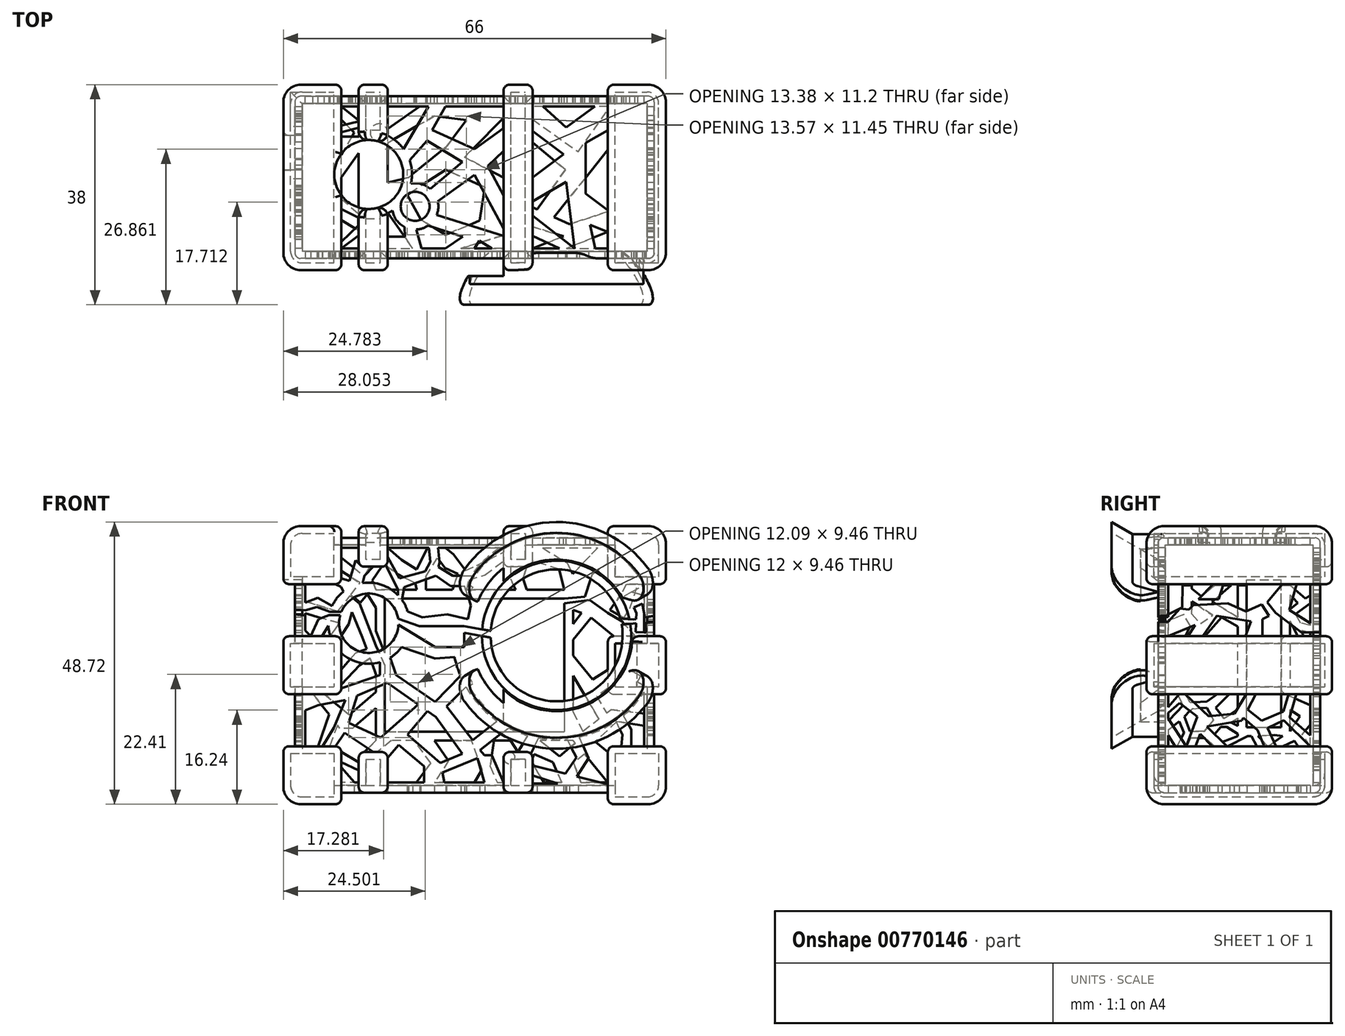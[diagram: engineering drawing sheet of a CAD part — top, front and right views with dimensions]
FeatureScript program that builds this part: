
annotation { "Feature Type Name" : "Feature", "Feature Type Description" : "" }
export const myFeature = defineFeature(function(context is Context, id is Id, definition is map)
    precondition{}
    {
        {
            var Q0;
            Q0=qCreatedBy(makeId("Front.planeOp"),FACE);
            var sketch = newSketch(context, id + "F0", { "sketchPlane" : qUnion([Q0])});
            skLineSegment(sketch, "E0.bottom", {"start": v(-31, 22) * mm, "end": v(31, 22) * mm});
            skLineSegment(sketch, "E0.top", {"start": v(-31, -22) * mm, "end": v(31, -22) * mm});
            skLineSegment(sketch, "E0.left", {"start": v(-31, 22) * mm, "end": v(-31, -22) * mm});
            skLineSegment(sketch, "E0.right", {"start": v(31, 22) * mm, "end": v(31, -22) * mm});
            skPoint(sketch, "E0.middle", {"position": v(0, 0) * mm});
            skSolve(sketch);
        }
        {
            var Q0;
            Q0=qSketchRegion(id+"F0",true);
            extrude(context, id + "F1", {"entities" : qUnion([Q0]), "endBound" : BoundingType.SYMMETRIC, "depth" : (25.5 + 1.25 + 1.25) * mm, "offsetDistance" : 25 * mm});
        }
        {
            var Q0;
            Q0=qCreatedBy(makeId("Front.planeOp"),FACE);
            var sketch = newSketch(context, id + "F2", { "sketchPlane" : qUnion([Q0])});
            skLineSegment(sketch, "E1.bottom", {"start": v(-33, 24) * mm, "end": v(-23, 24) * mm});
            skLineSegment(sketch, "E1.top", {"start": v(-33, 14) * mm, "end": v(-23, 14) * mm});
            skLineSegment(sketch, "E1.left", {"start": v(-33, 24) * mm, "end": v(-33, 14) * mm});
            skLineSegment(sketch, "E1.right", {"start": v(-23, 24) * mm, "end": v(-23, 14) * mm});
            skLineSegment(sketch, "E2.bottom", {"start": v(-20, 24) * mm, "end": v(-15, 24) * mm});
            skLineSegment(sketch, "E2.top", {"start": v(-20, 17) * mm, "end": v(-15, 17) * mm});
            skLineSegment(sketch, "E2.left", {"start": v(-20, 24) * mm, "end": v(-20, 17) * mm});
            skLineSegment(sketch, "E2.right", {"start": v(-15, 24) * mm, "end": v(-15, 17) * mm});
            skLineSegment(sketch, "E3.bottom", {"start": v(23, 24) * mm, "end": v(33, 24) * mm});
            skLineSegment(sketch, "E3.top", {"start": v(23, 14) * mm, "end": v(33, 14) * mm});
            skLineSegment(sketch, "E3.left", {"start": v(23, 24) * mm, "end": v(23, 14) * mm});
            skLineSegment(sketch, "E3.right", {"start": v(33, 24) * mm, "end": v(33, 14) * mm});
            skLineSegment(sketch, "E4.bottom", {"start": v(-33, 5) * mm, "end": v(-23, 5) * mm});
            skLineSegment(sketch, "E4.top", {"start": v(-33, -5) * mm, "end": v(-23, -5) * mm});
            skLineSegment(sketch, "E4.left", {"start": v(-33, 5) * mm, "end": v(-33, -5) * mm});
            skLineSegment(sketch, "E4.right", {"start": v(-23, 5) * mm, "end": v(-23, -5) * mm});
            skLineSegment(sketch, "E5.bottom", {"start": v(-33, -14) * mm, "end": v(-23, -14) * mm});
            skLineSegment(sketch, "E5.top", {"start": v(-33, -24) * mm, "end": v(-23, -24) * mm});
            skLineSegment(sketch, "E5.left", {"start": v(-33, -14) * mm, "end": v(-33, -24) * mm});
            skLineSegment(sketch, "E5.right", {"start": v(-23, -14) * mm, "end": v(-23, -24) * mm});
            skLineSegment(sketch, "E6.bottom", {"start": v(-20, -15) * mm, "end": v(-15, -15) * mm});
            skLineSegment(sketch, "E6.top", {"start": v(-20, -22) * mm, "end": v(-15, -22) * mm});
            skLineSegment(sketch, "E6.left", {"start": v(-20, -15) * mm, "end": v(-20, -22) * mm});
            skLineSegment(sketch, "E6.right", {"start": v(-15, -15) * mm, "end": v(-15, -22) * mm});
            skLineSegment(sketch, "E7.bottom", {"start": v(23, -14) * mm, "end": v(33, -14) * mm});
            skLineSegment(sketch, "E7.top", {"start": v(23, -24) * mm, "end": v(33, -24) * mm});
            skLineSegment(sketch, "E7.left", {"start": v(23, -14) * mm, "end": v(23, -24) * mm});
            skLineSegment(sketch, "E7.right", {"start": v(33, -14) * mm, "end": v(33, -24) * mm});
            skLineSegment(sketch, "E8.bottom", {"start": v(23, 5) * mm, "end": v(33, 5) * mm});
            skLineSegment(sketch, "E8.top", {"start": v(23, -5) * mm, "end": v(33, -5) * mm});
            skLineSegment(sketch, "E8.left", {"start": v(23, 5) * mm, "end": v(23, -5) * mm});
            skLineSegment(sketch, "E8.right", {"start": v(33, 5) * mm, "end": v(33, -5) * mm});
            skLineSegment(sketch, "E9.bottom", {"start": v(5, 24) * mm, "end": v(10, 24) * mm});
            skLineSegment(sketch, "E9.top", {"start": v(5, 17) * mm, "end": v(10, 17) * mm});
            skLineSegment(sketch, "E9.left", {"start": v(5, 24) * mm, "end": v(5, 17) * mm});
            skLineSegment(sketch, "E9.right", {"start": v(10, 24) * mm, "end": v(10, 17) * mm});
            skLineSegment(sketch, "E10.bottom", {"start": v(5, -15) * mm, "end": v(10, -15) * mm});
            skLineSegment(sketch, "E10.top", {"start": v(5, -22) * mm, "end": v(10, -22) * mm});
            skLineSegment(sketch, "E10.left", {"start": v(5, -15) * mm, "end": v(5, -22) * mm});
            skLineSegment(sketch, "E10.right", {"start": v(10, -15) * mm, "end": v(10, -22) * mm});
            skSolve(sketch);
        }
        {
            var Q0;
            Q0=qSketchRegion(id+"F2",true);
            extrude(context, id + "F3", {"entities" : qUnion([Q0]), "operationType" : NewBodyOperationType.ADD, "endBound" : BoundingType.SYMMETRIC, "depth" : (28 + 4) * mm, "offsetDistance" : 25 * mm});
        }
        {
            var Q0;
            Q0=makeQuery(id+"F1.opExtrude","CAP_FACE",FACE,{"disambiguationData":[OSD([sQuery(id+"F0.wireOp",EDGE,"E0.bottom"),sQuery(id+"F0.wireOp",EDGE,"E0.top"),sQuery(id+"F0.wireOp",EDGE,"E0.left"),sQuery(id+"F0.wireOp",EDGE,"E0.right")])],"isStart":false});
            var Q1;
            Q1=makeQuery(id+"F1.opExtrude","SWEPT_BODY",BODY,{"disambiguationData":[OSD([sQuery(id+"F0.wireOp",EDGE,"E0.bottom"),sQuery(id+"F0.wireOp",EDGE,"E0.top"),sQuery(id+"F0.wireOp",EDGE,"E0.left"),sQuery(id+"F0.wireOp",EDGE,"E0.right")])]});
            shell(context, id + "F4", {"isHollow" : true, "entities" : qUnion([Q0]), "parts" : qUnion([Q1]), "thickness" : 1.25 * mm});
        }
        {
            var Q0;
            {var subQ0=sQuery(id+"F2.wireOp",EDGE,"E8.right");var subQ1=sQuery(id+"F2.wireOp",EDGE,"E8.left");var subQ2=sQuery(id+"F2.wireOp",EDGE,"E8.top");var subQ3=sQuery(id+"F2.wireOp",EDGE,"E8.bottom");Q0=makeQuery(id+"F4.opShell","OFFSET_FACE",FACE,{"disambiguationData":[OSD([subQ3,subQ2,subQ1,subQ0]),TDD([makeQuery(id+"F3.opExtrude","CAP_FACE",FACE,{"disambiguationData":[OSD([subQ3,subQ2,subQ1,subQ0])],"isStart":false})])]});}
            var sketch = newSketch(context, id + "F5", { "sketchPlane" : qUnion([Q0])});
            skLineSegment(sketch, "E11.bottom", {"start": v(-24.25, 3.75) * mm, "end": v(-28, 3.75) * mm});
            skLineSegment(sketch, "E11.top", {"start": v(-24.25, -3.75) * mm, "end": v(-28, -3.75) * mm});
            skLineSegment(sketch, "E11.left", {"start": v(-24.25, 3.75) * mm, "end": v(-24.25, -3.75) * mm});
            skLineSegment(sketch, "E11.right", {"start": v(-28, 3.75) * mm, "end": v(-28, -3.75) * mm});
            skSolve(sketch);
        }
        {
            var Q0;
            Q0 = qSketchRegion(id + "F5", true);
            extrude(context, id + "F6", {"entities" : qUnion([Q0]), "operationType" : NewBodyOperationType.ADD, "depth" : 2 * mm, "offsetDistance" : 25 * mm});
        }
        {
            var Q0;
            Q0=makeQuery(id+"F1.opExtrude","CAP_FACE",FACE,{"disambiguationData":[OSD([sQuery(id+"F0.wireOp",EDGE,"E0.bottom"),sQuery(id+"F0.wireOp",EDGE,"E0.top"),sQuery(id+"F0.wireOp",EDGE,"E0.left"),sQuery(id+"F0.wireOp",EDGE,"E0.right")])],"isStart":false});
            var sketch = newSketch(context, id + "F7", { "sketchPlane" : qUnion([Q0])});
            skCircle(sketch, "E12", {"center": v(14.15, 5.15) * mm, "radius": 10.5 * mm});
            skCircle(sketch, "E13", {"center": v(-18.25, 7.25) * mm, "radius": 5.12 * mm});
            skSolve(sketch);
        }
        {
            var Q0;
            Q0=qSketchRegion(id+"F7",true);
            extrude(context, id + "F8", {"entities" : qUnion([Q0]), "operationType" : NewBodyOperationType.REMOVE, "endBound" : BoundingType.SYMMETRIC, "oppositeDirection" : true, "depth" : 10 * mm, "offsetDistance" : 25 * mm});
        }
        {
            var Q0;
            Q0=makeQuery(id+"F1.opExtrude","CAP_FACE",FACE,{"disambiguationData":[OSD([sQuery(id+"F0.wireOp",EDGE,"E0.bottom"),sQuery(id+"F0.wireOp",EDGE,"E0.top"),sQuery(id+"F0.wireOp",EDGE,"E0.left"),sQuery(id+"F0.wireOp",EDGE,"E0.right")])],"isStart":true});
            var sketch = newSketch(context, id + "F9", { "sketchPlane" : qUnion([Q0])});
            skLineSegment(sketch, "E14.bottom", {"start": v(-15.5, -11.5) * mm, "end": v(15.5, -11.5) * mm});
            skLineSegment(sketch, "E14.top", {"start": v(-15.5, 11.5) * mm, "end": v(15.5, 11.5) * mm});
            skLineSegment(sketch, "E14.left", {"start": v(-15.5, -11.5) * mm, "end": v(-15.5, 11.5) * mm});
            skLineSegment(sketch, "E14.right", {"start": v(15.5, -11.5) * mm, "end": v(15.5, 11.5) * mm});
            skPoint(sketch, "E14.middle", {"position": v(0, 0) * mm});
            skSolve(sketch);
        }
        {
            var Q0;
            Q0=qSketchRegion(id+"F9",true);
            extrude(context, id + "F10", {"entities" : qUnion([Q0]), "operationType" : NewBodyOperationType.REMOVE, "endBound" : BoundingType.SYMMETRIC, "oppositeDirection" : true, "depth" : 10 * mm, "offsetDistance" : 25 * mm});
        }
        {
            var Q0;
            Q0=makeQuery(id+"F3.opExtrude","SWEPT_FACE",FACE,{"disambiguationData":[OSD([sQuery(id+"F2.wireOp",EDGE,"E4.left")])]});
            var sketch = newSketch(context, id + "F11", { "sketchPlane" : qUnion([Q0])});
            skLineSegment(sketch, "E15.bottom", {"start": v(-7.25, 14.75) * mm, "end": v(-1.25, 14.75) * mm});
            skLineSegment(sketch, "E15.top", {"start": v(-7.25, -10.75) * mm, "end": v(-1.25, -10.75) * mm});
            skLineSegment(sketch, "E15.left", {"start": v(-7.25, 14.75) * mm, "end": v(-7.25, -10.75) * mm});
            skLineSegment(sketch, "E15.right", {"start": v(-1.25, 14.75) * mm, "end": v(-1.25, -10.75) * mm});
            skSolve(sketch);
        }
        {
            var Q0;
            Q0=qSketchRegion(id+"F11",true);
            extrude(context, id + "F12", {"entities" : qUnion([Q0]), "operationType" : NewBodyOperationType.REMOVE, "oppositeDirection" : true, "depth" : 10 * mm, "offsetDistance" : 25 * mm});
        }
        {
            var Q0;
            {var subQ3=sQuery(id+"F0.wireOp",EDGE,"E0.bottom");Q0=makeQuery(id+"F3.boolean.opBoolean","SPLIT",FACE,{"disambiguationData":[TD([makeQuery(id+"F3.opExtrude","SWEPT_FACE",FACE,{"disambiguationData":[OSD([sQuery(id+"F2.wireOp",EDGE,"E1.right")])]})])],"derivedFrom":makeQuery(id+"F1.opExtrude","SWEPT_FACE",FACE,{"disambiguationData":[OSD([subQ3])]})});}
            var sketch = newSketch(context, id + "F13", { "sketchPlane" : qUnion([Q0])});
            skCircle(sketch, "E16", {"center": v(-18.25, 0.5) * mm, "radius": 5.95 * mm});
            skCircle(sketch, "E17", {"center": v(-10.25, -5) * mm, "radius": 2.5 * mm});
            skSolve(sketch);
        }
        {
            var Q0;
            Q0=qSketchRegion(id+"F13",true);
            extrude(context, id + "F14", {"entities" : qUnion([Q0]), "operationType" : NewBodyOperationType.REMOVE, "endBound" : BoundingType.SYMMETRIC, "oppositeDirection" : true, "depth" : 25 * mm, "offsetDistance" : 25 * mm});
        }
        {
            var Q0;
            Q0=makeQuery(id+"F1.opExtrude","CAP_FACE",FACE,{"disambiguationData":[OSD([sQuery(id+"F0.wireOp",EDGE,"E0.bottom"),sQuery(id+"F0.wireOp",EDGE,"E0.top"),sQuery(id+"F0.wireOp",EDGE,"E0.left"),sQuery(id+"F0.wireOp",EDGE,"E0.right")])],"isStart":false});
            var sketch = newSketch(context, id + "F15", { "sketchPlane" : qUnion([Q0])});
            skArc(sketch, "E18", {"start": v(2.93, -1.32) * mm, "mid": v(14.15, -7.8) * mm, "end": v(25.37, -1.32) * mm});
            skArc(sketch, "E19", {"start": v(27.1, 12.63) * mm, "mid": v(14.15, 20.1) * mm, "end": v(1.2, 12.62) * mm});
            skPoint(sketch, "E20.endSnap0", {"position": v(-15, 19.5) * mm});
            skLineSegment(sketch, "E21", {"start": v(25.37, 11.63) * mm, "end": v(27.1, 12.63) * mm});
            skLineSegment(sketch, "E22", {"start": v(2.93, -1.33) * mm, "end": v(1.2, -2.33) * mm});
            skLineSegment(sketch, "E23", {"start": v(2.93, 11.63) * mm, "end": v(1.2, 12.63) * mm});
            skPoint(sketch, "E24", {"position": v(27, -5) * mm});
            skLineSegment(sketch, "E25", {"start": v(25.37, -1.32) * mm, "end": v(27.1, -2.32) * mm});
            skArc(sketch, "E26.trimOffspring", {"start": v(25.37, 11.63) * mm, "mid": v(14.15, 18.1) * mm, "end": v(2.93, 11.63) * mm});
            skArc(sketch, "E27.trimOffspring", {"start": v(1.2, -2.33) * mm, "mid": v(14.15, -9.8) * mm, "end": v(27.1, -2.32) * mm});
            skSolve(sketch);
        }
        {
            var Q0;
            Q0=qSketchRegion(id+"F15",true);
            extrude(context, id + "F16", {"entities" : qUnion([Q0]), "operationType" : NewBodyOperationType.ADD, "depth" : 8 * mm, "offsetDistance" : 25 * mm, "hasDraft" : true, "draftAngle" : 30 * degree});
        }
        {
            var Q0;
            Q0=makeQuery(id+"F16.boolean.opBoolean","MERGE",FACE,{"derivedFrom":[makeQuery(id+"F16.opExtrude","CAP_FACE",FACE,{"disambiguationData":[OSD([sQuery(id+"F15.wireOp",EDGE,"E18"),sQuery(id+"F15.wireOp",EDGE,"E22"),sQuery(id+"F15.wireOp",EDGE,"E25"),sQuery(id+"F15.wireOp",EDGE,"E27.trimOffspring")])],"isStart":false}),makeQuery(id+"F16.opExtrude","CAP_FACE",FACE,{"disambiguationData":[OSD([sQuery(id+"F15.wireOp",EDGE,"E19"),sQuery(id+"F15.wireOp",EDGE,"E21"),sQuery(id+"F15.wireOp",EDGE,"E23"),sQuery(id+"F15.wireOp",EDGE,"E26.trimOffspring")])],"isStart":false})]});
            var sketch = newSketch(context, id + "F17", { "sketchPlane" : qUnion([Q0])});
            skCircle(sketch, "E28", {"center": v(14.15, 5.15) * mm, "radius": 17.7 * mm});
            skSolve(sketch);
        }
        {
            var Q0;
            Q0=qSketchRegion(id+"F17",true);
            extrude(context, id + "F18", {"entities" : qUnion([Q0]), "operationType" : NewBodyOperationType.REMOVE, "oppositeDirection" : true, "depth" : 8 * mm, "offsetDistance" : 25 * mm, "hasDraft" : true, "draftAngle" : 30 * degree, "draftPullDirection" : true});
        }
        {
            var Q0;
            Q0=makeQuery(id+"F4.opShell","OFFSET_EDGE",EDGE,{"disambiguationData":[OSD([sQuery(id+"F2.wireOp",EDGE,"E7.top"),sQuery(id+"F2.wireOp",EDGE,"E7.right")])]});
            var Q1;
            Q1=makeQuery(id+"F4.opShell","OFFSET_EDGE",EDGE,{"disambiguationData":[OSD([sQuery(id+"F2.wireOp",EDGE,"E3.bottom"),sQuery(id+"F2.wireOp",EDGE,"E3.right")])]});
            var Q2;
            Q2=makeQuery(id+"F4.opShell","OFFSET_EDGE",EDGE,{"disambiguationData":[OSD([sQuery(id+"F2.wireOp",EDGE,"E5.top"),sQuery(id+"F2.wireOp",EDGE,"E5.left")])]});
            var Q3;
            Q3=makeQuery(id+"F4.opShell","OFFSET_EDGE",EDGE,{"disambiguationData":[OSD([sQuery(id+"F2.wireOp",EDGE,"E1.bottom"),sQuery(id+"F2.wireOp",EDGE,"E1.left")])]});
            var Q4;
            {var subQ0=sQuery(id+"F2.wireOp",EDGE,"E7.right");Q4=makeQuery(id+"F4.opShell","OFFSET_EDGE",EDGE,{"disambiguationData":[OSD([subQ0]),TDD([makeQuery(id+"F3.opExtrude","CAP_EDGE",EDGE,{"disambiguationData":[OSD([subQ0])],"isStart":false})])]});}
            var Q5;
            {var subQ0=sQuery(id+"F2.wireOp",EDGE,"E7.top");Q5=makeQuery(id+"F4.opShell","OFFSET_EDGE",EDGE,{"disambiguationData":[OSD([subQ0]),TDD([makeQuery(id+"F3.opExtrude","CAP_EDGE",EDGE,{"disambiguationData":[OSD([subQ0])],"isStart":false})])]});}
            var Q6;
            {var subQ0=sQuery(id+"F2.wireOp",EDGE,"E6.top");Q6=makeQuery(id+"F4.opShell","OFFSET_EDGE",EDGE,{"disambiguationData":[OSD([subQ0]),TDD([makeQuery(id+"F3.opExtrude","CAP_EDGE",EDGE,{"disambiguationData":[OSD([subQ0])],"isStart":false})])]});}
            var Q7;
            {var subQ0=sQuery(id+"F2.wireOp",EDGE,"E5.top");Q7=makeQuery(id+"F4.opShell","OFFSET_EDGE",EDGE,{"disambiguationData":[OSD([subQ0]),TDD([makeQuery(id+"F3.opExtrude","CAP_EDGE",EDGE,{"disambiguationData":[OSD([subQ0])],"isStart":false})])]});}
            var Q8;
            {var subQ0=sQuery(id+"F2.wireOp",EDGE,"E5.left");Q8=makeQuery(id+"F4.opShell","OFFSET_EDGE",EDGE,{"disambiguationData":[OSD([subQ0]),TDD([makeQuery(id+"F3.opExtrude","CAP_EDGE",EDGE,{"disambiguationData":[OSD([subQ0])],"isStart":false})])]});}
            var Q9;
            {var subQ0=sQuery(id+"F2.wireOp",EDGE,"E4.left");Q9=makeQuery(id+"F4.opShell","OFFSET_EDGE",EDGE,{"disambiguationData":[OSD([subQ0]),TDD([makeQuery(id+"F3.opExtrude","CAP_EDGE",EDGE,{"disambiguationData":[OSD([subQ0])],"isStart":false})])]});}
            var Q10;
            {var subQ0=sQuery(id+"F2.wireOp",EDGE,"E1.left");Q10=makeQuery(id+"F4.opShell","OFFSET_EDGE",EDGE,{"disambiguationData":[OSD([subQ0]),TDD([makeQuery(id+"F3.opExtrude","CAP_EDGE",EDGE,{"disambiguationData":[OSD([subQ0])],"isStart":false})])]});}
            var Q11;
            {var subQ0=sQuery(id+"F2.wireOp",EDGE,"E1.bottom");Q11=makeQuery(id+"F4.opShell","OFFSET_EDGE",EDGE,{"disambiguationData":[OSD([subQ0]),TDD([makeQuery(id+"F3.opExtrude","CAP_EDGE",EDGE,{"disambiguationData":[OSD([subQ0])],"isStart":false})])]});}
            var Q12;
            {var subQ0=sQuery(id+"F2.wireOp",EDGE,"E2.bottom");Q12=makeQuery(id+"F4.opShell","OFFSET_EDGE",EDGE,{"disambiguationData":[OSD([subQ0]),TDD([makeQuery(id+"F3.opExtrude","CAP_EDGE",EDGE,{"disambiguationData":[OSD([subQ0])],"isStart":false})])]});}
            var Q13;
            {var subQ0=sQuery(id+"F2.wireOp",EDGE,"E3.bottom");Q13=makeQuery(id+"F4.opShell","OFFSET_EDGE",EDGE,{"disambiguationData":[OSD([subQ0]),TDD([makeQuery(id+"F3.opExtrude","CAP_EDGE",EDGE,{"disambiguationData":[OSD([subQ0])],"isStart":false})])]});}
            var Q14;
            {var subQ0=sQuery(id+"F2.wireOp",EDGE,"E3.right");Q14=makeQuery(id+"F4.opShell","OFFSET_EDGE",EDGE,{"disambiguationData":[OSD([subQ0]),TDD([makeQuery(id+"F3.opExtrude","CAP_EDGE",EDGE,{"disambiguationData":[OSD([subQ0])],"isStart":false})])]});}
            var Q15;
            {var subQ0=sQuery(id+"F2.wireOp",EDGE,"E6.top");Q15=makeQuery(id+"F4.opShell","OFFSET_EDGE",EDGE,{"disambiguationData":[OSD([subQ0]),TDD([makeQuery(id+"F3.opExtrude","CAP_EDGE",EDGE,{"disambiguationData":[OSD([subQ0])],"isStart":true})])]});}
            var Q16;
            {var subQ0=sQuery(id+"F2.wireOp",EDGE,"E5.top");Q16=makeQuery(id+"F4.opShell","OFFSET_EDGE",EDGE,{"disambiguationData":[OSD([subQ0]),TDD([makeQuery(id+"F3.opExtrude","CAP_EDGE",EDGE,{"disambiguationData":[OSD([subQ0])],"isStart":true})])]});}
            var Q17;
            {var subQ0=sQuery(id+"F2.wireOp",EDGE,"E7.top");Q17=makeQuery(id+"F4.opShell","OFFSET_EDGE",EDGE,{"disambiguationData":[OSD([subQ0]),TDD([makeQuery(id+"F3.opExtrude","CAP_EDGE",EDGE,{"disambiguationData":[OSD([subQ0])],"isStart":true})])]});}
            var Q18;
            {var subQ0=sQuery(id+"F2.wireOp",EDGE,"E7.right");Q18=makeQuery(id+"F4.opShell","OFFSET_EDGE",EDGE,{"disambiguationData":[OSD([subQ0]),TDD([makeQuery(id+"F3.opExtrude","CAP_EDGE",EDGE,{"disambiguationData":[OSD([subQ0])],"isStart":true})])]});}
            var Q19;
            {var subQ0=sQuery(id+"F2.wireOp",EDGE,"E8.right");Q19=makeQuery(id+"F4.opShell","OFFSET_EDGE",EDGE,{"disambiguationData":[OSD([subQ0]),TDD([makeQuery(id+"F3.opExtrude","CAP_EDGE",EDGE,{"disambiguationData":[OSD([subQ0])],"isStart":true})])]});}
            var Q20;
            {var subQ0=sQuery(id+"F2.wireOp",EDGE,"E3.right");Q20=makeQuery(id+"F4.opShell","OFFSET_EDGE",EDGE,{"disambiguationData":[OSD([subQ0]),TDD([makeQuery(id+"F3.opExtrude","CAP_EDGE",EDGE,{"disambiguationData":[OSD([subQ0])],"isStart":true})])]});}
            var Q21;
            {var subQ0=sQuery(id+"F2.wireOp",EDGE,"E3.bottom");Q21=makeQuery(id+"F4.opShell","OFFSET_EDGE",EDGE,{"disambiguationData":[OSD([subQ0]),TDD([makeQuery(id+"F3.opExtrude","CAP_EDGE",EDGE,{"disambiguationData":[OSD([subQ0])],"isStart":true})])]});}
            var Q22;
            {var subQ0=sQuery(id+"F2.wireOp",EDGE,"E2.bottom");Q22=makeQuery(id+"F4.opShell","OFFSET_EDGE",EDGE,{"disambiguationData":[OSD([subQ0]),TDD([makeQuery(id+"F3.opExtrude","CAP_EDGE",EDGE,{"disambiguationData":[OSD([subQ0])],"isStart":true})])]});}
            var Q23;
            {var subQ0=sQuery(id+"F2.wireOp",EDGE,"E1.left");Q23=makeQuery(id+"F4.opShell","OFFSET_EDGE",EDGE,{"disambiguationData":[OSD([subQ0]),TDD([makeQuery(id+"F3.opExtrude","CAP_EDGE",EDGE,{"disambiguationData":[OSD([subQ0])],"isStart":true})])]});}
            var Q24;
            {var subQ0=sQuery(id+"F2.wireOp",EDGE,"E1.bottom");Q24=makeQuery(id+"F4.opShell","OFFSET_EDGE",EDGE,{"disambiguationData":[OSD([subQ0]),TDD([makeQuery(id+"F3.opExtrude","CAP_EDGE",EDGE,{"disambiguationData":[OSD([subQ0])],"isStart":true})])]});}
            fillet(context, id + "F19", {"entities" : qUnion([Q0, Q1, Q2, Q3, Q4, Q5, Q6, Q7, Q8, Q9, Q10, Q11, Q12, Q13, Q14, Q15, Q16, Q17, Q18, Q19, Q20, Q21, Q22, Q23, Q24]), "radius" : 2 * mm, "tangentPropagation" : true, "allowEdgeOverflow" : false});
        }
        {
            var Q0;
            Q0=makeQuery(id+"F3.opExtrude","CAP_EDGE",EDGE,{"disambiguationData":[OSD([sQuery(id+"F2.wireOp",EDGE,"E1.bottom")])],"isStart":false});
            var Q1;
            Q1=makeQuery(id+"F3.opExtrude","CAP_EDGE",EDGE,{"disambiguationData":[OSD([sQuery(id+"F2.wireOp",EDGE,"E2.bottom")])],"isStart":false});
            var Q2;
            Q2=makeQuery(id+"F3.opExtrude","CAP_EDGE",EDGE,{"disambiguationData":[OSD([sQuery(id+"F2.wireOp",EDGE,"E3.bottom")])],"isStart":false});
            var Q3;
            Q3=makeQuery(id+"F3.opExtrude","SWEPT_EDGE",EDGE,{"disambiguationData":[OSD([sQuery(id+"F2.wireOp",EDGE,"E3.bottom"),sQuery(id+"F2.wireOp",EDGE,"E3.right")])]});
            var Q4;
            Q4=makeQuery(id+"F3.opExtrude","CAP_EDGE",EDGE,{"disambiguationData":[OSD([sQuery(id+"F2.wireOp",EDGE,"E8.right")])],"isStart":false});
            var Q5;
            Q5=makeQuery(id+"F3.opExtrude","CAP_EDGE",EDGE,{"disambiguationData":[OSD([sQuery(id+"F2.wireOp",EDGE,"E7.right")])],"isStart":false});
            var Q6;
            Q6=makeQuery(id+"F3.opExtrude","CAP_EDGE",EDGE,{"disambiguationData":[OSD([sQuery(id+"F2.wireOp",EDGE,"E3.right")])],"isStart":false});
            var Q7;
            Q7=makeQuery(id+"F3.opExtrude","CAP_EDGE",EDGE,{"disambiguationData":[OSD([sQuery(id+"F2.wireOp",EDGE,"E7.top")])],"isStart":false});
            var Q8;
            Q8=makeQuery(id+"F3.opExtrude","SWEPT_EDGE",EDGE,{"disambiguationData":[OSD([sQuery(id+"F2.wireOp",EDGE,"E7.top"),sQuery(id+"F2.wireOp",EDGE,"E7.right")])]});
            var Q9;
            Q9=makeQuery(id+"F3.opExtrude","CAP_EDGE",EDGE,{"disambiguationData":[OSD([sQuery(id+"F2.wireOp",EDGE,"E5.top")])],"isStart":false});
            var Q10;
            Q10=makeQuery(id+"F3.opExtrude","CAP_EDGE",EDGE,{"disambiguationData":[OSD([sQuery(id+"F2.wireOp",EDGE,"E5.left")])],"isStart":false});
            var Q11;
            Q11=makeQuery(id+"F3.opExtrude","CAP_EDGE",EDGE,{"disambiguationData":[OSD([sQuery(id+"F2.wireOp",EDGE,"E4.left")])],"isStart":false});
            var Q12;
            Q12=makeQuery(id+"F3.opExtrude","CAP_EDGE",EDGE,{"disambiguationData":[OSD([sQuery(id+"F2.wireOp",EDGE,"E1.left")])],"isStart":false});
            var Q13;
            Q13=makeQuery(id+"F3.opExtrude","CAP_EDGE",EDGE,{"disambiguationData":[OSD([sQuery(id+"F2.wireOp",EDGE,"E2.bottom")])],"isStart":true});
            var Q14;
            Q14=makeQuery(id+"F3.opExtrude","CAP_EDGE",EDGE,{"disambiguationData":[OSD([sQuery(id+"F2.wireOp",EDGE,"E1.bottom")])],"isStart":true});
            var Q15;
            Q15=makeQuery(id+"F3.opExtrude","CAP_EDGE",EDGE,{"disambiguationData":[OSD([sQuery(id+"F2.wireOp",EDGE,"E1.left")])],"isStart":true});
            var Q16;
            Q16=makeQuery(id+"F3.opExtrude","CAP_EDGE",EDGE,{"disambiguationData":[OSD([sQuery(id+"F2.wireOp",EDGE,"E4.left")])],"isStart":true});
            var Q17;
            Q17=makeQuery(id+"F3.opExtrude","CAP_EDGE",EDGE,{"disambiguationData":[OSD([sQuery(id+"F2.wireOp",EDGE,"E5.left")])],"isStart":true});
            var Q18;
            Q18=makeQuery(id+"F3.opExtrude","CAP_EDGE",EDGE,{"disambiguationData":[OSD([sQuery(id+"F2.wireOp",EDGE,"E5.top")])],"isStart":true});
            var Q19;
            Q19=makeQuery(id+"F3.opExtrude","CAP_EDGE",EDGE,{"disambiguationData":[OSD([sQuery(id+"F2.wireOp",EDGE,"E3.right")])],"isStart":true});
            var Q20;
            Q20=makeQuery(id+"F3.opExtrude","CAP_EDGE",EDGE,{"disambiguationData":[OSD([sQuery(id+"F2.wireOp",EDGE,"E3.bottom")])],"isStart":true});
            var Q21;
            Q21=makeQuery(id+"F3.opExtrude","CAP_EDGE",EDGE,{"disambiguationData":[OSD([sQuery(id+"F2.wireOp",EDGE,"E8.right")])],"isStart":true});
            var Q22;
            Q22=makeQuery(id+"F3.opExtrude","CAP_EDGE",EDGE,{"disambiguationData":[OSD([sQuery(id+"F2.wireOp",EDGE,"E7.top")])],"isStart":true});
            var Q23;
            Q23=makeQuery(id+"F3.opExtrude","CAP_EDGE",EDGE,{"disambiguationData":[OSD([sQuery(id+"F2.wireOp",EDGE,"E7.right")])],"isStart":true});
            var Q24;
            Q24=makeQuery(id+"F3.opExtrude","SWEPT_EDGE",EDGE,{"disambiguationData":[OSD([sQuery(id+"F2.wireOp",EDGE,"E5.top"),sQuery(id+"F2.wireOp",EDGE,"E5.left")])]});
            var Q25;
            Q25=makeQuery(id+"F3.opExtrude","SWEPT_EDGE",EDGE,{"disambiguationData":[OSD([sQuery(id+"F2.wireOp",EDGE,"E1.bottom"),sQuery(id+"F2.wireOp",EDGE,"E1.left")])]});
            var Q26;
            Q26=makeQuery(id+"F3.opExtrude","CAP_EDGE",EDGE,{"disambiguationData":[OSD([sQuery(id+"F2.wireOp",EDGE,"E9.bottom")])],"isStart":false});
            var Q27;
            Q27=makeQuery(id+"F3.opExtrude","CAP_EDGE",EDGE,{"disambiguationData":[OSD([sQuery(id+"F2.wireOp",EDGE,"E9.bottom")])],"isStart":true});
            fillet(context, id + "F20", {"entities" : qUnion([Q0, Q1, Q2, Q3, Q4, Q5, Q6, Q7, Q8, Q9, Q10, Q11, Q12, Q13, Q14, Q15, Q16, Q17, Q18, Q19, Q20, Q21, Q22, Q23, Q24, Q25, Q26, Q27]), "radius" : 3 * mm, "tangentPropagation" : true, "allowEdgeOverflow" : false});
        }
        {
            var Q0;
            {var subQ0=sQuery(id+"F2.wireOp",EDGE,"E1.left");var subQ1=sQuery(id+"F2.wireOp",EDGE,"E1.top");Q0=makeQuery(id+"F12.boolean.opBoolean","SPLIT",EDGE,{"disambiguationData":[TD([makeQuery(id+"F12.opExtrude","SWEPT_FACE",FACE,{"disambiguationData":[OSD([sQuery(id+"F11.wireOp",EDGE,"E15.right")])]})])],"derivedFrom":makeQuery(id+"F3.opExtrude","SWEPT_EDGE",EDGE,{"disambiguationData":[OSD([subQ1,subQ0])]})});}
            var Q1;
            {var subQ0=sQuery(id+"F2.wireOp",EDGE,"E1.left");var subQ1=sQuery(id+"F2.wireOp",EDGE,"E1.top");Q1=makeQuery(id+"F12.boolean.opBoolean","SPLIT",EDGE,{"disambiguationData":[TD([makeQuery(id+"F12.opExtrude","SWEPT_FACE",FACE,{"disambiguationData":[OSD([sQuery(id+"F11.wireOp",EDGE,"E15.left")])]})])],"derivedFrom":makeQuery(id+"F3.opExtrude","SWEPT_EDGE",EDGE,{"disambiguationData":[OSD([subQ1,subQ0])]})});}
            var Q2;
            {var subQ0=sQuery(id+"F2.wireOp",EDGE,"E4.bottom");var subQ1=sQuery(id+"F2.wireOp",EDGE,"E4.left");Q2=makeQuery(id+"F12.boolean.opBoolean","SPLIT",EDGE,{"disambiguationData":[TD([makeQuery(id+"F12.opExtrude","SWEPT_FACE",FACE,{"disambiguationData":[OSD([sQuery(id+"F11.wireOp",EDGE,"E15.left")])]})])],"derivedFrom":makeQuery(id+"F3.opExtrude","SWEPT_EDGE",EDGE,{"disambiguationData":[OSD([subQ0,subQ1])]})});}
            var Q3;
            {var subQ0=sQuery(id+"F2.wireOp",EDGE,"E4.bottom");var subQ1=sQuery(id+"F2.wireOp",EDGE,"E4.left");Q3=makeQuery(id+"F12.boolean.opBoolean","SPLIT",EDGE,{"disambiguationData":[TD([makeQuery(id+"F12.opExtrude","SWEPT_FACE",FACE,{"disambiguationData":[OSD([sQuery(id+"F11.wireOp",EDGE,"E15.right")])]})])],"derivedFrom":makeQuery(id+"F3.opExtrude","SWEPT_EDGE",EDGE,{"disambiguationData":[OSD([subQ0,subQ1])]})});}
            var Q4;
            {var subQ0=sQuery(id+"F2.wireOp",EDGE,"E4.left");var subQ1=sQuery(id+"F2.wireOp",EDGE,"E4.top");Q4=makeQuery(id+"F12.boolean.opBoolean","SPLIT",EDGE,{"disambiguationData":[TD([makeQuery(id+"F12.opExtrude","SWEPT_FACE",FACE,{"disambiguationData":[OSD([sQuery(id+"F11.wireOp",EDGE,"E15.right")])]})])],"derivedFrom":makeQuery(id+"F3.opExtrude","SWEPT_EDGE",EDGE,{"disambiguationData":[OSD([subQ1,subQ0])]})});}
            var Q5;
            {var subQ0=sQuery(id+"F2.wireOp",EDGE,"E4.left");var subQ1=sQuery(id+"F2.wireOp",EDGE,"E4.top");Q5=makeQuery(id+"F12.boolean.opBoolean","SPLIT",EDGE,{"disambiguationData":[TD([makeQuery(id+"F12.opExtrude","SWEPT_FACE",FACE,{"disambiguationData":[OSD([sQuery(id+"F11.wireOp",EDGE,"E15.left")])]})])],"derivedFrom":makeQuery(id+"F3.opExtrude","SWEPT_EDGE",EDGE,{"disambiguationData":[OSD([subQ1,subQ0])]})});}
            var Q6;
            Q6=makeQuery(id+"F3.opExtrude","SWEPT_EDGE",EDGE,{"disambiguationData":[OSD([sQuery(id+"F2.wireOp",EDGE,"E5.bottom"),sQuery(id+"F2.wireOp",EDGE,"E5.left")])]});
            var Q7;
            Q7=makeQuery(id+"F3.opExtrude","CAP_EDGE",EDGE,{"disambiguationData":[OSD([sQuery(id+"F2.wireOp",EDGE,"E1.top")])],"isStart":true});
            var Q8;
            Q8=makeQuery(id+"F3.opExtrude","CAP_EDGE",EDGE,{"disambiguationData":[OSD([sQuery(id+"F2.wireOp",EDGE,"E1.right")])],"isStart":true});
            var Q9;
            Q9=makeQuery(id+"F3.opExtrude","CAP_EDGE",EDGE,{"disambiguationData":[OSD([sQuery(id+"F2.wireOp",EDGE,"E4.bottom")])],"isStart":true});
            var Q10;
            Q10=makeQuery(id+"F3.opExtrude","CAP_EDGE",EDGE,{"disambiguationData":[OSD([sQuery(id+"F2.wireOp",EDGE,"E4.right")])],"isStart":true});
            var Q11;
            Q11=makeQuery(id+"F3.opExtrude","CAP_EDGE",EDGE,{"disambiguationData":[OSD([sQuery(id+"F2.wireOp",EDGE,"E4.top")])],"isStart":true});
            var Q12;
            Q12=makeQuery(id+"F3.opExtrude","CAP_EDGE",EDGE,{"disambiguationData":[OSD([sQuery(id+"F2.wireOp",EDGE,"E5.bottom")])],"isStart":true});
            var Q13;
            Q13=makeQuery(id+"F3.opExtrude","CAP_EDGE",EDGE,{"disambiguationData":[OSD([sQuery(id+"F2.wireOp",EDGE,"E5.right")])],"isStart":true});
            var Q14;
            {var subQ0=sQuery(id+"F2.wireOp",EDGE,"E1.bottom");var subQ1=sQuery(id+"F2.wireOp",EDGE,"E1.right");Q14=makeQuery(id+"F14.boolean.opBoolean","SPLIT",EDGE,{"disambiguationData":[TD([makeQuery(id+"F3.opExtrude","CAP_FACE",FACE,{"disambiguationData":[OSD([subQ0,sQuery(id+"F2.wireOp",EDGE,"E1.top"),sQuery(id+"F2.wireOp",EDGE,"E1.left"),subQ1])],"isStart":true})])],"derivedFrom":makeQuery(id+"F3.opExtrude","SWEPT_EDGE",EDGE,{"disambiguationData":[OSD([subQ0,subQ1])]})});}
            var Q15;
            Q15=makeQuery(id+"F14.boolean.opBoolean","INTERSECT",EDGE,{"derivedFrom":[makeQuery(id+"F3.opExtrude","SWEPT_FACE",FACE,{"disambiguationData":[OSD([sQuery(id+"F2.wireOp",EDGE,"E1.bottom")])]}),makeQuery(id+"F14.opExtrude","SWEPT_FACE",FACE,{"disambiguationData":[OSD([sQuery(id+"F13.wireOp",EDGE,"E16")])]})]});
            var Q16;
            {var subQ0=sQuery(id+"F2.wireOp",EDGE,"E1.bottom");var subQ1=sQuery(id+"F2.wireOp",EDGE,"E1.right");Q16=makeQuery(id+"F14.boolean.opBoolean","SPLIT",EDGE,{"disambiguationData":[TD([makeQuery(id+"F3.opExtrude","CAP_FACE",FACE,{"disambiguationData":[OSD([subQ0,sQuery(id+"F2.wireOp",EDGE,"E1.top"),sQuery(id+"F2.wireOp",EDGE,"E1.left"),subQ1])],"isStart":false})])],"derivedFrom":makeQuery(id+"F3.opExtrude","SWEPT_EDGE",EDGE,{"disambiguationData":[OSD([subQ0,subQ1])]})});}
            var Q17;
            Q17=makeQuery(id+"F3.opExtrude","SWEPT_EDGE",EDGE,{"disambiguationData":[OSD([sQuery(id+"F2.wireOp",EDGE,"E2.bottom"),sQuery(id+"F2.wireOp",EDGE,"E2.left")])]});
            var Q18;
            Q18=makeQuery(id+"F3.opExtrude","SWEPT_EDGE",EDGE,{"disambiguationData":[OSD([sQuery(id+"F2.wireOp",EDGE,"E2.bottom"),sQuery(id+"F2.wireOp",EDGE,"E2.right")])]});
            var Q19;
            Q19=makeQuery(id+"F3.opExtrude","CAP_EDGE",EDGE,{"disambiguationData":[OSD([sQuery(id+"F2.wireOp",EDGE,"E2.right")])],"isStart":true});
            var Q20;
            Q20=makeQuery(id+"F3.opExtrude","CAP_EDGE",EDGE,{"disambiguationData":[OSD([sQuery(id+"F2.wireOp",EDGE,"E2.left")])],"isStart":true});
            var Q21;
            Q21=makeQuery(id+"F3.opExtrude","CAP_EDGE",EDGE,{"disambiguationData":[OSD([sQuery(id+"F2.wireOp",EDGE,"E2.top")])],"isStart":true});
            var Q22;
            Q22=makeQuery(id+"F3.opExtrude","CAP_EDGE",EDGE,{"disambiguationData":[OSD([sQuery(id+"F2.wireOp",EDGE,"E3.top")])],"isStart":true});
            var Q23;
            Q23=makeQuery(id+"F3.opExtrude","CAP_EDGE",EDGE,{"disambiguationData":[OSD([sQuery(id+"F2.wireOp",EDGE,"E3.left")])],"isStart":true});
            var Q24;
            Q24=makeQuery(id+"F3.opExtrude","CAP_EDGE",EDGE,{"disambiguationData":[OSD([sQuery(id+"F2.wireOp",EDGE,"E8.bottom")])],"isStart":true});
            var Q25;
            Q25=makeQuery(id+"F3.opExtrude","CAP_EDGE",EDGE,{"disambiguationData":[OSD([sQuery(id+"F2.wireOp",EDGE,"E8.top")])],"isStart":true});
            var Q26;
            Q26=makeQuery(id+"F3.opExtrude","CAP_EDGE",EDGE,{"disambiguationData":[OSD([sQuery(id+"F2.wireOp",EDGE,"E6.left")])],"isStart":true});
            var Q27;
            Q27=makeQuery(id+"F3.opExtrude","CAP_EDGE",EDGE,{"disambiguationData":[OSD([sQuery(id+"F2.wireOp",EDGE,"E6.bottom")])],"isStart":true});
            var Q28;
            Q28=makeQuery(id+"F3.opExtrude","CAP_EDGE",EDGE,{"disambiguationData":[OSD([sQuery(id+"F2.wireOp",EDGE,"E6.right")])],"isStart":true});
            var Q29;
            Q29=makeQuery(id+"F3.opExtrude","CAP_EDGE",EDGE,{"disambiguationData":[OSD([sQuery(id+"F2.wireOp",EDGE,"E7.left")])],"isStart":true});
            var Q30;
            Q30=makeQuery(id+"F3.opExtrude","CAP_EDGE",EDGE,{"disambiguationData":[OSD([sQuery(id+"F2.wireOp",EDGE,"E7.bottom")])],"isStart":true});
            var Q31;
            Q31=makeQuery(id+"F3.opExtrude","CAP_EDGE",EDGE,{"disambiguationData":[OSD([sQuery(id+"F2.wireOp",EDGE,"E8.left")])],"isStart":true});
            var Q32;
            Q32=makeQuery(id+"F3.opExtrude","SWEPT_EDGE",EDGE,{"disambiguationData":[OSD([sQuery(id+"F2.wireOp",EDGE,"E5.top"),sQuery(id+"F2.wireOp",EDGE,"E5.right")])]});
            var Q33;
            Q33=makeQuery(id+"F3.opExtrude","SWEPT_EDGE",EDGE,{"disambiguationData":[OSD([sQuery(id+"F2.wireOp",EDGE,"E6.top"),sQuery(id+"F2.wireOp",EDGE,"E6.left")])]});
            var Q34;
            Q34=makeQuery(id+"F3.opExtrude","SWEPT_EDGE",EDGE,{"disambiguationData":[OSD([sQuery(id+"F2.wireOp",EDGE,"E7.top"),sQuery(id+"F2.wireOp",EDGE,"E7.left")])]});
            var Q35;
            Q35=makeQuery(id+"F3.opExtrude","SWEPT_EDGE",EDGE,{"disambiguationData":[OSD([sQuery(id+"F2.wireOp",EDGE,"E7.bottom"),sQuery(id+"F2.wireOp",EDGE,"E7.right")])]});
            var Q36;
            Q36=makeQuery(id+"F3.opExtrude","SWEPT_EDGE",EDGE,{"disambiguationData":[OSD([sQuery(id+"F2.wireOp",EDGE,"E8.top"),sQuery(id+"F2.wireOp",EDGE,"E8.right")])]});
            var Q37;
            Q37=makeQuery(id+"F3.opExtrude","SWEPT_EDGE",EDGE,{"disambiguationData":[OSD([sQuery(id+"F2.wireOp",EDGE,"E8.bottom"),sQuery(id+"F2.wireOp",EDGE,"E8.right")])]});
            var Q38;
            Q38=makeQuery(id+"F3.opExtrude","SWEPT_EDGE",EDGE,{"disambiguationData":[OSD([sQuery(id+"F2.wireOp",EDGE,"E3.top"),sQuery(id+"F2.wireOp",EDGE,"E3.right")])]});
            var Q39;
            Q39=makeQuery(id+"F3.opExtrude","SWEPT_EDGE",EDGE,{"disambiguationData":[OSD([sQuery(id+"F2.wireOp",EDGE,"E3.bottom"),sQuery(id+"F2.wireOp",EDGE,"E3.left")])]});
            var Q40;
            Q40=makeQuery(id+"F3.opExtrude","CAP_EDGE",EDGE,{"disambiguationData":[OSD([sQuery(id+"F2.wireOp",EDGE,"E1.right")])],"isStart":false});
            var Q41;
            Q41=makeQuery(id+"F3.opExtrude","CAP_EDGE",EDGE,{"disambiguationData":[OSD([sQuery(id+"F2.wireOp",EDGE,"E1.top")])],"isStart":false});
            var Q42;
            Q42=makeQuery(id+"F3.opExtrude","CAP_EDGE",EDGE,{"disambiguationData":[OSD([sQuery(id+"F2.wireOp",EDGE,"E4.bottom")])],"isStart":false});
            var Q43;
            Q43=makeQuery(id+"F3.opExtrude","CAP_EDGE",EDGE,{"disambiguationData":[OSD([sQuery(id+"F2.wireOp",EDGE,"E4.top")])],"isStart":false});
            var Q44;
            Q44=makeQuery(id+"F3.opExtrude","CAP_EDGE",EDGE,{"disambiguationData":[OSD([sQuery(id+"F2.wireOp",EDGE,"E5.bottom")])],"isStart":false});
            var Q45;
            Q45=makeQuery(id+"F3.opExtrude","CAP_EDGE",EDGE,{"disambiguationData":[OSD([sQuery(id+"F2.wireOp",EDGE,"E5.right")])],"isStart":false});
            var Q46;
            Q46=makeQuery(id+"F3.opExtrude","CAP_EDGE",EDGE,{"disambiguationData":[OSD([sQuery(id+"F2.wireOp",EDGE,"E6.left")])],"isStart":false});
            var Q47;
            Q47=makeQuery(id+"F3.opExtrude","CAP_EDGE",EDGE,{"disambiguationData":[OSD([sQuery(id+"F2.wireOp",EDGE,"E6.bottom")])],"isStart":false});
            var Q48;
            Q48=makeQuery(id+"F3.opExtrude","CAP_EDGE",EDGE,{"disambiguationData":[OSD([sQuery(id+"F2.wireOp",EDGE,"E6.right")])],"isStart":false});
            var Q49;
            Q49=makeQuery(id+"F3.opExtrude","CAP_EDGE",EDGE,{"disambiguationData":[OSD([sQuery(id+"F2.wireOp",EDGE,"E7.left")])],"isStart":false});
            var Q50;
            Q50=makeQuery(id+"F3.opExtrude","CAP_EDGE",EDGE,{"disambiguationData":[OSD([sQuery(id+"F2.wireOp",EDGE,"E7.bottom")])],"isStart":false});
            var Q51;
            Q51=makeQuery(id+"F3.opExtrude","CAP_EDGE",EDGE,{"disambiguationData":[OSD([sQuery(id+"F2.wireOp",EDGE,"E8.top")])],"isStart":false});
            var Q52;
            Q52=makeQuery(id+"F3.opExtrude","CAP_EDGE",EDGE,{"disambiguationData":[OSD([sQuery(id+"F2.wireOp",EDGE,"E8.bottom")])],"isStart":false});
            var Q53;
            Q53=makeQuery(id+"F3.opExtrude","CAP_EDGE",EDGE,{"disambiguationData":[OSD([sQuery(id+"F2.wireOp",EDGE,"E3.top")])],"isStart":false});
            var Q54;
            Q54=makeQuery(id+"F3.opExtrude","CAP_EDGE",EDGE,{"disambiguationData":[OSD([sQuery(id+"F2.wireOp",EDGE,"E3.left")])],"isStart":false});
            var Q55;
            {var subQ0=sQuery(id+"F2.wireOp",EDGE,"E2.bottom");Q55=makeQuery(id+"F20.opFillet","BLEND_EDGE",EDGE,{"blendedFrom":[makeQuery(id+"F3.opExtrude","CAP_EDGE",EDGE,{"disambiguationData":[OSD([subQ0])],"isStart":false}),makeQuery(id+"F3.opExtrude","CAP_FACE",FACE,{"disambiguationData":[OSD([subQ0,sQuery(id+"F2.wireOp",EDGE,"E2.top"),sQuery(id+"F2.wireOp",EDGE,"E2.left"),sQuery(id+"F2.wireOp",EDGE,"E2.right")])],"isStart":false})],"blendedInto":[makeQuery(id+"F3.opExtrude","CAP_FACE",FACE,{"disambiguationData":[OSD([subQ0,sQuery(id+"F2.wireOp",EDGE,"E2.top"),sQuery(id+"F2.wireOp",EDGE,"E2.left"),sQuery(id+"F2.wireOp",EDGE,"E2.right")])],"isStart":false})]});}
            var Q56;
            Q56=makeQuery(id+"F3.opExtrude","CAP_EDGE",EDGE,{"disambiguationData":[OSD([sQuery(id+"F2.wireOp",EDGE,"E2.left")])],"isStart":false});
            var Q57;
            Q57=makeQuery(id+"F3.opExtrude","CAP_EDGE",EDGE,{"disambiguationData":[OSD([sQuery(id+"F2.wireOp",EDGE,"E2.top")])],"isStart":false});
            var Q58;
            Q58=makeQuery(id+"F3.opExtrude","CAP_EDGE",EDGE,{"disambiguationData":[OSD([sQuery(id+"F2.wireOp",EDGE,"E4.right")])],"isStart":false});
            var Q59;
            Q59=makeQuery(id+"F3.opExtrude","SWEPT_EDGE",EDGE,{"disambiguationData":[OSD([sQuery(id+"F2.wireOp",EDGE,"E10.top"),sQuery(id+"F2.wireOp",EDGE,"E10.left")])]});
            var Q60;
            Q60=makeQuery(id+"F3.opExtrude","CAP_EDGE",EDGE,{"disambiguationData":[OSD([sQuery(id+"F2.wireOp",EDGE,"E10.left")])],"isStart":true});
            var Q61;
            Q61=makeQuery(id+"F3.opExtrude","SWEPT_EDGE",EDGE,{"disambiguationData":[OSD([sQuery(id+"F2.wireOp",EDGE,"E10.top"),sQuery(id+"F2.wireOp",EDGE,"E10.right")])]});
            var Q62;
            Q62=makeQuery(id+"F3.opExtrude","CAP_EDGE",EDGE,{"disambiguationData":[OSD([sQuery(id+"F2.wireOp",EDGE,"E9.right")])],"isStart":true});
            var Q63;
            Q63=makeQuery(id+"F3.opExtrude","CAP_EDGE",EDGE,{"disambiguationData":[OSD([sQuery(id+"F2.wireOp",EDGE,"E10.bottom")])],"isStart":true});
            var Q64;
            Q64=makeQuery(id+"F3.opExtrude","CAP_EDGE",EDGE,{"disambiguationData":[OSD([sQuery(id+"F2.wireOp",EDGE,"E9.top")])],"isStart":true});
            var Q65;
            Q65=makeQuery(id+"F3.opExtrude","CAP_EDGE",EDGE,{"disambiguationData":[OSD([sQuery(id+"F2.wireOp",EDGE,"E9.left")])],"isStart":true});
            var Q66;
            Q66=makeQuery(id+"F3.opExtrude","CAP_EDGE",EDGE,{"disambiguationData":[OSD([sQuery(id+"F2.wireOp",EDGE,"E10.bottom")])],"isStart":false});
            var Q67;
            {var subQ0=sQuery(id+"F2.wireOp",EDGE,"E4.right");var subQ1=sQuery(id+"F2.wireOp",EDGE,"E4.top");Q67=makeQuery(id+"F3.boolean.opBoolean","SPLIT",EDGE,{"disambiguationData":[TD([makeQuery(id+"F1.opExtrude","CAP_FACE",FACE,{"disambiguationData":[OSD([sQuery(id+"F0.wireOp",EDGE,"E0.bottom"),sQuery(id+"F0.wireOp",EDGE,"E0.top"),sQuery(id+"F0.wireOp",EDGE,"E0.left"),sQuery(id+"F0.wireOp",EDGE,"E0.right")])],"isStart":false})])],"derivedFrom":makeQuery(id+"F3.opExtrude","SWEPT_EDGE",EDGE,{"disambiguationData":[OSD([subQ1,subQ0])]})});}
            var Q68;
            {var subQ0=sQuery(id+"F2.wireOp",EDGE,"E5.bottom");var subQ1=sQuery(id+"F2.wireOp",EDGE,"E5.right");Q68=makeQuery(id+"F3.boolean.opBoolean","SPLIT",EDGE,{"disambiguationData":[TD([makeQuery(id+"F1.opExtrude","CAP_FACE",FACE,{"disambiguationData":[OSD([sQuery(id+"F0.wireOp",EDGE,"E0.bottom"),sQuery(id+"F0.wireOp",EDGE,"E0.top"),sQuery(id+"F0.wireOp",EDGE,"E0.left"),sQuery(id+"F0.wireOp",EDGE,"E0.right")])],"isStart":false})])],"derivedFrom":makeQuery(id+"F3.opExtrude","SWEPT_EDGE",EDGE,{"disambiguationData":[OSD([subQ0,subQ1])]})});}
            var Q69;
            {var subQ0=sQuery(id+"F2.wireOp",EDGE,"E6.bottom");var subQ1=sQuery(id+"F2.wireOp",EDGE,"E6.right");Q69=makeQuery(id+"F3.boolean.opBoolean","SPLIT",EDGE,{"disambiguationData":[TD([makeQuery(id+"F1.opExtrude","CAP_FACE",FACE,{"disambiguationData":[OSD([sQuery(id+"F0.wireOp",EDGE,"E0.bottom"),sQuery(id+"F0.wireOp",EDGE,"E0.top"),sQuery(id+"F0.wireOp",EDGE,"E0.left"),sQuery(id+"F0.wireOp",EDGE,"E0.right")])],"isStart":false})])],"derivedFrom":makeQuery(id+"F3.opExtrude","SWEPT_EDGE",EDGE,{"disambiguationData":[OSD([subQ0,subQ1])]})});}
            var Q70;
            {var subQ0=sQuery(id+"F2.wireOp",EDGE,"E6.left");var subQ1=sQuery(id+"F2.wireOp",EDGE,"E6.bottom");Q70=makeQuery(id+"F3.boolean.opBoolean","SPLIT",EDGE,{"disambiguationData":[TD([makeQuery(id+"F1.opExtrude","CAP_FACE",FACE,{"disambiguationData":[OSD([sQuery(id+"F0.wireOp",EDGE,"E0.bottom"),sQuery(id+"F0.wireOp",EDGE,"E0.top"),sQuery(id+"F0.wireOp",EDGE,"E0.left"),sQuery(id+"F0.wireOp",EDGE,"E0.right")])],"isStart":false})])],"derivedFrom":makeQuery(id+"F3.opExtrude","SWEPT_EDGE",EDGE,{"disambiguationData":[OSD([subQ1,subQ0])]})});}
            var Q71;
            {var subQ0=sQuery(id+"F2.wireOp",EDGE,"E10.bottom");var subQ1=sQuery(id+"F2.wireOp",EDGE,"E10.left");Q71=makeQuery(id+"F3.boolean.opBoolean","SPLIT",EDGE,{"disambiguationData":[TD([makeQuery(id+"F1.opExtrude","CAP_FACE",FACE,{"disambiguationData":[OSD([sQuery(id+"F0.wireOp",EDGE,"E0.bottom"),sQuery(id+"F0.wireOp",EDGE,"E0.top"),sQuery(id+"F0.wireOp",EDGE,"E0.left"),sQuery(id+"F0.wireOp",EDGE,"E0.right")])],"isStart":false})])],"derivedFrom":makeQuery(id+"F3.opExtrude","SWEPT_EDGE",EDGE,{"disambiguationData":[OSD([subQ0,subQ1])]})});}
            var Q72;
            {var subQ0=sQuery(id+"F2.wireOp",EDGE,"E10.bottom");var subQ1=sQuery(id+"F2.wireOp",EDGE,"E10.right");Q72=makeQuery(id+"F3.boolean.opBoolean","SPLIT",EDGE,{"disambiguationData":[TD([makeQuery(id+"F1.opExtrude","CAP_FACE",FACE,{"disambiguationData":[OSD([sQuery(id+"F0.wireOp",EDGE,"E0.bottom"),sQuery(id+"F0.wireOp",EDGE,"E0.top"),sQuery(id+"F0.wireOp",EDGE,"E0.left"),sQuery(id+"F0.wireOp",EDGE,"E0.right")])],"isStart":false})])],"derivedFrom":makeQuery(id+"F3.opExtrude","SWEPT_EDGE",EDGE,{"disambiguationData":[OSD([subQ0,subQ1])]})});}
            var Q73;
            {var subQ0=sQuery(id+"F2.wireOp",EDGE,"E7.bottom");var subQ1=sQuery(id+"F2.wireOp",EDGE,"E7.left");Q73=makeQuery(id+"F3.boolean.opBoolean","SPLIT",EDGE,{"disambiguationData":[TD([makeQuery(id+"F1.opExtrude","CAP_FACE",FACE,{"disambiguationData":[OSD([sQuery(id+"F0.wireOp",EDGE,"E0.bottom"),sQuery(id+"F0.wireOp",EDGE,"E0.top"),sQuery(id+"F0.wireOp",EDGE,"E0.left"),sQuery(id+"F0.wireOp",EDGE,"E0.right")])],"isStart":false})])],"derivedFrom":makeQuery(id+"F3.opExtrude","SWEPT_EDGE",EDGE,{"disambiguationData":[OSD([subQ0,subQ1])]})});}
            var Q74;
            {var subQ0=sQuery(id+"F2.wireOp",EDGE,"E1.right");var subQ1=sQuery(id+"F2.wireOp",EDGE,"E1.top");Q74=makeQuery(id+"F3.boolean.opBoolean","SPLIT",EDGE,{"disambiguationData":[TD([makeQuery(id+"F1.opExtrude","CAP_FACE",FACE,{"disambiguationData":[OSD([sQuery(id+"F0.wireOp",EDGE,"E0.bottom"),sQuery(id+"F0.wireOp",EDGE,"E0.top"),sQuery(id+"F0.wireOp",EDGE,"E0.left"),sQuery(id+"F0.wireOp",EDGE,"E0.right")])],"isStart":false})])],"derivedFrom":makeQuery(id+"F3.opExtrude","SWEPT_EDGE",EDGE,{"disambiguationData":[OSD([subQ1,subQ0])]})});}
            var Q75;
            {var subQ0=sQuery(id+"F2.wireOp",EDGE,"E2.top");var subQ1=sQuery(id+"F2.wireOp",EDGE,"E2.right");Q75=makeQuery(id+"F3.boolean.opBoolean","SPLIT",EDGE,{"disambiguationData":[TD([makeQuery(id+"F1.opExtrude","CAP_FACE",FACE,{"disambiguationData":[OSD([sQuery(id+"F0.wireOp",EDGE,"E0.bottom"),sQuery(id+"F0.wireOp",EDGE,"E0.top"),sQuery(id+"F0.wireOp",EDGE,"E0.left"),sQuery(id+"F0.wireOp",EDGE,"E0.right")])],"isStart":false})])],"derivedFrom":makeQuery(id+"F3.opExtrude","SWEPT_EDGE",EDGE,{"disambiguationData":[OSD([subQ0,subQ1])]})});}
            var Q76;
            {var subQ0=sQuery(id+"F2.wireOp",EDGE,"E2.top");var subQ1=sQuery(id+"F2.wireOp",EDGE,"E2.left");Q76=makeQuery(id+"F3.boolean.opBoolean","SPLIT",EDGE,{"disambiguationData":[TD([makeQuery(id+"F1.opExtrude","CAP_FACE",FACE,{"disambiguationData":[OSD([sQuery(id+"F0.wireOp",EDGE,"E0.bottom"),sQuery(id+"F0.wireOp",EDGE,"E0.top"),sQuery(id+"F0.wireOp",EDGE,"E0.left"),sQuery(id+"F0.wireOp",EDGE,"E0.right")])],"isStart":false})])],"derivedFrom":makeQuery(id+"F3.opExtrude","SWEPT_EDGE",EDGE,{"disambiguationData":[OSD([subQ0,subQ1])]})});}
            var Q77;
            {var subQ0=sQuery(id+"F2.wireOp",EDGE,"E3.left");var subQ1=sQuery(id+"F2.wireOp",EDGE,"E3.top");Q77=makeQuery(id+"F3.boolean.opBoolean","SPLIT",EDGE,{"disambiguationData":[TD([makeQuery(id+"F1.opExtrude","CAP_FACE",FACE,{"disambiguationData":[OSD([sQuery(id+"F0.wireOp",EDGE,"E0.bottom"),sQuery(id+"F0.wireOp",EDGE,"E0.top"),sQuery(id+"F0.wireOp",EDGE,"E0.left"),sQuery(id+"F0.wireOp",EDGE,"E0.right")])],"isStart":true})])],"derivedFrom":makeQuery(id+"F3.opExtrude","SWEPT_EDGE",EDGE,{"disambiguationData":[OSD([subQ1,subQ0])]})});}
            var Q78;
            {var subQ0=sQuery(id+"F2.wireOp",EDGE,"E8.left");var subQ1=sQuery(id+"F2.wireOp",EDGE,"E8.bottom");Q78=makeQuery(id+"F3.boolean.opBoolean","SPLIT",EDGE,{"disambiguationData":[TD([makeQuery(id+"F1.opExtrude","CAP_FACE",FACE,{"disambiguationData":[OSD([sQuery(id+"F0.wireOp",EDGE,"E0.bottom"),sQuery(id+"F0.wireOp",EDGE,"E0.top"),sQuery(id+"F0.wireOp",EDGE,"E0.left"),sQuery(id+"F0.wireOp",EDGE,"E0.right")])],"isStart":true})])],"derivedFrom":makeQuery(id+"F3.opExtrude","SWEPT_EDGE",EDGE,{"disambiguationData":[OSD([subQ1,subQ0])]})});}
            var Q79;
            {var subQ0=sQuery(id+"F2.wireOp",EDGE,"E8.left");var subQ1=sQuery(id+"F2.wireOp",EDGE,"E8.top");Q79=makeQuery(id+"F3.boolean.opBoolean","SPLIT",EDGE,{"disambiguationData":[TD([makeQuery(id+"F1.opExtrude","CAP_FACE",FACE,{"disambiguationData":[OSD([sQuery(id+"F0.wireOp",EDGE,"E0.bottom"),sQuery(id+"F0.wireOp",EDGE,"E0.top"),sQuery(id+"F0.wireOp",EDGE,"E0.left"),sQuery(id+"F0.wireOp",EDGE,"E0.right")])],"isStart":true})])],"derivedFrom":makeQuery(id+"F3.opExtrude","SWEPT_EDGE",EDGE,{"disambiguationData":[OSD([subQ1,subQ0])]})});}
            var Q80;
            {var subQ0=sQuery(id+"F2.wireOp",EDGE,"E9.left");var subQ1=sQuery(id+"F2.wireOp",EDGE,"E9.top");Q80=makeQuery(id+"F3.boolean.opBoolean","SPLIT",EDGE,{"disambiguationData":[TD([makeQuery(id+"F1.opExtrude","CAP_FACE",FACE,{"disambiguationData":[OSD([sQuery(id+"F0.wireOp",EDGE,"E0.bottom"),sQuery(id+"F0.wireOp",EDGE,"E0.top"),sQuery(id+"F0.wireOp",EDGE,"E0.left"),sQuery(id+"F0.wireOp",EDGE,"E0.right")])],"isStart":true})])],"derivedFrom":makeQuery(id+"F3.opExtrude","SWEPT_EDGE",EDGE,{"disambiguationData":[OSD([subQ1,subQ0])]})});}
            var Q81;
            {var subQ0=sQuery(id+"F2.wireOp",EDGE,"E9.right");var subQ1=sQuery(id+"F2.wireOp",EDGE,"E9.top");Q81=makeQuery(id+"F3.boolean.opBoolean","SPLIT",EDGE,{"disambiguationData":[TD([makeQuery(id+"F1.opExtrude","CAP_FACE",FACE,{"disambiguationData":[OSD([sQuery(id+"F0.wireOp",EDGE,"E0.bottom"),sQuery(id+"F0.wireOp",EDGE,"E0.top"),sQuery(id+"F0.wireOp",EDGE,"E0.left"),sQuery(id+"F0.wireOp",EDGE,"E0.right")])],"isStart":true})])],"derivedFrom":makeQuery(id+"F3.opExtrude","SWEPT_EDGE",EDGE,{"disambiguationData":[OSD([subQ1,subQ0])]})});}
            var Q82;
            {var subQ0=sQuery(id+"F2.wireOp",EDGE,"E2.left");var subQ1=sQuery(id+"F2.wireOp",EDGE,"E2.top");Q82=makeQuery(id+"F3.boolean.opBoolean","SPLIT",EDGE,{"disambiguationData":[TD([makeQuery(id+"F1.opExtrude","CAP_FACE",FACE,{"disambiguationData":[OSD([sQuery(id+"F0.wireOp",EDGE,"E0.bottom"),sQuery(id+"F0.wireOp",EDGE,"E0.top"),sQuery(id+"F0.wireOp",EDGE,"E0.left"),sQuery(id+"F0.wireOp",EDGE,"E0.right")])],"isStart":true})])],"derivedFrom":makeQuery(id+"F3.opExtrude","SWEPT_EDGE",EDGE,{"disambiguationData":[OSD([subQ1,subQ0])]})});}
            var Q83;
            {var subQ0=sQuery(id+"F2.wireOp",EDGE,"E2.right");var subQ1=sQuery(id+"F2.wireOp",EDGE,"E2.top");Q83=makeQuery(id+"F3.boolean.opBoolean","SPLIT",EDGE,{"disambiguationData":[TD([makeQuery(id+"F1.opExtrude","CAP_FACE",FACE,{"disambiguationData":[OSD([sQuery(id+"F0.wireOp",EDGE,"E0.bottom"),sQuery(id+"F0.wireOp",EDGE,"E0.top"),sQuery(id+"F0.wireOp",EDGE,"E0.left"),sQuery(id+"F0.wireOp",EDGE,"E0.right")])],"isStart":true})])],"derivedFrom":makeQuery(id+"F3.opExtrude","SWEPT_EDGE",EDGE,{"disambiguationData":[OSD([subQ1,subQ0])]})});}
            var Q84;
            {var subQ0=sQuery(id+"F2.wireOp",EDGE,"E1.top");var subQ1=sQuery(id+"F2.wireOp",EDGE,"E1.right");Q84=makeQuery(id+"F3.boolean.opBoolean","SPLIT",EDGE,{"disambiguationData":[TD([makeQuery(id+"F1.opExtrude","CAP_FACE",FACE,{"disambiguationData":[OSD([sQuery(id+"F0.wireOp",EDGE,"E0.bottom"),sQuery(id+"F0.wireOp",EDGE,"E0.top"),sQuery(id+"F0.wireOp",EDGE,"E0.left"),sQuery(id+"F0.wireOp",EDGE,"E0.right")])],"isStart":true})])],"derivedFrom":makeQuery(id+"F3.opExtrude","SWEPT_EDGE",EDGE,{"disambiguationData":[OSD([subQ0,subQ1])]})});}
            var Q85;
            {var subQ0=sQuery(id+"F2.wireOp",EDGE,"E4.bottom");var subQ1=sQuery(id+"F2.wireOp",EDGE,"E4.right");Q85=makeQuery(id+"F3.boolean.opBoolean","SPLIT",EDGE,{"disambiguationData":[TD([makeQuery(id+"F1.opExtrude","CAP_FACE",FACE,{"disambiguationData":[OSD([sQuery(id+"F0.wireOp",EDGE,"E0.bottom"),sQuery(id+"F0.wireOp",EDGE,"E0.top"),sQuery(id+"F0.wireOp",EDGE,"E0.left"),sQuery(id+"F0.wireOp",EDGE,"E0.right")])],"isStart":true})])],"derivedFrom":makeQuery(id+"F3.opExtrude","SWEPT_EDGE",EDGE,{"disambiguationData":[OSD([subQ0,subQ1])]})});}
            var Q86;
            {var subQ0=sQuery(id+"F2.wireOp",EDGE,"E4.right");var subQ1=sQuery(id+"F2.wireOp",EDGE,"E4.top");Q86=makeQuery(id+"F3.boolean.opBoolean","SPLIT",EDGE,{"disambiguationData":[TD([makeQuery(id+"F1.opExtrude","CAP_FACE",FACE,{"disambiguationData":[OSD([sQuery(id+"F0.wireOp",EDGE,"E0.bottom"),sQuery(id+"F0.wireOp",EDGE,"E0.top"),sQuery(id+"F0.wireOp",EDGE,"E0.left"),sQuery(id+"F0.wireOp",EDGE,"E0.right")])],"isStart":true})])],"derivedFrom":makeQuery(id+"F3.opExtrude","SWEPT_EDGE",EDGE,{"disambiguationData":[OSD([subQ1,subQ0])]})});}
            var Q87;
            {var subQ0=sQuery(id+"F2.wireOp",EDGE,"E5.bottom");var subQ1=sQuery(id+"F2.wireOp",EDGE,"E5.right");Q87=makeQuery(id+"F3.boolean.opBoolean","SPLIT",EDGE,{"disambiguationData":[TD([makeQuery(id+"F1.opExtrude","CAP_FACE",FACE,{"disambiguationData":[OSD([sQuery(id+"F0.wireOp",EDGE,"E0.bottom"),sQuery(id+"F0.wireOp",EDGE,"E0.top"),sQuery(id+"F0.wireOp",EDGE,"E0.left"),sQuery(id+"F0.wireOp",EDGE,"E0.right")])],"isStart":true})])],"derivedFrom":makeQuery(id+"F3.opExtrude","SWEPT_EDGE",EDGE,{"disambiguationData":[OSD([subQ0,subQ1])]})});}
            var Q88;
            {var subQ0=sQuery(id+"F2.wireOp",EDGE,"E6.bottom");var subQ1=sQuery(id+"F2.wireOp",EDGE,"E6.left");Q88=makeQuery(id+"F3.boolean.opBoolean","SPLIT",EDGE,{"disambiguationData":[TD([makeQuery(id+"F1.opExtrude","CAP_FACE",FACE,{"disambiguationData":[OSD([sQuery(id+"F0.wireOp",EDGE,"E0.bottom"),sQuery(id+"F0.wireOp",EDGE,"E0.top"),sQuery(id+"F0.wireOp",EDGE,"E0.left"),sQuery(id+"F0.wireOp",EDGE,"E0.right")])],"isStart":true})])],"derivedFrom":makeQuery(id+"F3.opExtrude","SWEPT_EDGE",EDGE,{"disambiguationData":[OSD([subQ0,subQ1])]})});}
            var Q89;
            {var subQ0=sQuery(id+"F2.wireOp",EDGE,"E6.bottom");var subQ1=sQuery(id+"F2.wireOp",EDGE,"E6.right");Q89=makeQuery(id+"F3.boolean.opBoolean","SPLIT",EDGE,{"disambiguationData":[TD([makeQuery(id+"F1.opExtrude","CAP_FACE",FACE,{"disambiguationData":[OSD([sQuery(id+"F0.wireOp",EDGE,"E0.bottom"),sQuery(id+"F0.wireOp",EDGE,"E0.top"),sQuery(id+"F0.wireOp",EDGE,"E0.left"),sQuery(id+"F0.wireOp",EDGE,"E0.right")])],"isStart":true})])],"derivedFrom":makeQuery(id+"F3.opExtrude","SWEPT_EDGE",EDGE,{"disambiguationData":[OSD([subQ0,subQ1])]})});}
            var Q90;
            {var subQ0=sQuery(id+"F2.wireOp",EDGE,"E10.left");var subQ1=sQuery(id+"F2.wireOp",EDGE,"E10.bottom");Q90=makeQuery(id+"F3.boolean.opBoolean","SPLIT",EDGE,{"disambiguationData":[TD([makeQuery(id+"F1.opExtrude","CAP_FACE",FACE,{"disambiguationData":[OSD([sQuery(id+"F0.wireOp",EDGE,"E0.bottom"),sQuery(id+"F0.wireOp",EDGE,"E0.top"),sQuery(id+"F0.wireOp",EDGE,"E0.left"),sQuery(id+"F0.wireOp",EDGE,"E0.right")])],"isStart":true})])],"derivedFrom":makeQuery(id+"F3.opExtrude","SWEPT_EDGE",EDGE,{"disambiguationData":[OSD([subQ1,subQ0])]})});}
            var Q91;
            {var subQ0=sQuery(id+"F2.wireOp",EDGE,"E10.bottom");var subQ1=sQuery(id+"F2.wireOp",EDGE,"E10.right");Q91=makeQuery(id+"F3.boolean.opBoolean","SPLIT",EDGE,{"disambiguationData":[TD([makeQuery(id+"F1.opExtrude","CAP_FACE",FACE,{"disambiguationData":[OSD([sQuery(id+"F0.wireOp",EDGE,"E0.bottom"),sQuery(id+"F0.wireOp",EDGE,"E0.top"),sQuery(id+"F0.wireOp",EDGE,"E0.left"),sQuery(id+"F0.wireOp",EDGE,"E0.right")])],"isStart":true})])],"derivedFrom":makeQuery(id+"F3.opExtrude","SWEPT_EDGE",EDGE,{"disambiguationData":[OSD([subQ0,subQ1])]})});}
            var Q92;
            {var subQ0=sQuery(id+"F2.wireOp",EDGE,"E7.bottom");var subQ1=sQuery(id+"F2.wireOp",EDGE,"E7.left");Q92=makeQuery(id+"F3.boolean.opBoolean","SPLIT",EDGE,{"disambiguationData":[TD([makeQuery(id+"F1.opExtrude","CAP_FACE",FACE,{"disambiguationData":[OSD([sQuery(id+"F0.wireOp",EDGE,"E0.bottom"),sQuery(id+"F0.wireOp",EDGE,"E0.top"),sQuery(id+"F0.wireOp",EDGE,"E0.left"),sQuery(id+"F0.wireOp",EDGE,"E0.right")])],"isStart":true})])],"derivedFrom":makeQuery(id+"F3.opExtrude","SWEPT_EDGE",EDGE,{"disambiguationData":[OSD([subQ0,subQ1])]})});}
            var Q93;
            Q93=makeQuery(id+"F3.opExtrude","CAP_FACE",FACE,{"disambiguationData":[OSD([sQuery(id+"F2.wireOp",EDGE,"E4.bottom"),sQuery(id+"F2.wireOp",EDGE,"E4.top"),sQuery(id+"F2.wireOp",EDGE,"E4.left"),sQuery(id+"F2.wireOp",EDGE,"E4.right")])],"isStart":false});
            var Q94;
            Q94=makeQuery(id+"F3.opExtrude","CAP_EDGE",EDGE,{"disambiguationData":[OSD([sQuery(id+"F2.wireOp",EDGE,"E10.left")])],"isStart":false});
            var Q95;
            Q95=makeQuery(id+"F3.opExtrude","CAP_EDGE",EDGE,{"disambiguationData":[OSD([sQuery(id+"F2.wireOp",EDGE,"E10.right")])],"isStart":false});
            var Q96;
            Q96=makeQuery(id+"F3.opExtrude","CAP_EDGE",EDGE,{"disambiguationData":[OSD([sQuery(id+"F2.wireOp",EDGE,"E10.top")])],"isStart":false});
            var Q97;
            Q97=makeQuery(id+"F3.opExtrude","CAP_EDGE",EDGE,{"disambiguationData":[OSD([sQuery(id+"F2.wireOp",EDGE,"E6.top")])],"isStart":false});
            var Q98;
            Q98=makeQuery(id+"F3.opExtrude","CAP_EDGE",EDGE,{"disambiguationData":[OSD([sQuery(id+"F2.wireOp",EDGE,"E10.right")])],"isStart":true});
            var Q99;
            Q99=makeQuery(id+"F3.opExtrude","CAP_EDGE",EDGE,{"disambiguationData":[OSD([sQuery(id+"F2.wireOp",EDGE,"E6.top")])],"isStart":true});
            var Q100;
            Q100=makeQuery(id+"F3.opExtrude","CAP_EDGE",EDGE,{"disambiguationData":[OSD([sQuery(id+"F2.wireOp",EDGE,"E10.top")])],"isStart":true});
            var Q101;
            {var subQ0=sQuery(id+"F2.wireOp",EDGE,"E6.top");var subQ1=sQuery(id+"F0.wireOp",EDGE,"E0.top");var subQ2=sQuery(id+"F2.wireOp",EDGE,"E6.right");Q101=makeQuery(id+"F3.boolean.opBoolean","SPLIT",EDGE,{"disambiguationData":[TD([makeQuery(id+"F1.opExtrude","CAP_FACE",FACE,{"disambiguationData":[OSD([sQuery(id+"F0.wireOp",EDGE,"E0.bottom"),subQ1,sQuery(id+"F0.wireOp",EDGE,"E0.left"),sQuery(id+"F0.wireOp",EDGE,"E0.right")])],"isStart":false})])],"derivedFrom":makeQuery(id+"F3.opExtrude","SWEPT_EDGE",EDGE,{"disambiguationData":[OSD([subQ0,subQ2])]})});}
            var Q102;
            {var subQ0=sQuery(id+"F2.wireOp",EDGE,"E6.top");var subQ1=sQuery(id+"F0.wireOp",EDGE,"E0.top");var subQ2=sQuery(id+"F2.wireOp",EDGE,"E6.right");Q102=makeQuery(id+"F3.boolean.opBoolean","SPLIT",EDGE,{"disambiguationData":[TD([makeQuery(id+"F1.opExtrude","CAP_FACE",FACE,{"disambiguationData":[OSD([sQuery(id+"F0.wireOp",EDGE,"E0.bottom"),subQ1,sQuery(id+"F0.wireOp",EDGE,"E0.left"),sQuery(id+"F0.wireOp",EDGE,"E0.right")])],"isStart":true})])],"derivedFrom":makeQuery(id+"F3.opExtrude","SWEPT_EDGE",EDGE,{"disambiguationData":[OSD([subQ0,subQ2])]})});}
            var Q103;
            {var subQ0=sQuery(id+"F2.wireOp",EDGE,"E4.bottom");var subQ1=sQuery(id+"F2.wireOp",EDGE,"E4.right");Q103=makeQuery(id+"F3.boolean.opBoolean","SPLIT",EDGE,{"disambiguationData":[TD([makeQuery(id+"F1.opExtrude","CAP_FACE",FACE,{"disambiguationData":[OSD([sQuery(id+"F0.wireOp",EDGE,"E0.bottom"),sQuery(id+"F0.wireOp",EDGE,"E0.top"),sQuery(id+"F0.wireOp",EDGE,"E0.left"),sQuery(id+"F0.wireOp",EDGE,"E0.right")])],"isStart":false})])],"derivedFrom":makeQuery(id+"F3.opExtrude","SWEPT_EDGE",EDGE,{"disambiguationData":[OSD([subQ0,subQ1])]})});}
            var Q104;
            Q104=makeQuery(id+"F18.boolean.opBoolean","INTERSECT",EDGE,{"derivedFrom":[makeQuery(id+"F3.opExtrude","CAP_FACE",FACE,{"disambiguationData":[OSD([sQuery(id+"F2.wireOp",EDGE,"E8.bottom"),sQuery(id+"F2.wireOp",EDGE,"E8.top"),sQuery(id+"F2.wireOp",EDGE,"E8.left"),sQuery(id+"F2.wireOp",EDGE,"E8.right")])],"isStart":false}),makeQuery(id+"F18.opExtrude","SWEPT_FACE",FACE,{"disambiguationData":[OSD([sQuery(id+"F17.wireOp",EDGE,"E28")])]})]});
            var Q105;
            Q105=makeQuery(id+"F18.boolean.opBoolean","INTERSECT",EDGE,{"derivedFrom":[makeQuery(id+"F3.opExtrude","SWEPT_FACE",FACE,{"disambiguationData":[OSD([sQuery(id+"F2.wireOp",EDGE,"E8.bottom")])]}),makeQuery(id+"F18.opExtrude","SWEPT_FACE",FACE,{"disambiguationData":[OSD([sQuery(id+"F17.wireOp",EDGE,"E28")])]})]});
            fillet(context, id + "F21", {"entities" : qUnion([Q0, Q1, Q2, Q3, Q4, Q5, Q6, Q7, Q8, Q9, Q10, Q11, Q12, Q13, Q14, Q15, Q16, Q17, Q18, Q19, Q20, Q21, Q22, Q23, Q24, Q25, Q26, Q27, Q28, Q29, Q30, Q31, Q32, Q33, Q34, Q35, Q36, Q37, Q38, Q39, Q40, Q41, Q42, Q43, Q44, Q45, Q46, Q47, Q48, Q49, Q50, Q51, Q52, Q53, Q54, Q55, Q56, Q57, Q58, Q59, Q60, Q61, Q62, Q63, Q64, Q65, Q66, Q67, Q68, Q69, Q70, Q71, Q72, Q73, Q74, Q75, Q76, Q77, Q78, Q79, Q80, Q81, Q82, Q83, Q84, Q85, Q86, Q87, Q88, Q89, Q90, Q91, Q92, Q93, Q94, Q95, Q96, Q97, Q98, Q99, Q100, Q101, Q102, Q103, Q104, Q105]), "radius" : 1 * mm, "tangentPropagation" : true, "allowEdgeOverflow" : false});
        }
        {
            var Q0;
            {var subQ0=sQuery(id+"F0.wireOp",EDGE,"E0.bottom");Q0=makeQuery(id+"F3.boolean.opBoolean","SPLIT",EDGE,{"disambiguationData":[TD([makeQuery(id+"F3.opExtrude","SWEPT_FACE",FACE,{"disambiguationData":[OSD([sQuery(id+"F2.wireOp",EDGE,"E2.right")])]})])],"derivedFrom":makeQuery(id+"F1.opExtrude","CAP_EDGE",EDGE,{"disambiguationData":[OSD([subQ0])],"isStart":false})});}
            var Q1;
            {var subQ0=sQuery(id+"F0.wireOp",EDGE,"E0.bottom");Q1=makeQuery(id+"F3.boolean.opBoolean","SPLIT",EDGE,{"disambiguationData":[TD([makeQuery(id+"F3.opExtrude","SWEPT_FACE",FACE,{"disambiguationData":[OSD([sQuery(id+"F2.wireOp",EDGE,"E3.left")])]})])],"derivedFrom":makeQuery(id+"F1.opExtrude","CAP_EDGE",EDGE,{"disambiguationData":[OSD([subQ0])],"isStart":false})});}
            var Q2;
            {var subQ0=sQuery(id+"F0.wireOp",EDGE,"E0.bottom");Q2=makeQuery(id+"F3.boolean.opBoolean","SPLIT",EDGE,{"disambiguationData":[TD([makeQuery(id+"F3.opExtrude","SWEPT_FACE",FACE,{"disambiguationData":[OSD([sQuery(id+"F2.wireOp",EDGE,"E1.right")])]})])],"derivedFrom":makeQuery(id+"F1.opExtrude","CAP_EDGE",EDGE,{"disambiguationData":[OSD([subQ0])],"isStart":false})});}
            var Q3;
            {var subQ0=sQuery(id+"F0.wireOp",EDGE,"E0.left");Q3=makeQuery(id+"F3.boolean.opBoolean","SPLIT",EDGE,{"disambiguationData":[TD([makeQuery(id+"F3.opExtrude","SWEPT_FACE",FACE,{"disambiguationData":[OSD([sQuery(id+"F2.wireOp",EDGE,"E1.top")])]})])],"derivedFrom":makeQuery(id+"F1.opExtrude","CAP_EDGE",EDGE,{"disambiguationData":[OSD([subQ0])],"isStart":false})});}
            var Q4;
            {var subQ0=sQuery(id+"F0.wireOp",EDGE,"E0.left");Q4=makeQuery(id+"F3.boolean.opBoolean","SPLIT",EDGE,{"disambiguationData":[TD([makeQuery(id+"F3.opExtrude","SWEPT_FACE",FACE,{"disambiguationData":[OSD([sQuery(id+"F2.wireOp",EDGE,"E4.top")])]})])],"derivedFrom":makeQuery(id+"F1.opExtrude","CAP_EDGE",EDGE,{"disambiguationData":[OSD([subQ0])],"isStart":false})});}
            var Q5;
            {var subQ0=sQuery(id+"F0.wireOp",EDGE,"E0.right");Q5=makeQuery(id+"F3.boolean.opBoolean","SPLIT",EDGE,{"disambiguationData":[TD([makeQuery(id+"F3.opExtrude","SWEPT_FACE",FACE,{"disambiguationData":[OSD([sQuery(id+"F2.wireOp",EDGE,"E3.top")])]})])],"derivedFrom":makeQuery(id+"F1.opExtrude","CAP_EDGE",EDGE,{"disambiguationData":[OSD([subQ0])],"isStart":false})});}
            var Q6;
            {var subQ0=sQuery(id+"F0.wireOp",EDGE,"E0.right");Q6=makeQuery(id+"F3.boolean.opBoolean","SPLIT",EDGE,{"disambiguationData":[TD([makeQuery(id+"F3.opExtrude","SWEPT_FACE",FACE,{"disambiguationData":[OSD([sQuery(id+"F2.wireOp",EDGE,"E7.bottom")])]})])],"derivedFrom":makeQuery(id+"F1.opExtrude","CAP_EDGE",EDGE,{"disambiguationData":[OSD([subQ0])],"isStart":false})});}
            var Q7;
            {var subQ0=sQuery(id+"F0.wireOp",EDGE,"E0.right");Q7=makeQuery(id+"F3.boolean.opBoolean","SPLIT",EDGE,{"disambiguationData":[TD([makeQuery(id+"F3.opExtrude","SWEPT_FACE",FACE,{"disambiguationData":[OSD([sQuery(id+"F2.wireOp",EDGE,"E7.bottom")])]})])],"derivedFrom":makeQuery(id+"F1.opExtrude","CAP_EDGE",EDGE,{"disambiguationData":[OSD([subQ0])],"isStart":true})});}
            var Q8;
            {var subQ0=sQuery(id+"F0.wireOp",EDGE,"E0.right");Q8=makeQuery(id+"F3.boolean.opBoolean","SPLIT",EDGE,{"disambiguationData":[TD([makeQuery(id+"F3.opExtrude","SWEPT_FACE",FACE,{"disambiguationData":[OSD([sQuery(id+"F2.wireOp",EDGE,"E3.top")])]})])],"derivedFrom":makeQuery(id+"F1.opExtrude","CAP_EDGE",EDGE,{"disambiguationData":[OSD([subQ0])],"isStart":true})});}
            var Q9;
            {var subQ0=sQuery(id+"F0.wireOp",EDGE,"E0.bottom");Q9=makeQuery(id+"F3.boolean.opBoolean","SPLIT",EDGE,{"disambiguationData":[TD([makeQuery(id+"F3.opExtrude","SWEPT_FACE",FACE,{"disambiguationData":[OSD([sQuery(id+"F2.wireOp",EDGE,"E3.left")])]})])],"derivedFrom":makeQuery(id+"F1.opExtrude","CAP_EDGE",EDGE,{"disambiguationData":[OSD([subQ0])],"isStart":true})});}
            var Q10;
            {var subQ0=sQuery(id+"F0.wireOp",EDGE,"E0.bottom");Q10=makeQuery(id+"F3.boolean.opBoolean","SPLIT",EDGE,{"disambiguationData":[TD([makeQuery(id+"F3.opExtrude","SWEPT_FACE",FACE,{"disambiguationData":[OSD([sQuery(id+"F2.wireOp",EDGE,"E2.right")])]})])],"derivedFrom":makeQuery(id+"F1.opExtrude","CAP_EDGE",EDGE,{"disambiguationData":[OSD([subQ0])],"isStart":true})});}
            var Q11;
            {var subQ0=sQuery(id+"F0.wireOp",EDGE,"E0.bottom");Q11=makeQuery(id+"F3.boolean.opBoolean","SPLIT",EDGE,{"disambiguationData":[TD([makeQuery(id+"F3.opExtrude","SWEPT_FACE",FACE,{"disambiguationData":[OSD([sQuery(id+"F2.wireOp",EDGE,"E1.right")])]})])],"derivedFrom":makeQuery(id+"F1.opExtrude","CAP_EDGE",EDGE,{"disambiguationData":[OSD([subQ0])],"isStart":true})});}
            var Q12;
            {var subQ0=sQuery(id+"F0.wireOp",EDGE,"E0.left");Q12=makeQuery(id+"F3.boolean.opBoolean","SPLIT",EDGE,{"disambiguationData":[TD([makeQuery(id+"F3.opExtrude","SWEPT_FACE",FACE,{"disambiguationData":[OSD([sQuery(id+"F2.wireOp",EDGE,"E1.top")])]})])],"derivedFrom":makeQuery(id+"F1.opExtrude","CAP_EDGE",EDGE,{"disambiguationData":[OSD([subQ0])],"isStart":true})});}
            var Q13;
            {var subQ0=sQuery(id+"F0.wireOp",EDGE,"E0.left");Q13=makeQuery(id+"F3.boolean.opBoolean","SPLIT",EDGE,{"disambiguationData":[TD([makeQuery(id+"F3.opExtrude","SWEPT_FACE",FACE,{"disambiguationData":[OSD([sQuery(id+"F2.wireOp",EDGE,"E4.top")])]})])],"derivedFrom":makeQuery(id+"F1.opExtrude","CAP_EDGE",EDGE,{"disambiguationData":[OSD([subQ0])],"isStart":true})});}
            var Q14;
            {var subQ0=sQuery(id+"F0.wireOp",EDGE,"E0.top");Q14=makeQuery(id+"F3.boolean.opBoolean","SPLIT",EDGE,{"disambiguationData":[TD([makeQuery(id+"F3.opExtrude","SWEPT_FACE",FACE,{"disambiguationData":[OSD([sQuery(id+"F2.wireOp",EDGE,"E5.right")])]})])],"derivedFrom":makeQuery(id+"F1.opExtrude","CAP_EDGE",EDGE,{"disambiguationData":[OSD([subQ0])],"isStart":true})});}
            var Q15;
            {var subQ0=sQuery(id+"F0.wireOp",EDGE,"E0.top");Q15=makeQuery(id+"F3.boolean.opBoolean","SPLIT",EDGE,{"disambiguationData":[TD([makeQuery(id+"F3.opExtrude","SWEPT_FACE",FACE,{"disambiguationData":[OSD([sQuery(id+"F2.wireOp",EDGE,"E6.right")])]})])],"derivedFrom":makeQuery(id+"F1.opExtrude","CAP_EDGE",EDGE,{"disambiguationData":[OSD([subQ0])],"isStart":true})});}
            var Q16;
            {var subQ0=sQuery(id+"F0.wireOp",EDGE,"E0.top");Q16=makeQuery(id+"F3.boolean.opBoolean","SPLIT",EDGE,{"disambiguationData":[TD([makeQuery(id+"F3.opExtrude","SWEPT_FACE",FACE,{"disambiguationData":[OSD([sQuery(id+"F2.wireOp",EDGE,"E7.left")])]})])],"derivedFrom":makeQuery(id+"F1.opExtrude","CAP_EDGE",EDGE,{"disambiguationData":[OSD([subQ0])],"isStart":true})});}
            var Q17;
            {var subQ0=sQuery(id+"F0.wireOp",EDGE,"E0.top");Q17=makeQuery(id+"F3.boolean.opBoolean","SPLIT",EDGE,{"disambiguationData":[TD([makeQuery(id+"F3.opExtrude","SWEPT_FACE",FACE,{"disambiguationData":[OSD([sQuery(id+"F2.wireOp",EDGE,"E7.left")])]})])],"derivedFrom":makeQuery(id+"F1.opExtrude","CAP_EDGE",EDGE,{"disambiguationData":[OSD([subQ0])],"isStart":false})});}
            var Q18;
            {var subQ0=sQuery(id+"F0.wireOp",EDGE,"E0.top");Q18=makeQuery(id+"F3.boolean.opBoolean","SPLIT",EDGE,{"disambiguationData":[TD([makeQuery(id+"F3.opExtrude","SWEPT_FACE",FACE,{"disambiguationData":[OSD([sQuery(id+"F2.wireOp",EDGE,"E6.right")])]})])],"derivedFrom":makeQuery(id+"F1.opExtrude","CAP_EDGE",EDGE,{"disambiguationData":[OSD([subQ0])],"isStart":false})});}
            var Q19;
            {var subQ0=sQuery(id+"F0.wireOp",EDGE,"E0.top");Q19=makeQuery(id+"F3.boolean.opBoolean","SPLIT",EDGE,{"disambiguationData":[TD([makeQuery(id+"F3.opExtrude","SWEPT_FACE",FACE,{"disambiguationData":[OSD([sQuery(id+"F2.wireOp",EDGE,"E5.right")])]})])],"derivedFrom":makeQuery(id+"F1.opExtrude","CAP_EDGE",EDGE,{"disambiguationData":[OSD([subQ0])],"isStart":false})});}
            fillet(context, id + "F22", {"entities" : qUnion([Q0, Q1, Q2, Q3, Q4, Q5, Q6, Q7, Q8, Q9, Q10, Q11, Q12, Q13, Q14, Q15, Q16, Q17, Q18, Q19]), "radius" : 1 * mm, "tangentPropagation" : true, "allowEdgeOverflow" : false});
        }
        {
            var Q0;
            {var subQ3=sQuery(id+"F0.wireOp",EDGE,"E0.bottom");Q0=makeQuery(id+"F3.boolean.opBoolean","SPLIT",FACE,{"disambiguationData":[TD([makeQuery(id+"F3.opExtrude","SWEPT_FACE",FACE,{"disambiguationData":[OSD([sQuery(id+"F2.wireOp",EDGE,"E2.right")])]})])],"derivedFrom":makeQuery(id+"F1.opExtrude","SWEPT_FACE",FACE,{"disambiguationData":[OSD([subQ3])]})});}
            var sketch = newSketch(context, id + "F23", { "sketchPlane" : qUnion([Q0])});
            skLineSegment(sketch, "E29.bottom", {"start": v(-15, -14) * mm, "end": v(5, -14) * mm});
            skLineSegment(sketch, "E29.top", {"start": v(-15, -17) * mm, "end": v(5, -17) * mm});
            skLineSegment(sketch, "E29.left", {"start": v(-15, -14) * mm, "end": v(-15, -17) * mm});
            skLineSegment(sketch, "E29.right", {"start": v(5, -14) * mm, "end": v(5, -17) * mm});
            skSolve(sketch);
        }
        {
            var Q0;
            {var subQ0=sQuery(id+"F0.wireOp",EDGE,"E0.right");var subQ1=sQuery(id+"F0.wireOp",EDGE,"E0.bottom");var subQ2=sQuery(id+"F0.wireOp",EDGE,"E0.top");var subQ3=sQuery(id+"F0.wireOp",EDGE,"E0.left");Q0=makeQuery(id+"F18.boolean.opBoolean","MERGE",FACE,{"derivedFrom":[makeQuery(id+"F16.boolean.opBoolean","SPLIT",FACE,{"disambiguationData":[TD([makeQuery(id+"F1.opExtrude","SWEPT_FACE",FACE,{"disambiguationData":[OSD([subQ1])]}),makeQuery(id+"F1.opExtrude","SWEPT_FACE",FACE,{"disambiguationData":[OSD([subQ2])]}),makeQuery(id+"F1.opExtrude","SWEPT_FACE",FACE,{"disambiguationData":[OSD([subQ3])]}),makeQuery(id+"F1.opExtrude","SWEPT_FACE",FACE,{"disambiguationData":[OSD([subQ0])]}),makeQuery(id+"F3.opExtrude","SWEPT_FACE",FACE,{"disambiguationData":[OSD([sQuery(id+"F2.wireOp",EDGE,"E1.top")])]}),makeQuery(id+"F3.opExtrude","SWEPT_FACE",FACE,{"disambiguationData":[OSD([sQuery(id+"F2.wireOp",EDGE,"E1.right")])]}),makeQuery(id+"F3.opExtrude","SWEPT_FACE",FACE,{"disambiguationData":[OSD([sQuery(id+"F2.wireOp",EDGE,"E2.top")])]}),makeQuery(id+"F3.opExtrude","SWEPT_FACE",FACE,{"disambiguationData":[OSD([sQuery(id+"F2.wireOp",EDGE,"E2.left")])]}),makeQuery(id+"F3.opExtrude","SWEPT_FACE",FACE,{"disambiguationData":[OSD([sQuery(id+"F2.wireOp",EDGE,"E2.right")])]}),makeQuery(id+"F3.opExtrude","SWEPT_FACE",FACE,{"disambiguationData":[OSD([sQuery(id+"F2.wireOp",EDGE,"E3.top")])]}),makeQuery(id+"F3.opExtrude","SWEPT_FACE",FACE,{"disambiguationData":[OSD([sQuery(id+"F2.wireOp",EDGE,"E3.left")])]}),makeQuery(id+"F3.opExtrude","SWEPT_FACE",FACE,{"disambiguationData":[OSD([sQuery(id+"F2.wireOp",EDGE,"E4.bottom")])]}),makeQuery(id+"F3.opExtrude","SWEPT_FACE",FACE,{"disambiguationData":[OSD([sQuery(id+"F2.wireOp",EDGE,"E4.top")])]}),makeQuery(id+"F3.opExtrude","SWEPT_FACE",FACE,{"disambiguationData":[OSD([sQuery(id+"F2.wireOp",EDGE,"E4.right")])]}),makeQuery(id+"F3.opExtrude","SWEPT_FACE",FACE,{"disambiguationData":[OSD([sQuery(id+"F2.wireOp",EDGE,"E5.bottom")])]}),makeQuery(id+"F3.opExtrude","SWEPT_FACE",FACE,{"disambiguationData":[OSD([sQuery(id+"F2.wireOp",EDGE,"E5.right")])]}),makeQuery(id+"F3.opExtrude","SWEPT_FACE",FACE,{"disambiguationData":[OSD([sQuery(id+"F2.wireOp",EDGE,"E6.bottom")])]}),makeQuery(id+"F3.opExtrude","SWEPT_FACE",FACE,{"disambiguationData":[OSD([sQuery(id+"F2.wireOp",EDGE,"E6.top")])]}),makeQuery(id+"F3.opExtrude","SWEPT_FACE",FACE,{"disambiguationData":[OSD([sQuery(id+"F2.wireOp",EDGE,"E6.left")])]}),makeQuery(id+"F3.opExtrude","SWEPT_FACE",FACE,{"disambiguationData":[OSD([sQuery(id+"F2.wireOp",EDGE,"E6.right")])]}),makeQuery(id+"F3.opExtrude","SWEPT_FACE",FACE,{"disambiguationData":[OSD([sQuery(id+"F2.wireOp",EDGE,"E7.bottom")])]}),makeQuery(id+"F3.opExtrude","SWEPT_FACE",FACE,{"disambiguationData":[OSD([sQuery(id+"F2.wireOp",EDGE,"E7.left")])]}),makeQuery(id+"F3.opExtrude","SWEPT_FACE",FACE,{"disambiguationData":[OSD([sQuery(id+"F2.wireOp",EDGE,"E8.bottom")])]}),makeQuery(id+"F3.opExtrude","SWEPT_FACE",FACE,{"disambiguationData":[OSD([sQuery(id+"F2.wireOp",EDGE,"E8.top")])]}),makeQuery(id+"F3.opExtrude","SWEPT_FACE",FACE,{"disambiguationData":[OSD([sQuery(id+"F2.wireOp",EDGE,"E8.left")])]}),makeQuery(id+"F3.opExtrude","SWEPT_FACE",FACE,{"disambiguationData":[OSD([sQuery(id+"F2.wireOp",EDGE,"E9.top")])]}),makeQuery(id+"F3.opExtrude","SWEPT_FACE",FACE,{"disambiguationData":[OSD([sQuery(id+"F2.wireOp",EDGE,"E9.left")])]}),makeQuery(id+"F3.opExtrude","SWEPT_FACE",FACE,{"disambiguationData":[OSD([sQuery(id+"F2.wireOp",EDGE,"E9.right")])]}),makeQuery(id+"F3.opExtrude","SWEPT_FACE",FACE,{"disambiguationData":[OSD([sQuery(id+"F2.wireOp",EDGE,"E10.bottom")])]}),makeQuery(id+"F3.opExtrude","SWEPT_FACE",FACE,{"disambiguationData":[OSD([sQuery(id+"F2.wireOp",EDGE,"E10.top")])]}),makeQuery(id+"F3.opExtrude","SWEPT_FACE",FACE,{"disambiguationData":[OSD([sQuery(id+"F2.wireOp",EDGE,"E10.left")])]}),makeQuery(id+"F3.opExtrude","SWEPT_FACE",FACE,{"disambiguationData":[OSD([sQuery(id+"F2.wireOp",EDGE,"E10.right")])]}),makeQuery(id+"F8.boolean.opBoolean","COPY",FACE,{"derivedFrom":makeQuery(id+"F8.opExtrude","SWEPT_FACE",FACE,{"disambiguationData":[OSD([sQuery(id+"F7.wireOp",EDGE,"E12")])]})}),makeQuery(id+"F8.boolean.opBoolean","COPY",FACE,{"derivedFrom":makeQuery(id+"F8.opExtrude","SWEPT_FACE",FACE,{"disambiguationData":[OSD([sQuery(id+"F7.wireOp",EDGE,"E13")])]})}),makeQuery(id+"F16.opExtrude","SWEPT_FACE",FACE,{"disambiguationData":[OSD([sQuery(id+"F15.wireOp",EDGE,"E18")])]}),makeQuery(id+"F16.opExtrude","SWEPT_FACE",FACE,{"disambiguationData":[OSD([sQuery(id+"F15.wireOp",EDGE,"E19")])]}),makeQuery(id+"F16.opExtrude","SWEPT_FACE",FACE,{"disambiguationData":[OSD([sQuery(id+"F15.wireOp",EDGE,"E21")])]}),makeQuery(id+"F16.opExtrude","SWEPT_FACE",FACE,{"disambiguationData":[OSD([sQuery(id+"F15.wireOp",EDGE,"E22")])]}),makeQuery(id+"F16.opExtrude","SWEPT_FACE",FACE,{"disambiguationData":[OSD([sQuery(id+"F15.wireOp",EDGE,"E23")])]}),makeQuery(id+"F16.opExtrude","SWEPT_FACE",FACE,{"disambiguationData":[OSD([sQuery(id+"F15.wireOp",EDGE,"E26.trimOffspring")])]}),makeQuery(id+"F16.opExtrude","SWEPT_FACE",FACE,{"disambiguationData":[OSD([sQuery(id+"F15.wireOp",EDGE,"E27.trimOffspring")])]})])],"derivedFrom":makeQuery(id+"F1.opExtrude","CAP_FACE",FACE,{"disambiguationData":[OSD([subQ1,subQ2,subQ3,subQ0])],"isStart":false})}),makeQuery(id+"F18.opExtrude","CAP_FACE",FACE,{"disambiguationData":[OSD([sQuery(id+"F17.wireOp",EDGE,"E28")])],"isStart":false})]});}
            var sketch = newSketch(context, id + "F24", { "sketchPlane" : qUnion([Q0])});
            skArc(sketch, "E30", {"start": v(-1, -3.6) * mm, "mid": v(14.15, -12.35) * mm, "end": v(29.3, -3.6) * mm});
            skLineSegment(sketch, "E31", {"start": v(1.38, 12.53) * mm, "end": v(-1, 13.9) * mm});
            skLineSegment(sketch, "E32", {"start": v(-1, 13.9) * mm, "end": v(1.38, 12.53) * mm});
            skLineSegment(sketch, "E33", {"start": v(26.92, 12.53) * mm, "end": v(29.3, 13.9) * mm});
            skLineSegment(sketch, "E34", {"start": v(26.92, -2.23) * mm, "end": v(29.3, -3.6) * mm});
            skLineSegment(sketch, "E35", {"start": v(1.38, -2.23) * mm, "end": v(-1, -3.6) * mm});
            skArc(sketch, "E36", {"start": v(1.38, -2.22) * mm, "mid": v(14.15, -9.6) * mm, "end": v(26.92, -2.22) * mm});
            skArc(sketch, "E37.trimOffspring", {"start": v(26.92, 12.53) * mm, "mid": v(14.15, 19.9) * mm, "end": v(1.38, 12.53) * mm});
            skArc(sketch, "E38.trimOffspring", {"start": v(29.3, 13.9) * mm, "mid": v(14.15, 22.65) * mm, "end": v(-1, 13.9) * mm});
            skSolve(sketch);
        }
        {
            var Q0;
            Q0 = qSketchRegion(id + "F24", true);
            var Q1;
            {var subQ0=sQuery(id+"F15.wireOp",EDGE,"E27.trimOffspring");var subQ3=sQuery(id+"F2.wireOp",EDGE,"E8.top");Q1=makeQuery(id+"F16.boolean.opBoolean","SPLIT",FACE,{"disambiguationData":[TD([makeQuery(id+"F3.opExtrude","SWEPT_FACE",FACE,{"disambiguationData":[OSD([subQ3])]})])],"derivedFrom":makeQuery(id+"F16.opExtrude","SWEPT_FACE",FACE,{"disambiguationData":[OSD([subQ0])]})});}
            extrude(context, id + "F25", {"entities" : qUnion([Q0]), "operationType" : NewBodyOperationType.ADD, "endBound" : BoundingType.UP_TO_SURFACE, "depth" : 25 * mm, "endBoundEntityFace" : qUnion([Q1]), "offsetDistance" : 25 * mm});
        }
        {
            var Q0;
            Q0=makeQuery(id+"F25.boolean.opBoolean","SPLIT",FACE,{"derivedFrom":makeQuery(id+"F25.opExtrude","CAP_FACE",FACE,{"disambiguationData":[OSD([sQuery(id+"F24.wireOp",EDGE,"E32"),sQuery(id+"F24.wireOp",EDGE,"E33"),sQuery(id+"F24.wireOp",EDGE,"E37.trimOffspring"),sQuery(id+"F24.wireOp",EDGE,"E38.trimOffspring")])],"isStart":true})});
            var sketch = newSketch(context, id + "F26", { "sketchPlane" : qUnion([Q0])});
            skArc(sketch, "E39.0", {"start": v(-21.57, 21) * mm, "mid": v(-15.88, 22.56) * mm, "end": v(-10, 22.15) * mm});
            skLineSegment(sketch, "E39.1", {"start": v(-10, 22.15) * mm, "end": v(-10, 21) * mm});
            skLineSegment(sketch, "E40", {"start": v(-10, 21) * mm, "end": v(-21.57, 21) * mm});
            skSolve(sketch);
        }
        {
            var Q0;
            Q0 = qSketchRegion(id + "F26", true);
            extrude(context, id + "F27", {"entities" : qUnion([Q0]), "operationType" : NewBodyOperationType.ADD, "depth" : 1 * mm, "offsetDistance" : 25 * mm});
        }
        {
            var Q0;
            {var subQ0=sQuery(id+"F24.wireOp",EDGE,"E30");Q0=makeQuery(id+"F25.boolean.opBoolean","SPLIT",EDGE,{"disambiguationData":[topologyDisambiguationEdgeConnected([makeQuery(id+"F18.opExtrude","CAP_FACE",FACE,{"disambiguationData":[OSD([sQuery(id+"F17.wireOp",EDGE,"E28")])],"isStart":false})])],"derivedFrom":makeQuery(id+"F25.opExtrude","CAP_EDGE",EDGE,{"disambiguationData":[OSD([subQ0])],"isStart":true})});}
            var Q1;
            Q1=makeQuery(id+"F25.opExtrude","SWEPT_EDGE",EDGE,{"disambiguationData":[OSD([sQuery(id+"F24.wireOp",EDGE,"E30"),sQuery(id+"F24.wireOp",EDGE,"E35")])]});
            var Q2;
            {var subQ0=sQuery(id+"F24.wireOp",EDGE,"E34");var subQ1=sQuery(id+"F24.wireOp",EDGE,"E30");Q2=makeQuery(id+"F25.boolean.opBoolean","SPLIT",EDGE,{"disambiguationData":[TD([makeQuery(id+"F16.opExtrude","SWEPT_FACE",FACE,{"disambiguationData":[OSD([sQuery(id+"F15.wireOp",EDGE,"E27.trimOffspring")])]})])],"derivedFrom":makeQuery(id+"F25.opExtrude","SWEPT_EDGE",EDGE,{"disambiguationData":[OSD([subQ1,subQ0])]})});}
            var Q3;
            {var subQ0=makeQuery(id+"F1.opExtrude","CAP_FACE",FACE,{"disambiguationData":[OSD([sQuery(id+"F0.wireOp",EDGE,"E0.bottom"),sQuery(id+"F0.wireOp",EDGE,"E0.top"),sQuery(id+"F0.wireOp",EDGE,"E0.left"),sQuery(id+"F0.wireOp",EDGE,"E0.right")])],"isStart":false});var subQ1=makeQuery(id+"F18.opExtrude","CAP_FACE",FACE,{"disambiguationData":[OSD([sQuery(id+"F17.wireOp",EDGE,"E28")])],"isStart":false});var subQ2=sQuery(id+"F24.wireOp",EDGE,"E38.trimOffspring");var subQ3=makeQuery(id+"F25.opExtrude","SWEPT_FACE",FACE,{"disambiguationData":[OSD([subQ2])]});Q3=makeQuery(id+"F25.boolean.opBoolean","SPLIT",EDGE,{"disambiguationData":[topologyDisambiguationEdgeConnected([subQ0,subQ1,subQ3]),TD([makeQuery(id+"F3.opExtrude","SWEPT_FACE",FACE,{"disambiguationData":[OSD([sQuery(id+"F2.wireOp",EDGE,"E9.left")])]})])],"derivedFrom":makeQuery(id+"F25.opExtrude","CAP_EDGE",EDGE,{"disambiguationData":[OSD([subQ2])],"isStart":true})});}
            var Q4;
            Q4=makeQuery(id+"F25.opExtrude","SWEPT_EDGE",EDGE,{"disambiguationData":[OSD([sQuery(id+"F24.wireOp",EDGE,"E32"),sQuery(id+"F24.wireOp",EDGE,"E38.trimOffspring")])]});
            fillet(context, id + "F28", {"entities" : qUnion([Q0, Q1, Q2, Q3, Q4]), "radius" : 0.5 * mm, "tangentPropagation" : true, "allowEdgeOverflow" : false});
        }
        {
            var Q0;
            Q0=makeQuery(id+"F27.opExtrude","CAP_EDGE",EDGE,{"disambiguationData":[OSD([sQuery(id+"F26.wireOp",EDGE,"E39.0")])],"isStart":false});
            fillet(context, id + "F29", {"entities" : qUnion([Q0]), "radius" : 0.5 * mm, "tangentPropagation" : true, "allowEdgeOverflow" : false});
        }
        {
            var Q0;
            Q0 = qSketchRegion(id + "F23", true);
            extrude(context, id + "F30", {"entities" : qUnion([Q0]), "operationType" : NewBodyOperationType.REMOVE, "endBound" : BoundingType.THROUGH_ALL, "oppositeDirection" : true, "depth" : 25 * mm, "offsetDistance" : 25 * mm});
        }
        {
            var Q0;
            Q0=makeQuery(id+"F18.boolean.opBoolean","INTERSECT",EDGE,{"derivedFrom":[makeQuery(id+"F8.boolean.opBoolean","COPY",FACE,{"derivedFrom":makeQuery(id+"F8.opExtrude","SWEPT_FACE",FACE,{"disambiguationData":[OSD([sQuery(id+"F7.wireOp",EDGE,"E12")])]})}),makeQuery(id+"F18.opExtrude","CAP_FACE",FACE,{"disambiguationData":[OSD([sQuery(id+"F17.wireOp",EDGE,"E28")])],"isStart":false})]});
            chamfer(context, id + "F31", {"entities" : qUnion([Q0]), "chamferType" : ChamferType.OFFSET_ANGLE, "width" : 2 * mm, "oppositeDirection" : false, "angle" : 50 * degree, "tangentPropagation" : true});
        }
        {
            var Q0;
            Q0=makeQuery(id+"F16.opExtrude","CAP_EDGE",EDGE,{"disambiguationData":[OSD([sQuery(id+"F15.wireOp",EDGE,"E21")])],"isStart":false});
            var Q1;
            Q1=makeQuery(id+"F16.opExtrude","CAP_EDGE",EDGE,{"disambiguationData":[OSD([sQuery(id+"F15.wireOp",EDGE,"E25")])],"isStart":false});
            var Q2;
            Q2=makeQuery(id+"F16.opExtrude","CAP_EDGE",EDGE,{"disambiguationData":[OSD([sQuery(id+"F15.wireOp",EDGE,"E23")])],"isStart":false});
            var Q3;
            Q3=makeQuery(id+"F16.opExtrude","CAP_EDGE",EDGE,{"disambiguationData":[OSD([sQuery(id+"F15.wireOp",EDGE,"E22")])],"isStart":false});
            fillet(context, id + "F32", {"entities" : qUnion([Q0, Q1, Q2, Q3]), "radius" : 4 * mm, "tangentPropagation" : true, "allowEdgeOverflow" : false});
        }
        {
            var Q0;
            {var subQ0=sQuery(id+"F0.wireOp",EDGE,"E0.right");var subQ1=sQuery(id+"F0.wireOp",EDGE,"E0.bottom");var subQ2=sQuery(id+"F0.wireOp",EDGE,"E0.top");var subQ3=sQuery(id+"F0.wireOp",EDGE,"E0.left");Q0=makeQuery(id+"F30.boolean.opBoolean","MERGE",FACE,{"derivedFrom":[makeQuery(id+"F18.boolean.opBoolean","MERGE",FACE,{"derivedFrom":[makeQuery(id+"F16.boolean.opBoolean","SPLIT",FACE,{"disambiguationData":[TD([makeQuery(id+"F1.opExtrude","SWEPT_FACE",FACE,{"disambiguationData":[OSD([subQ1])]}),makeQuery(id+"F1.opExtrude","SWEPT_FACE",FACE,{"disambiguationData":[OSD([subQ2])]}),makeQuery(id+"F1.opExtrude","SWEPT_FACE",FACE,{"disambiguationData":[OSD([subQ3])]}),makeQuery(id+"F1.opExtrude","SWEPT_FACE",FACE,{"disambiguationData":[OSD([subQ0])]}),makeQuery(id+"F3.opExtrude","SWEPT_FACE",FACE,{"disambiguationData":[OSD([sQuery(id+"F2.wireOp",EDGE,"E1.top")])]}),makeQuery(id+"F3.opExtrude","SWEPT_FACE",FACE,{"disambiguationData":[OSD([sQuery(id+"F2.wireOp",EDGE,"E1.right")])]}),makeQuery(id+"F3.opExtrude","SWEPT_FACE",FACE,{"disambiguationData":[OSD([sQuery(id+"F2.wireOp",EDGE,"E2.top")])]}),makeQuery(id+"F3.opExtrude","SWEPT_FACE",FACE,{"disambiguationData":[OSD([sQuery(id+"F2.wireOp",EDGE,"E2.left")])]}),makeQuery(id+"F3.opExtrude","SWEPT_FACE",FACE,{"disambiguationData":[OSD([sQuery(id+"F2.wireOp",EDGE,"E2.right")])]}),makeQuery(id+"F3.opExtrude","SWEPT_FACE",FACE,{"disambiguationData":[OSD([sQuery(id+"F2.wireOp",EDGE,"E3.top")])]}),makeQuery(id+"F3.opExtrude","SWEPT_FACE",FACE,{"disambiguationData":[OSD([sQuery(id+"F2.wireOp",EDGE,"E3.left")])]}),makeQuery(id+"F3.opExtrude","SWEPT_FACE",FACE,{"disambiguationData":[OSD([sQuery(id+"F2.wireOp",EDGE,"E4.bottom")])]}),makeQuery(id+"F3.opExtrude","SWEPT_FACE",FACE,{"disambiguationData":[OSD([sQuery(id+"F2.wireOp",EDGE,"E4.top")])]}),makeQuery(id+"F3.opExtrude","SWEPT_FACE",FACE,{"disambiguationData":[OSD([sQuery(id+"F2.wireOp",EDGE,"E4.right")])]}),makeQuery(id+"F3.opExtrude","SWEPT_FACE",FACE,{"disambiguationData":[OSD([sQuery(id+"F2.wireOp",EDGE,"E5.bottom")])]}),makeQuery(id+"F3.opExtrude","SWEPT_FACE",FACE,{"disambiguationData":[OSD([sQuery(id+"F2.wireOp",EDGE,"E5.right")])]}),makeQuery(id+"F3.opExtrude","SWEPT_FACE",FACE,{"disambiguationData":[OSD([sQuery(id+"F2.wireOp",EDGE,"E6.bottom")])]}),makeQuery(id+"F3.opExtrude","SWEPT_FACE",FACE,{"disambiguationData":[OSD([sQuery(id+"F2.wireOp",EDGE,"E6.top")])]}),makeQuery(id+"F3.opExtrude","SWEPT_FACE",FACE,{"disambiguationData":[OSD([sQuery(id+"F2.wireOp",EDGE,"E6.left")])]}),makeQuery(id+"F3.opExtrude","SWEPT_FACE",FACE,{"disambiguationData":[OSD([sQuery(id+"F2.wireOp",EDGE,"E6.right")])]}),makeQuery(id+"F3.opExtrude","SWEPT_FACE",FACE,{"disambiguationData":[OSD([sQuery(id+"F2.wireOp",EDGE,"E7.bottom")])]}),makeQuery(id+"F3.opExtrude","SWEPT_FACE",FACE,{"disambiguationData":[OSD([sQuery(id+"F2.wireOp",EDGE,"E7.left")])]}),makeQuery(id+"F3.opExtrude","SWEPT_FACE",FACE,{"disambiguationData":[OSD([sQuery(id+"F2.wireOp",EDGE,"E8.bottom")])]}),makeQuery(id+"F3.opExtrude","SWEPT_FACE",FACE,{"disambiguationData":[OSD([sQuery(id+"F2.wireOp",EDGE,"E8.top")])]}),makeQuery(id+"F3.opExtrude","SWEPT_FACE",FACE,{"disambiguationData":[OSD([sQuery(id+"F2.wireOp",EDGE,"E8.left")])]}),makeQuery(id+"F3.opExtrude","SWEPT_FACE",FACE,{"disambiguationData":[OSD([sQuery(id+"F2.wireOp",EDGE,"E9.top")])]}),makeQuery(id+"F3.opExtrude","SWEPT_FACE",FACE,{"disambiguationData":[OSD([sQuery(id+"F2.wireOp",EDGE,"E9.left")])]}),makeQuery(id+"F3.opExtrude","SWEPT_FACE",FACE,{"disambiguationData":[OSD([sQuery(id+"F2.wireOp",EDGE,"E9.right")])]}),makeQuery(id+"F3.opExtrude","SWEPT_FACE",FACE,{"disambiguationData":[OSD([sQuery(id+"F2.wireOp",EDGE,"E10.bottom")])]}),makeQuery(id+"F3.opExtrude","SWEPT_FACE",FACE,{"disambiguationData":[OSD([sQuery(id+"F2.wireOp",EDGE,"E10.top")])]}),makeQuery(id+"F3.opExtrude","SWEPT_FACE",FACE,{"disambiguationData":[OSD([sQuery(id+"F2.wireOp",EDGE,"E10.left")])]}),makeQuery(id+"F3.opExtrude","SWEPT_FACE",FACE,{"disambiguationData":[OSD([sQuery(id+"F2.wireOp",EDGE,"E10.right")])]}),makeQuery(id+"F8.boolean.opBoolean","COPY",FACE,{"derivedFrom":makeQuery(id+"F8.opExtrude","SWEPT_FACE",FACE,{"disambiguationData":[OSD([sQuery(id+"F7.wireOp",EDGE,"E12")])]})}),makeQuery(id+"F8.boolean.opBoolean","COPY",FACE,{"derivedFrom":makeQuery(id+"F8.opExtrude","SWEPT_FACE",FACE,{"disambiguationData":[OSD([sQuery(id+"F7.wireOp",EDGE,"E13")])]})}),makeQuery(id+"F16.opExtrude","SWEPT_FACE",FACE,{"disambiguationData":[OSD([sQuery(id+"F15.wireOp",EDGE,"E18")])]}),makeQuery(id+"F16.opExtrude","SWEPT_FACE",FACE,{"disambiguationData":[OSD([sQuery(id+"F15.wireOp",EDGE,"E19")])]}),makeQuery(id+"F16.opExtrude","SWEPT_FACE",FACE,{"disambiguationData":[OSD([sQuery(id+"F15.wireOp",EDGE,"E21")])]}),makeQuery(id+"F16.opExtrude","SWEPT_FACE",FACE,{"disambiguationData":[OSD([sQuery(id+"F15.wireOp",EDGE,"E22")])]}),makeQuery(id+"F16.opExtrude","SWEPT_FACE",FACE,{"disambiguationData":[OSD([sQuery(id+"F15.wireOp",EDGE,"E23")])]}),makeQuery(id+"F16.opExtrude","SWEPT_FACE",FACE,{"disambiguationData":[OSD([sQuery(id+"F15.wireOp",EDGE,"E26.trimOffspring")])]}),makeQuery(id+"F16.opExtrude","SWEPT_FACE",FACE,{"disambiguationData":[OSD([sQuery(id+"F15.wireOp",EDGE,"E27.trimOffspring")])]})])],"derivedFrom":makeQuery(id+"F1.opExtrude","CAP_FACE",FACE,{"disambiguationData":[OSD([subQ1,subQ2,subQ3,subQ0])],"isStart":false})}),makeQuery(id+"F18.opExtrude","CAP_FACE",FACE,{"disambiguationData":[OSD([sQuery(id+"F17.wireOp",EDGE,"E28")])],"isStart":false})]}),makeQuery(id+"F30.opExtrude","SWEPT_FACE",FACE,{"disambiguationData":[OSD([sQuery(id+"F23.wireOp",EDGE,"E29.bottom")])]})]});}
            var sketch = newSketch(context, id + "F33", { "sketchPlane" : qUnion([Q0])});
            skLineSegment(sketch, "E41.2", {"start": v(-23, 2.1) * mm, "end": v(-23, -4) * mm});
            skLineSegment(sketch, "E41.3", {"start": v(-29.25, -14) * mm, "end": v(-26.2, -14) * mm});
            skArc(sketch, "E41.4", {"start": v(-23, -15) * mm, "mid": v(-23.3, -14.3) * mm, "end": v(-24, -14) * mm});
            skLineSegment(sketch, "E41.5", {"start": v(-23, -15) * mm, "end": v(-23, -17.62) * mm});
            skLineSegment(sketch, "E41.6", {"start": v(-19, -15) * mm, "end": v(-17.5, -15) * mm});
            skArc(sketch, "E41.7", {"start": v(-19, -15) * mm, "mid": v(-19.7, -15.3) * mm, "end": v(-20, -16) * mm});
            skLineSegment(sketch, "E41.9", {"start": v(-15, -16) * mm, "end": v(-15, -20.25) * mm});
            skLineSegment(sketch, "E41.10", {"start": v(-20, -20.25) * mm, "end": v(-20, -16) * mm});
            skLineSegment(sketch, "E41.12", {"start": v(-24, 14) * mm, "end": v(-29.25, 14) * mm});
            skLineSegment(sketch, "E41.14", {"start": v(-23, 15) * mm, "end": v(-23, 20.25) * mm});
            skLineSegment(sketch, "E41.15", {"start": v(-20, 18) * mm, "end": v(-20, 20.25) * mm});
            skArc(sketch, "E41.16", {"start": v(-20, 18) * mm, "mid": v(-19.92, 17.62) * mm, "end": v(-19.7, 17.3) * mm});
            skLineSegment(sketch, "E41.17", {"start": v(-16, 17) * mm, "end": v(-17.5, 17) * mm});
            skArc(sketch, "E41.18", {"start": v(-16, 17) * mm, "mid": v(-15.62, 17.08) * mm, "end": v(-15.3, 17.3) * mm});
            skLineSegment(sketch, "E41.19", {"start": v(-15, 20.25) * mm, "end": v(-15, 18.68) * mm});
            skLineSegment(sketch, "E41.23", {"start": v(29.25, -14) * mm, "end": v(27.06, -14) * mm});
            skArc(sketch, "E41.24", {"start": v(23, -15) * mm, "mid": v(23.3, -14.3) * mm, "end": v(24, -14) * mm});
            skLineSegment(sketch, "E41.25", {"start": v(23, -20.4) * mm, "end": v(23, -15) * mm});
            skLineSegment(sketch, "E41.26", {"start": v(10, -20.4) * mm, "end": v(10, -19.07) * mm});
            skArc(sketch, "E41.27", {"start": v(9.7, -15.3) * mm, "mid": v(9.92, -15.62) * mm, "end": v(10, -16) * mm});
            skLineSegment(sketch, "E41.28", {"start": v(7.5, -15) * mm, "end": v(6, -15) * mm});
            skArc(sketch, "E41.29", {"start": v(5, -16) * mm, "mid": v(5.3, -15.3) * mm, "end": v(6, -15) * mm});
            skLineSegment(sketch, "E41.30", {"start": v(5, -20.25) * mm, "end": v(5, -16) * mm});
            skPoint(sketch, "E41.31", {"position": v(-19.7, 17.3) * mm});
            skLineSegment(sketch, "E42", {"start": v(-29.25, -7.8) * mm, "end": v(-29.25, -14) * mm});
            skLineSegment(sketch, "E43", {"start": v(-20.7, -20.25) * mm, "end": v(-20, -20.25) * mm});
            skLineSegment(sketch, "E44", {"start": v(-15, -20.25) * mm, "end": v(-8.7, -20.25) * mm});
            skLineSegment(sketch, "E45", {"start": v(10, -20.4) * mm, "end": v(14.31, -20.4) * mm});
            skArc(sketch, "E46", {"start": v(4.35, 20.25) * mm, "mid": v(0.9, 17.33) * mm, "end": v(-1.72, 13.64) * mm});
            skLineSegment(sketch, "E47", {"start": v(29.25, -14) * mm, "end": v(29.25, -4.65) * mm});
            skLineSegment(sketch, "E48", {"start": v(-29.25, 5.97) * mm, "end": v(-29.25, 8.6) * mm});
            skLineSegment(sketch, "E49", {"start": v(-23, 20.25) * mm, "end": v(-20, 20.25) * mm});
            skLineSegment(sketch, "E50", {"start": v(-15, 20.25) * mm, "end": v(-7.91, 20.25) * mm});
            skPoint(sketch, "E51.orphan", {"position": v(-15, 21) * mm});
            skPoint(sketch, "E52.orphan", {"position": v(-20, 21) * mm});
            skPoint(sketch, "E53.orphan", {"position": v(-23, 21) * mm});
            skPoint(sketch, "E54.orphan", {"position": v(-30, 14) * mm});
            skPoint(sketch, "E55.orphan", {"position": v(-30, 5) * mm});
            skPoint(sketch, "E56.orphan", {"position": v(-30, -5) * mm});
            skPoint(sketch, "E57.orphan", {"position": v(-30, -14) * mm});
            skPoint(sketch, "E58.orphan", {"position": v(-23, -21) * mm});
            skPoint(sketch, "E59.orphan", {"position": v(-20, -21) * mm});
            skPoint(sketch, "E60.orphan", {"position": v(-15, -22) * mm});
            skPoint(sketch, "E61.orphan", {"position": v(5, -21) * mm});
            skPoint(sketch, "E62.orphan", {"position": v(10, -21) * mm});
            skPoint(sketch, "E63.orphan", {"position": v(23, -21) * mm});
            skPoint(sketch, "E64.orphan", {"position": v(30, -14) * mm});
            skArc(sketch, "E65", {"start": v(-23, 2.1) * mm, "mid": v(-19.89, 0.44) * mm, "end": v(-16.36, 0.51) * mm});
            skPoint(sketch, "E66.orphan", {"position": v(-23.27, 5) * mm});
            skPoint(sketch, "E67.orphan", {"position": v(-23, 4.48) * mm});
            skLineSegment(sketch, "E68", {"start": v(27.5, 9.98) * mm, "end": v(28.95, 10.64) * mm});
            skLineSegment(sketch, "E69", {"start": v(28.95, 10.64) * mm, "end": v(29.38, 8.24) * mm});
            skLineSegment(sketch, "E70", {"start": v(29.55, 7.27) * mm, "end": v(29.58, 5.64) * mm});
            skLineSegment(sketch, "E71", {"start": v(29.58, 5.64) * mm, "end": v(27.8, 5.72) * mm});
            skLineSegment(sketch, "E72", {"start": v(27.8, 5.72) * mm, "end": v(27.86, 7.22) * mm});
            skLineSegment(sketch, "E73", {"start": v(27.92, 8.97) * mm, "end": v(27.5, 9.98) * mm});
            skLineSegment(sketch, "E74", {"start": v(-24, 14) * mm, "end": v(-23.04, 13.55) * mm});
            skLineSegment(sketch, "E75", {"start": v(-23.04, 13.55) * mm, "end": v(-22.6, 12.74) * mm});
            skLineSegment(sketch, "E76", {"start": v(-23, 15) * mm, "end": v(-21.58, 14.58) * mm});
            skArc(sketch, "E77.trimOffspring", {"start": v(-22.6, 12.74) * mm, "mid": v(-23.73, 11.6) * mm, "end": v(-24.58, 10.24) * mm});
            skLineSegment(sketch, "E78", {"start": v(-19.7, 17.3) * mm, "end": v(-20.55, 18.14) * mm});
            skLineSegment(sketch, "E79", {"start": v(-20.55, 18.14) * mm, "end": v(-21.58, 14.58) * mm});
            skLineSegment(sketch, "E80", {"start": v(-19.3, 14.17) * mm, "end": v(-19, 15.45) * mm});
            skLineSegment(sketch, "E81", {"start": v(-19, 15.45) * mm, "end": v(-17.5, 17) * mm});
            skPoint(sketch, "E82.orphan", {"position": v(-19, 17) * mm});
            skLineSegment(sketch, "E83", {"start": v(-15.3, 17.3) * mm, "end": v(-13.2, 13.05) * mm});
            skLineSegment(sketch, "E84", {"start": v(-13.2, 13.05) * mm, "end": v(-13.2, 12.1) * mm});
            skLineSegment(sketch, "E85", {"start": v(-12.55, 11.3) * mm, "end": v(-12.12, 13.49) * mm});
            skLineSegment(sketch, "E86", {"start": v(-12.96, 15) * mm, "end": v(-15, 18.68) * mm});
            skPoint(sketch, "E87.orphan", {"position": v(-15, 18) * mm});
            skArc(sketch, "E88.trimOffspring", {"start": v(-13.2, 12.1) * mm, "mid": v(-16, 13.88) * mm, "end": v(-19.3, 14.17) * mm});
            skLineSegment(sketch, "E89", {"start": v(-12.96, 15) * mm, "end": v(-8.5, 16.2) * mm});
            skLineSegment(sketch, "E90", {"start": v(-8.5, 16.2) * mm, "end": v(-7.63, 17.84) * mm});
            skLineSegment(sketch, "E91", {"start": v(-7.63, 17.84) * mm, "end": v(-7.91, 20.25) * mm});
            skLineSegment(sketch, "E92", {"start": v(-6.33, 20.25) * mm, "end": v(-6.02, 17.75) * mm});
            skLineSegment(sketch, "E93", {"start": v(-6.02, 17.75) * mm, "end": v(-6.26, 16.94) * mm});
            skLineSegment(sketch, "E94", {"start": v(-6.7, 15.45) * mm, "end": v(-12.12, 13.49) * mm});
            skLineSegment(sketch, "E95", {"start": v(-6.26, 16.94) * mm, "end": v(-3.74, 15.45) * mm});
            skLineSegment(sketch, "E96", {"start": v(-3.74, 15.45) * mm, "end": v(-0.61, 15.45) * mm});
            skLineSegment(sketch, "E97", {"start": v(-6.7, 15.45) * mm, "end": v(-4.15, 13.64) * mm});
            skLineSegment(sketch, "E98", {"start": v(-4.15, 13.64) * mm, "end": v(-1.72, 13.64) * mm});
            skLineSegment(sketch, "E99.trimOffspring", {"start": v(-6.33, 20.25) * mm, "end": v(4.35, 20.25) * mm});
            skLineSegment(sketch, "E100", {"start": v(-24.58, 10.24) * mm, "end": v(-27.04, 11.6) * mm});
            skLineSegment(sketch, "E101", {"start": v(-27.04, 11.6) * mm, "end": v(-29.25, 10.84) * mm});
            skLineSegment(sketch, "E102", {"start": v(-29.25, 9.5) * mm, "end": v(-27.18, 10.04) * mm});
            skLineSegment(sketch, "E103", {"start": v(-27.18, 10.04) * mm, "end": v(-24.96, 9.23) * mm});
            skLineSegment(sketch, "E104", {"start": v(-24.96, 9.23) * mm, "end": v(-22.74, 9.23) * mm});
            skLineSegment(sketch, "E105", {"start": v(-22.74, 9.23) * mm, "end": v(-22.74, 8.68) * mm});
            skLineSegment(sketch, "E106", {"start": v(-22.74, 8.68) * mm, "end": v(-25.1, 8.68) * mm});
            skLineSegment(sketch, "E107", {"start": v(-25.1, 8.68) * mm, "end": v(-26.96, 7.97) * mm});
            skLineSegment(sketch, "E108", {"start": v(-29.25, 8.6) * mm, "end": v(-32.2, 8.92) * mm});
            skLineSegment(sketch, "E109", {"start": v(-32.2, 8.92) * mm, "end": v(-32.2, 9.54) * mm});
            skLineSegment(sketch, "E110", {"start": v(-29.25, 9.5) * mm, "end": v(-32.2, 9.54) * mm});
            skLineSegment(sketch, "E111.trimOffspring", {"start": v(-29.25, 10.84) * mm, "end": v(-29.25, 14) * mm});
            skArc(sketch, "E112.trimOffspring", {"start": v(-25.24, 6.82) * mm, "mid": v(-25.12, 5.9) * mm, "end": v(-24.88, 5) * mm});
            skLineSegment(sketch, "E113", {"start": v(-13.38, 8.1) * mm, "end": v(-9.52, 6.76) * mm});
            skLineSegment(sketch, "E114", {"start": v(-9.52, 6.76) * mm, "end": v(-1.86, 6.76) * mm});
            skLineSegment(sketch, "E115", {"start": v(-1.86, 6.76) * mm, "end": v(4, 5.7) * mm});
            skLineSegment(sketch, "E116", {"start": v(4, 5.7) * mm, "end": v(4, 4.54) * mm});
            skLineSegment(sketch, "E117", {"start": v(-1.78, 3.14) * mm, "end": v(-6.84, 3.14) * mm});
            skLineSegment(sketch, "E118", {"start": v(-6.84, 3.14) * mm, "end": v(-13.64, 7.27) * mm});
            skLineSegment(sketch, "E119", {"start": v(-13.64, 7.27) * mm, "end": v(-13.38, 8.1) * mm});
            skArc(sketch, "E120.trimOffspring", {"start": v(-11.56, 9.3) * mm, "mid": v(-11.97, 10.35) * mm, "end": v(-12.55, 11.3) * mm});
            skArc(sketch, "E121.trimOffspring", {"start": v(-3.45, 1.4) * mm, "mid": v(-3.03, -0.23) * mm, "end": v(-2.45, -1.8) * mm});
            skLineSegment(sketch, "E122", {"start": v(-11.56, 9.3) * mm, "end": v(-9.03, 8.27) * mm});
            skLineSegment(sketch, "E123", {"start": v(-9.03, 8.27) * mm, "end": v(-4.69, 8.79) * mm});
            skLineSegment(sketch, "E124", {"start": v(-4.69, 8.79) * mm, "end": v(-1.18, 7.95) * mm});
            skLineSegment(sketch, "E125", {"start": v(-1.18, 7.95) * mm, "end": v(-0.62, 10.3) * mm});
            skLineSegment(sketch, "E126", {"start": v(-0.62, 10.3) * mm, "end": v(-1.72, 13.64) * mm});
            skLineSegment(sketch, "E127", {"start": v(-29.25, 5.97) * mm, "end": v(-28.26, 5) * mm});
            skLineSegment(sketch, "E128", {"start": v(-28.26, 5) * mm, "end": v(-26.96, 7.97) * mm});
            skLineSegment(sketch, "E129", {"start": v(-25.24, 6.82) * mm, "end": v(-26.3, 5) * mm});
            skLineSegment(sketch, "E130.trimOffspring", {"start": v(-26.3, 5) * mm, "end": v(-24.88, 5) * mm});
            skPoint(sketch, "E131.orphan", {"position": v(-29.25, 5) * mm});
            skLineSegment(sketch, "E132", {"start": v(-12.58, 3.14) * mm, "end": v(-6.84, 1.13) * mm});
            skLineSegment(sketch, "E133", {"start": v(-6.84, 1.13) * mm, "end": v(-3.45, 1.4) * mm});
            skLineSegment(sketch, "E134", {"start": v(-23, -4) * mm, "end": v(-16.36, -1.7) * mm});
            skLineSegment(sketch, "E135", {"start": v(-16.36, -1.7) * mm, "end": v(-16.36, 0.51) * mm});
            skLineSegment(sketch, "E136", {"start": v(-14.55, 1.3) * mm, "end": v(-13.55, -1.73) * mm});
            skLineSegment(sketch, "E137", {"start": v(-13.55, -1.73) * mm, "end": v(-6.78, -6.32) * mm});
            skLineSegment(sketch, "E138", {"start": v(-6.78, -6.32) * mm, "end": v(-2.45, -1.8) * mm});
            skLineSegment(sketch, "E139", {"start": v(-27, -6.88) * mm, "end": v(-22.32, -6.03) * mm});
            skPoint(sketch, "E139.startSnap0", {"position": v(-27, -5) * mm});
            skLineSegment(sketch, "E140", {"start": v(-20.28, -5.27) * mm, "end": v(-15.03, -3.03) * mm});
            skLineSegment(sketch, "E141", {"start": v(-15.03, -3.03) * mm, "end": v(-9.72, -6.8) * mm});
            skLineSegment(sketch, "E142", {"start": v(-4.85, -7.13) * mm, "end": v(-1.5, -3.76) * mm});
            skArc(sketch, "E143.trimOffspring", {"start": v(-14.55, 1.3) * mm, "mid": v(-13.48, 2.13) * mm, "end": v(-12.58, 3.14) * mm});
            skArc(sketch, "E144.trimOffspring", {"start": v(-1.5, -3.76) * mm, "mid": v(0.87, -7) * mm, "end": v(3.88, -9.63) * mm});
            skLineSegment(sketch, "E145", {"start": v(-27, -6.88) * mm, "end": v(-29.25, -7.8) * mm});
            skPoint(sketch, "E41.1.start.orphan", {"position": v(-24, -5) * mm});
            skLineSegment(sketch, "E146", {"start": v(-22.32, -6.03) * mm, "end": v(-24.25, -10.8) * mm});
            skLineSegment(sketch, "E147", {"start": v(-24.25, -10.8) * mm, "end": v(-26.2, -14) * mm});
            skLineSegment(sketch, "E148", {"start": v(-24, -14) * mm, "end": v(-22.41, -11.66) * mm});
            skLineSegment(sketch, "E149", {"start": v(-21.72, -9.96) * mm, "end": v(-20.28, -5.27) * mm});
            skLineSegment(sketch, "E150", {"start": v(-21.72, -9.96) * mm, "end": v(-16.2, -12.5) * mm});
            skLineSegment(sketch, "E151", {"start": v(-16.2, -12.5) * mm, "end": v(-9.72, -6.8) * mm});
            skLineSegment(sketch, "E152", {"start": v(-8.11, -7.93) * mm, "end": v(-11.56, -11.96) * mm});
            skLineSegment(sketch, "E153", {"start": v(-17.5, -15) * mm, "end": v(-22.41, -11.66) * mm});
            skLineSegment(sketch, "E154", {"start": v(-20.7, -20.25) * mm, "end": v(-23, -17.62) * mm});
            skPoint(sketch, "E41.8.end.orphan", {"position": v(-16, -15) * mm});
            skLineSegment(sketch, "E155.trimOffspring", {"start": v(-8.11, -7.93) * mm, "end": v(-6.67, -8.95) * mm});
            skPoint(sketch, "E156.orphan", {"position": v(-23, -20.25) * mm});
            skLineSegment(sketch, "E157", {"start": v(-13.07, -13.74) * mm, "end": v(-8.7, -17.46) * mm});
            skLineSegment(sketch, "E158", {"start": v(-8.7, -17.46) * mm, "end": v(-8.7, -20.25) * mm});
            skLineSegment(sketch, "E159", {"start": v(-11.56, -11.96) * mm, "end": v(-5.93, -16.85) * mm});
            skLineSegment(sketch, "E160", {"start": v(-5.56, -18.55) * mm, "end": v(-5.2, -20.25) * mm});
            skLineSegment(sketch, "E161.trimOffspring", {"start": v(-13.07, -13.74) * mm, "end": v(-15, -16) * mm});
            skLineSegment(sketch, "E162.trimOffspring", {"start": v(-5.2, -20.25) * mm, "end": v(5, -20.25) * mm});
            skLineSegment(sketch, "E163", {"start": v(-6.67, -8.95) * mm, "end": v(-2.11, -15.28) * mm});
            skLineSegment(sketch, "E164", {"start": v(-2.11, -15.28) * mm, "end": v(-5.93, -16.85) * mm});
            skLineSegment(sketch, "E165", {"start": v(-5.56, -18.55) * mm, "end": v(0.48, -16.07) * mm});
            skLineSegment(sketch, "E166", {"start": v(1.7, -15.57) * mm, "end": v(0.97, -14.63) * mm});
            skLineSegment(sketch, "E167", {"start": v(0.48, -16.07) * mm, "end": v(1.7, -20.25) * mm});
            skLineSegment(sketch, "E168", {"start": v(5, -20.25) * mm, "end": v(3, -15.57) * mm});
            skLineSegment(sketch, "E169", {"start": v(3, -15.57) * mm, "end": v(1.7, -15.57) * mm});
            skLineSegment(sketch, "E170", {"start": v(-0.35, -12.92) * mm, "end": v(3.88, -9.63) * mm});
            skLineSegment(sketch, "E171", {"start": v(0.97, -14.63) * mm, "end": v(5.86, -10.83) * mm});
            skLineSegment(sketch, "E172.trimOffspring", {"start": v(-0.35, -12.92) * mm, "end": v(-4.85, -7.13) * mm});
            skLineSegment(sketch, "E173", {"start": v(7.5, -15) * mm, "end": v(9.18, -12.15) * mm});
            skLineSegment(sketch, "E174", {"start": v(11.02, -12.58) * mm, "end": v(9.7, -15.3) * mm});
            skArc(sketch, "E175.trimOffspring", {"start": v(5.86, -10.83) * mm, "mid": v(7.49, -11.57) * mm, "end": v(9.18, -12.15) * mm});
            skArc(sketch, "E176.trimOffspring", {"start": v(11.02, -12.58) * mm, "mid": v(13.48, -12.84) * mm, "end": v(15.94, -12.76) * mm});
            skPoint(sketch, "E177.orphan", {"position": v(9, -15) * mm});
            skLineSegment(sketch, "E178", {"start": v(10, -17.35) * mm, "end": v(15.67, -18.74) * mm});
            skLineSegment(sketch, "E179", {"start": v(10, -19.07) * mm, "end": v(14.31, -20.4) * mm});
            skLineSegment(sketch, "E180.trimOffspring", {"start": v(10, -17.35) * mm, "end": v(10, -16) * mm});
            skLineSegment(sketch, "E181.trimOffspring", {"start": v(22.48, -20.4) * mm, "end": v(23, -20.4) * mm});
            skLineSegment(sketch, "E182", {"start": v(15.94, -12.76) * mm, "end": v(17.6, -15.93) * mm});
            skLineSegment(sketch, "E183", {"start": v(17.6, -15.93) * mm, "end": v(15.67, -18.74) * mm});
            skLineSegment(sketch, "E184", {"start": v(17.65, -19.22) * mm, "end": v(19.66, -16.04) * mm});
            skLineSegment(sketch, "E185", {"start": v(19.66, -16.04) * mm, "end": v(18.06, -12.42) * mm});
            skArc(sketch, "E186.trimOffspring", {"start": v(18.06, -12.42) * mm, "mid": v(21.38, -11.33) * mm, "end": v(24.42, -9.63) * mm});
            skLineSegment(sketch, "E187.trimOffspring", {"start": v(17.65, -19.22) * mm, "end": v(22.48, -20.4) * mm});
            skLineSegment(sketch, "E188", {"start": v(25.35, -14) * mm, "end": v(25.54, -12) * mm});
            skLineSegment(sketch, "E189", {"start": v(25.54, -12) * mm, "end": v(24.42, -9.63) * mm});
            skLineSegment(sketch, "E190", {"start": v(25.63, -8.72) * mm, "end": v(27.06, -11.1) * mm});
            skLineSegment(sketch, "E191", {"start": v(27.06, -11.1) * mm, "end": v(27.06, -14) * mm});
            skLineSegment(sketch, "E192.trimOffspring", {"start": v(25.35, -14) * mm, "end": v(24, -14) * mm});
            skArc(sketch, "E193.trimOffspring", {"start": v(25.63, -8.72) * mm, "mid": v(27.6, -6.82) * mm, "end": v(29.25, -4.65) * mm});
            skLineSegment(sketch, "E194", {"start": v(29.55, 7.27) * mm, "end": v(32.3, 7.76) * mm});
            skLineSegment(sketch, "E195", {"start": v(32.3, 7.76) * mm, "end": v(32.14, 8.72) * mm});
            skLineSegment(sketch, "E196", {"start": v(32.14, 8.72) * mm, "end": v(29.38, 8.24) * mm});
            skLineSegment(sketch, "E197", {"start": v(27.44, 7.9) * mm, "end": v(23.97, 8.18) * mm});
            skLineSegment(sketch, "E198", {"start": v(23.97, 8.18) * mm, "end": v(23.8, 6.93) * mm});
            skLineSegment(sketch, "E199", {"start": v(23.8, 6.93) * mm, "end": v(27.86, 7.22) * mm});
            skLineSegment(sketch, "E200.trimOffspring", {"start": v(27.88, 7.97) * mm, "end": v(27.44, 7.9) * mm});
            skPoint(sketch, "E201.orphan", {"position": v(28.53, 7.27) * mm});
            skLineSegment(sketch, "E202.trimOffspring", {"start": v(27.88, 7.97) * mm, "end": v(27.92, 8.97) * mm});
            skLineSegment(sketch, "E203", {"start": v(-1.78, 3.14) * mm, "end": v(-1.78, 5.6) * mm});
            skLineSegment(sketch, "E204", {"start": v(-1.78, 5.6) * mm, "end": v(4, 4.54) * mm});
            skSolve(sketch);
        }
        {
            var Q0;
            Q0 = qSketchRegion(id + "F33", true);
            extrude(context, id + "F34", {"entities" : qUnion([Q0]), "operationType" : NewBodyOperationType.REMOVE, "oppositeDirection" : true, "depth" : 1.75 * mm, "offsetDistance" : 25 * mm});
        }
        {
            var Q0;
            Q0=makeQuery(id+"F1.opExtrude","CAP_FACE",FACE,{"disambiguationData":[OSD([sQuery(id+"F0.wireOp",EDGE,"E0.bottom"),sQuery(id+"F0.wireOp",EDGE,"E0.top"),sQuery(id+"F0.wireOp",EDGE,"E0.left"),sQuery(id+"F0.wireOp",EDGE,"E0.right")])],"isStart":true});
            var sketch = newSketch(context, id + "F35", { "sketchPlane" : qUnion([Q0])});
            skArc(sketch, "E205.1", {"start": v(-10, 18) * mm, "mid": v(-9.7, 17.3) * mm, "end": v(-9, 17) * mm});
            skLineSegment(sketch, "E205.2", {"start": v(-6, 17) * mm, "end": v(-6.24, 17) * mm});
            skArc(sketch, "E205.3", {"start": v(-6, 17) * mm, "mid": v(-5.3, 17.3) * mm, "end": v(-5, 18) * mm});
            skLineSegment(sketch, "E205.4", {"start": v(-5, 20.25) * mm, "end": v(-5, 19.5) * mm});
            skLineSegment(sketch, "E205.5", {"start": v(-23, 17.62) * mm, "end": v(-23, 15) * mm});
            skArc(sketch, "E205.6", {"start": v(-24, 14) * mm, "mid": v(-23.3, 14.3) * mm, "end": v(-23, 15) * mm});
            skLineSegment(sketch, "E205.7", {"start": v(-24, 14) * mm, "end": v(-26.13, 14) * mm});
            skLineSegment(sketch, "E205.8", {"start": v(-29.25, 5) * mm, "end": v(-27.67, 5) * mm});
            skArc(sketch, "E205.9", {"start": v(-23, 4) * mm, "mid": v(-23.3, 4.7) * mm, "end": v(-24, 5) * mm});
            skLineSegment(sketch, "E205.10", {"start": v(-23, 4) * mm, "end": v(-23, -0.8) * mm});
            skArc(sketch, "E205.11", {"start": v(-24, -5) * mm, "mid": v(-23.3, -4.7) * mm, "end": v(-23, -4) * mm});
            skLineSegment(sketch, "E205.12", {"start": v(-24, -5) * mm, "end": v(-29.25, -5) * mm});
            skLineSegment(sketch, "E205.13", {"start": v(-29.25, -14) * mm, "end": v(-24, -14) * mm});
            skArc(sketch, "E205.14", {"start": v(-23, -15) * mm, "mid": v(-23.3, -14.3) * mm, "end": v(-24, -14) * mm});
            skLineSegment(sketch, "E205.15", {"start": v(-23, -15) * mm, "end": v(-23, -20.25) * mm});
            skLineSegment(sketch, "E205.16", {"start": v(-10, -20.25) * mm, "end": v(-10, -16) * mm});
            skArc(sketch, "E205.17", {"start": v(-9, -15) * mm, "mid": v(-9.7, -15.3) * mm, "end": v(-10, -16) * mm});
            skLineSegment(sketch, "E205.18", {"start": v(-9, -15) * mm, "end": v(-6, -15) * mm});
            skArc(sketch, "E205.19", {"start": v(-5, -16) * mm, "mid": v(-6.7, -16.7) * mm, "end": v(-6, -15) * mm});
            skLineSegment(sketch, "E205.20", {"start": v(-5, -16) * mm, "end": v(-5, -20.25) * mm});
            skLineSegment(sketch, "E205.21", {"start": v(15, -20.25) * mm, "end": v(15, -16) * mm});
            skArc(sketch, "E205.22", {"start": v(16, -15) * mm, "mid": v(15.3, -15.3) * mm, "end": v(15, -16) * mm});
            skLineSegment(sketch, "E205.23", {"start": v(16, -15) * mm, "end": v(16.75, -15) * mm});
            skArc(sketch, "E205.24", {"start": v(20, -16) * mm, "mid": v(19.7, -15.3) * mm, "end": v(19, -15) * mm});
            skLineSegment(sketch, "E205.25", {"start": v(20, -16) * mm, "end": v(20, -16.75) * mm});
            skLineSegment(sketch, "E205.26", {"start": v(23, -20.25) * mm, "end": v(23, -16.75) * mm});
            skArc(sketch, "E205.27", {"start": v(24, -14) * mm, "mid": v(23.3, -14.3) * mm, "end": v(23, -15) * mm});
            skLineSegment(sketch, "E205.28", {"start": v(24, -14) * mm, "end": v(25.03, -14) * mm});
            skLineSegment(sketch, "E205.29", {"start": v(29.25, -5) * mm, "end": v(27.89, -5) * mm});
            skArc(sketch, "E205.30", {"start": v(23, -4) * mm, "mid": v(23.3, -4.7) * mm, "end": v(24, -5) * mm});
            skLineSegment(sketch, "E205.31", {"start": v(23, -4) * mm, "end": v(23, -3.37) * mm});
            skArc(sketch, "E205.32", {"start": v(23.3, 4.7) * mm, "mid": v(23.08, 4.38) * mm, "end": v(23, 4) * mm});
            skLineSegment(sketch, "E205.33", {"start": v(24.9, 5) * mm, "end": v(29.25, 5) * mm});
            skLineSegment(sketch, "E205.34", {"start": v(29.25, 14) * mm, "end": v(24, 14) * mm});
            skArc(sketch, "E205.35", {"start": v(23, 15) * mm, "mid": v(23.3, 14.3) * mm, "end": v(24, 14) * mm});
            skLineSegment(sketch, "E205.36", {"start": v(23, 15) * mm, "end": v(23, 16.25) * mm});
            skLineSegment(sketch, "E205.37", {"start": v(20, 20.25) * mm, "end": v(20, 18) * mm});
            skArc(sketch, "E205.38", {"start": v(19, 17) * mm, "mid": v(19.7, 17.3) * mm, "end": v(20, 18) * mm});
            skLineSegment(sketch, "E205.39", {"start": v(19, 17) * mm, "end": v(18, 17) * mm});
            skArc(sketch, "E205.40", {"start": v(15.3, 17.3) * mm, "mid": v(15.62, 17.08) * mm, "end": v(16, 17) * mm});
            skLineSegment(sketch, "E206.bottom", {"start": v(-21.25, 20.25) * mm, "end": v(-11.74, 20.25) * mm});
            skLineSegment(sketch, "E206.top", {"start": v(-23, -20.25) * mm, "end": v(-12, -20.25) * mm});
            skLineSegment(sketch, "E206.left", {"start": v(-29.25, 14) * mm, "end": v(-29.25, 5) * mm});
            skLineSegment(sketch, "E206.right", {"start": v(29.25, 13.79) * mm, "end": v(29.25, 5) * mm});
            skPoint(sketch, "E206.middle", {"position": v(0, 0) * mm});
            skPoint(sketch, "E207.orphan", {"position": v(-23, 21) * mm});
            skPoint(sketch, "E208.orphan", {"position": v(-29.25, 20.25) * mm});
            skPoint(sketch, "E209.orphan", {"position": v(-30, 14) * mm});
            skPoint(sketch, "E210.orphan", {"position": v(-10, 21) * mm});
            skPoint(sketch, "E211.orphan", {"position": v(-5, 21) * mm});
            skPoint(sketch, "E212.orphan", {"position": v(-30, 5) * mm});
            skPoint(sketch, "E213.orphan", {"position": v(-30, -5) * mm});
            skPoint(sketch, "E214.orphan", {"position": v(-30, -14) * mm});
            skLineSegment(sketch, "E215.trimOffspring", {"start": v(-29.25, -5) * mm, "end": v(-29.25, -8.35) * mm});
            skPoint(sketch, "E216.orphan", {"position": v(-29.25, -20.25) * mm});
            skPoint(sketch, "E217.orphan", {"position": v(-23, -21) * mm});
            skPoint(sketch, "E218.orphan", {"position": v(-10, -21) * mm});
            skLineSegment(sketch, "E219.trimOffspring", {"start": v(-5, -20.25) * mm, "end": v(-3.9, -20.25) * mm});
            skPoint(sketch, "E220.orphan", {"position": v(-5, -21) * mm});
            skPoint(sketch, "E221.orphan", {"position": v(15, -22) * mm});
            skLineSegment(sketch, "E222.trimOffspring", {"start": v(20, -20.25) * mm, "end": v(23, -20.25) * mm});
            skPoint(sketch, "E223.orphan", {"position": v(20, -21) * mm});
            skPoint(sketch, "E224.orphan", {"position": v(23, -21) * mm});
            skPoint(sketch, "E225.orphan", {"position": v(29.25, -20.25) * mm});
            skPoint(sketch, "E226.orphan", {"position": v(30, -14) * mm});
            skPoint(sketch, "E227.orphan", {"position": v(30, -5) * mm});
            skPoint(sketch, "E228.orphan", {"position": v(30, 5) * mm});
            skPoint(sketch, "E229.orphan", {"position": v(30, 14) * mm});
            skLineSegment(sketch, "E230.trimOffspring", {"start": v(29.25, -5) * mm, "end": v(29.25, -14) * mm});
            skPoint(sketch, "E231.orphan", {"position": v(29.25, 20.25) * mm});
            skLineSegment(sketch, "E232.trimOffspring", {"start": v(20, 20.25) * mm, "end": v(23, 20.25) * mm});
            skPoint(sketch, "E233.orphan", {"position": v(23, 21) * mm});
            skPoint(sketch, "E234.orphan", {"position": v(20, 21) * mm});
            skPoint(sketch, "E235.orphan", {"position": v(15, 21) * mm});
            skLineSegment(sketch, "E236.trimOffspring", {"start": v(-5, 20.25) * mm, "end": v(5, 20.25) * mm});
            skLineSegment(sketch, "E237.bottom", {"start": v(14.38, -13) * mm, "end": v(10.4, -13) * mm});
            skLineSegment(sketch, "E237.left", {"start": v(17, -13) * mm, "end": v(17, -7.43) * mm});
            skLineSegment(sketch, "E237.right", {"start": v(-17, -8.04) * mm, "end": v(-17, -1.8) * mm});
            skLineSegment(sketch, "E238", {"start": v(-10, 18) * mm, "end": v(-14.56, 16.6) * mm});
            skLineSegment(sketch, "E239", {"start": v(-14.56, 16.6) * mm, "end": v(-15.5, 13) * mm});
            skLineSegment(sketch, "E240", {"start": v(-16.94, 15.75) * mm, "end": v(-15.97, 17.65) * mm});
            skLineSegment(sketch, "E241", {"start": v(-15.97, 17.65) * mm, "end": v(-11.74, 20.25) * mm});
            skLineSegment(sketch, "E242", {"start": v(-21.25, 20.25) * mm, "end": v(-16.94, 15.75) * mm});
            skLineSegment(sketch, "E243", {"start": v(-23, 17.62) * mm, "end": v(-20.28, 15.71) * mm});
            skLineSegment(sketch, "E244", {"start": v(-20.28, 15.71) * mm, "end": v(-19.05, 11.84) * mm});
            skLineSegment(sketch, "E245", {"start": v(-19.86, 11.26) * mm, "end": v(-23, 9.02) * mm});
            skLineSegment(sketch, "E246", {"start": v(-23.37, 9.55) * mm, "end": v(-25.37, 12.34) * mm});
            skLineSegment(sketch, "E247", {"start": v(-25.37, 12.34) * mm, "end": v(-26.13, 14) * mm});
            skLineSegment(sketch, "E248", {"start": v(-28.2, 14) * mm, "end": v(-26.8, 9.81) * mm});
            skLineSegment(sketch, "E249", {"start": v(-26.8, 9.81) * mm, "end": v(-25.8, 8.12) * mm});
            skLineSegment(sketch, "E250", {"start": v(-25.47, 7.57) * mm, "end": v(-27.67, 5) * mm});
            skLineSegment(sketch, "E251", {"start": v(-24, 5) * mm, "end": v(-20.1, 8.19) * mm});
            skLineSegment(sketch, "E252", {"start": v(-20.1, 8.19) * mm, "end": v(-17, 4.39) * mm});
            skLineSegment(sketch, "E253", {"start": v(-17, 7.12) * mm, "end": v(-18.47, 9.04) * mm});
            skLineSegment(sketch, "E254", {"start": v(-18.47, 9.04) * mm, "end": v(-17, 9.53) * mm});
            skPoint(sketch, "E255.orphan", {"position": v(-17.9, 13.86) * mm});
            skPoint(sketch, "E256.orphan", {"position": v(-17, 13) * mm});
            skPoint(sketch, "E257.orphan", {"position": v(-23, 20.25) * mm});
            skLineSegment(sketch, "E258.trimOffspring", {"start": v(-28.2, 14) * mm, "end": v(-29.25, 14) * mm});
            skLineSegment(sketch, "E259.trimOffspring", {"start": v(-17, 7.12) * mm, "end": v(-17, 9.53) * mm});
            skLineSegment(sketch, "E260", {"start": v(-9, 17) * mm, "end": v(-8.36, 14.92) * mm});
            skLineSegment(sketch, "E261", {"start": v(-8.36, 14.92) * mm, "end": v(-9, 13) * mm});
            skLineSegment(sketch, "E262", {"start": v(-7.08, 13) * mm, "end": v(-6.24, 14.96) * mm});
            skLineSegment(sketch, "E263", {"start": v(-6.24, 14.96) * mm, "end": v(-6.24, 17) * mm});
            skLineSegment(sketch, "E264.trimOffspring", {"start": v(-9, 13) * mm, "end": v(-15.5, 13) * mm});
            skLineSegment(sketch, "E265", {"start": v(-5, 18) * mm, "end": v(-1.75, 15.58) * mm});
            skLineSegment(sketch, "E266", {"start": v(-1.75, 15.58) * mm, "end": v(0.97, 14.7) * mm});
            skLineSegment(sketch, "E267", {"start": v(0.97, 14.7) * mm, "end": v(1.33, 13) * mm});
            skLineSegment(sketch, "E268", {"start": v(-5, 19.5) * mm, "end": v(-0.39, 17.25) * mm});
            skLineSegment(sketch, "E269", {"start": v(-0.39, 17.25) * mm, "end": v(1.57, 16.35) * mm});
            skLineSegment(sketch, "E270", {"start": v(2.87, 15.75) * mm, "end": v(3.8, 13) * mm});
            skLineSegment(sketch, "E271", {"start": v(2.87, 15.75) * mm, "end": v(5.11, 16.79) * mm});
            skPoint(sketch, "E271.endSnap0", {"position": v(-3.38, 16.79) * mm});
            skLineSegment(sketch, "E272", {"start": v(5.11, 16.79) * mm, "end": v(6.4, 18.52) * mm});
            skLineSegment(sketch, "E273", {"start": v(5, 20.25) * mm, "end": v(3.62, 19.1) * mm});
            skLineSegment(sketch, "E274", {"start": v(3.62, 19.1) * mm, "end": v(1.57, 16.35) * mm});
            skLineSegment(sketch, "E275", {"start": v(6.4, 18.52) * mm, "end": v(8.41, 15.31) * mm});
            skLineSegment(sketch, "E276", {"start": v(8.41, 15.31) * mm, "end": v(8.41, 13) * mm});
            skLineSegment(sketch, "E277", {"start": v(10, 13) * mm, "end": v(10.26, 14.2) * mm});
            skLineSegment(sketch, "E278", {"start": v(9.97, 16.53) * mm, "end": v(8.15, 20.25) * mm});
            skLineSegment(sketch, "E279", {"start": v(9.97, 16.53) * mm, "end": v(12.62, 18.2) * mm});
            skLineSegment(sketch, "E280", {"start": v(12.62, 18.2) * mm, "end": v(15, 20.25) * mm});
            skLineSegment(sketch, "E281", {"start": v(10.26, 14.2) * mm, "end": v(13.25, 15.67) * mm});
            skLineSegment(sketch, "E282", {"start": v(13.25, 15.67) * mm, "end": v(15.3, 17.3) * mm});
            skLineSegment(sketch, "E283", {"start": v(17, 13) * mm, "end": v(17.66, 14.61) * mm});
            skLineSegment(sketch, "E284", {"start": v(17.66, 14.61) * mm, "end": v(16, 17) * mm});
            skLineSegment(sketch, "E285", {"start": v(18, 17) * mm, "end": v(19, 15.4) * mm});
            skLineSegment(sketch, "E286", {"start": v(18.5, 12.25) * mm, "end": v(17, 9.9) * mm});
            skLineSegment(sketch, "E287", {"start": v(19.75, 14.22) * mm, "end": v(23, 16.25) * mm});
            skLineSegment(sketch, "E288", {"start": v(19, 15.4) * mm, "end": v(23, 18.53) * mm});
            skPoint(sketch, "E289.orphan", {"position": v(7.7, 20.25) * mm});
            skLineSegment(sketch, "E290.trimOffspring", {"start": v(8.15, 20.25) * mm, "end": v(15, 20.25) * mm});
            skLineSegment(sketch, "E291.trimOffspring", {"start": v(8.41, 13) * mm, "end": v(3.8, 13) * mm});
            skPoint(sketch, "E292.orphan", {"position": v(10.53, 15.4) * mm});
            skPoint(sketch, "E293.orphan", {"position": v(15, 18) * mm});
            skLineSegment(sketch, "E294.trimOffspring", {"start": v(1.33, 13) * mm, "end": v(-7.08, 13) * mm});
            skLineSegment(sketch, "E295", {"start": v(10, 13) * mm, "end": v(17, 13) * mm});
            skLineSegment(sketch, "E296.trimOffspring", {"start": v(23, 18.53) * mm, "end": v(23, 20.25) * mm});
            skLineSegment(sketch, "E297", {"start": v(19.75, 14.22) * mm, "end": v(21.36, 12.16) * mm});
            skLineSegment(sketch, "E298", {"start": v(23.62, 9.26) * mm, "end": v(29.25, 11.07) * mm});
            skLineSegment(sketch, "E299", {"start": v(29.25, 8.95) * mm, "end": v(23.35, 7.28) * mm});
            skLineSegment(sketch, "E300", {"start": v(23.35, 7.28) * mm, "end": v(24.9, 5) * mm});
            skLineSegment(sketch, "E301", {"start": v(23.3, 4.7) * mm, "end": v(21.73, 7.04) * mm});
            skLineSegment(sketch, "E302", {"start": v(17, 3.4) * mm, "end": v(19.83, 10.63) * mm});
            skLineSegment(sketch, "E303", {"start": v(19.7, 10.79) * mm, "end": v(18.5, 12.25) * mm});
            skLineSegment(sketch, "E304", {"start": v(21.15, 9.13) * mm, "end": v(19.4, 4.86) * mm});
            skLineSegment(sketch, "E305", {"start": v(19.4, 4.86) * mm, "end": v(18.63, 2.83) * mm});
            skLineSegment(sketch, "E306", {"start": v(21.73, 7.04) * mm, "end": v(21.15, 9.13) * mm});
            skLineSegment(sketch, "E307", {"start": v(23, -0.73) * mm, "end": v(20.5, 2.13) * mm});
            skLineSegment(sketch, "E308", {"start": v(20.5, 2.13) * mm, "end": v(18.63, 2.83) * mm});
            skLineSegment(sketch, "E309", {"start": v(18.02, 1.2) * mm, "end": v(19.83, 0) * mm});
            skLineSegment(sketch, "E310", {"start": v(19.83, 0) * mm, "end": v(23, -3.37) * mm});
            skLineSegment(sketch, "E311.trimOffspring", {"start": v(18.02, 1.2) * mm, "end": v(17, -1.55) * mm});
            skLineSegment(sketch, "E312.trimOffspring", {"start": v(23, -0.73) * mm, "end": v(23, 4) * mm});
            skPoint(sketch, "E313.orphan", {"position": v(24, 5) * mm});
            skLineSegment(sketch, "E314.trimOffspring", {"start": v(17, 5.9) * mm, "end": v(17, 9.9) * mm});
            skLineSegment(sketch, "E315", {"start": v(17, -4.65) * mm, "end": v(21.6, -8.6) * mm});
            skLineSegment(sketch, "E316", {"start": v(21.6, -8.6) * mm, "end": v(25.9, -5) * mm});
            skLineSegment(sketch, "E317", {"start": v(27.89, -5) * mm, "end": v(25.1, -8.51) * mm});
            skLineSegment(sketch, "E318", {"start": v(23.22, -10.9) * mm, "end": v(21.02, -10.9) * mm});
            skLineSegment(sketch, "E319", {"start": v(21.02, -10.9) * mm, "end": v(17, -7.43) * mm});
            skLineSegment(sketch, "E320", {"start": v(25.1, -8.51) * mm, "end": v(27, -14) * mm});
            skLineSegment(sketch, "E321", {"start": v(25.03, -14) * mm, "end": v(23.65, -10.36) * mm});
            skLineSegment(sketch, "E322.trimOffspring", {"start": v(27, -14) * mm, "end": v(29.25, -14) * mm});
            skLineSegment(sketch, "E323.trimOffspring", {"start": v(23.65, -10.36) * mm, "end": v(23.22, -10.9) * mm});
            skLineSegment(sketch, "E324.trimOffspring", {"start": v(17, -4.65) * mm, "end": v(17, -1.55) * mm});
            skLineSegment(sketch, "E325.trimOffspring", {"start": v(25.9, -5) * mm, "end": v(24, -5) * mm});
            skLineSegment(sketch, "E326", {"start": v(23, -15) * mm, "end": v(20, -16.75) * mm});
            skLineSegment(sketch, "E327", {"start": v(20, -18.13) * mm, "end": v(23, -16.75) * mm});
            skLineSegment(sketch, "E328.trimOffspring", {"start": v(20, -18.13) * mm, "end": v(20, -20.25) * mm});
            skLineSegment(sketch, "E329", {"start": v(17, -13) * mm, "end": v(19, -15) * mm});
            skLineSegment(sketch, "E330", {"start": v(16.75, -15) * mm, "end": v(14.38, -13) * mm});
            skLineSegment(sketch, "E331", {"start": v(10.4, -13) * mm, "end": v(7.55, -16.87) * mm});
            skLineSegment(sketch, "E332", {"start": v(7.55, -16.87) * mm, "end": v(10.04, -20.25) * mm});
            skLineSegment(sketch, "E333", {"start": v(6.92, -13) * mm, "end": v(4.5, -16.5) * mm});
            skLineSegment(sketch, "E334", {"start": v(4.5, -16.5) * mm, "end": v(6.92, -20.25) * mm});
            skLineSegment(sketch, "E335", {"start": v(0.51, -13) * mm, "end": v(-1.31, -18) * mm});
            skPoint(sketch, "E335.endSnap0", {"position": v(-1.31, -13) * mm});
            skLineSegment(sketch, "E336", {"start": v(-1.31, -18) * mm, "end": v(0, -20.25) * mm});
            skLineSegment(sketch, "E337", {"start": v(-3.9, -20.25) * mm, "end": v(-2.72, -17.5) * mm});
            skLineSegment(sketch, "E338", {"start": v(-2.72, -17.5) * mm, "end": v(-3.35, -13) * mm});
            skLineSegment(sketch, "E339", {"start": v(-7.5, -15) * mm, "end": v(-6.2, -13) * mm});
            skLineSegment(sketch, "E340", {"start": v(-10.29, -15.35) * mm, "end": v(-10, -16) * mm});
            skLineSegment(sketch, "E341", {"start": v(-10, -17.06) * mm, "end": v(-12, -20.25) * mm});
            skLineSegment(sketch, "E342", {"start": v(-13.5, -16.75) * mm, "end": v(-15.05, -20.25) * mm});
            skLineSegment(sketch, "E343", {"start": v(-17, -13) * mm, "end": v(-17.39, -13.47) * mm});
            skLineSegment(sketch, "E344", {"start": v(-23, -15) * mm, "end": v(-20.83, -13.2) * mm});
            skLineSegment(sketch, "E345", {"start": v(-18.66, -11.4) * mm, "end": v(-17, -8.04) * mm});
            skLineSegment(sketch, "E346", {"start": v(-20.83, -13.2) * mm, "end": v(-24.57, -9.72) * mm});
            skLineSegment(sketch, "E347", {"start": v(-24.57, -9.72) * mm, "end": v(-29.25, -10.46) * mm});
            skLineSegment(sketch, "E348", {"start": v(-29.25, -8.35) * mm, "end": v(-23.57, -7.66) * mm});
            skLineSegment(sketch, "E349", {"start": v(-23.57, -7.66) * mm, "end": v(-22.77, -8.27) * mm});
            skLineSegment(sketch, "E350.trimOffspring", {"start": v(10.04, -20.25) * mm, "end": v(15, -20.25) * mm});
            skLineSegment(sketch, "E351.trimOffspring", {"start": v(0, -20.25) * mm, "end": v(6.92, -20.25) * mm});
            skLineSegment(sketch, "E352.trimOffspring", {"start": v(-3.35, -13) * mm, "end": v(-6.2, -13) * mm});
            skLineSegment(sketch, "E353", {"start": v(0.51, -13) * mm, "end": v(6.92, -13) * mm});
            skLineSegment(sketch, "E354.trimOffspring", {"start": v(-11.31, -13) * mm, "end": v(-17, -13) * mm});
            skLineSegment(sketch, "E355", {"start": v(-13.5, -16.75) * mm, "end": v(-10.29, -15.35) * mm});
            skLineSegment(sketch, "E356", {"start": v(-11.31, -13) * mm, "end": v(-14.63, -15.75) * mm});
            skLineSegment(sketch, "E357", {"start": v(-14.63, -15.75) * mm, "end": v(-17.39, -13.47) * mm});
            skLineSegment(sketch, "E358", {"start": v(-18.94, -15.35) * mm, "end": v(-17.09, -16.88) * mm});
            skLineSegment(sketch, "E359", {"start": v(-17.09, -16.88) * mm, "end": v(-18.35, -20.25) * mm});
            skLineSegment(sketch, "E360.trimOffspring", {"start": v(-18.94, -15.35) * mm, "end": v(-23, -20.25) * mm});
            skLineSegment(sketch, "E361", {"start": v(-22.77, -8.27) * mm, "end": v(-21.05, -5.39) * mm});
            skLineSegment(sketch, "E362", {"start": v(-21.05, -5.39) * mm, "end": v(-23, -4) * mm});
            skLineSegment(sketch, "E363", {"start": v(-21.46, -9.27) * mm, "end": v(-17, -1.8) * mm});
            skLineSegment(sketch, "E364", {"start": v(-17, 1.65) * mm, "end": v(-20.34, -2.48) * mm});
            skLineSegment(sketch, "E365", {"start": v(-20.34, -2.48) * mm, "end": v(-23, -0.8) * mm});
            skLineSegment(sketch, "E366.trimOffspring", {"start": v(-17, 1.65) * mm, "end": v(-17, 4.39) * mm});
            skLineSegment(sketch, "E367.trimOffspring", {"start": v(-21.46, -9.27) * mm, "end": v(-18.66, -11.4) * mm});
            skLineSegment(sketch, "E368.trimOffspring", {"start": v(-29.25, -10.46) * mm, "end": v(-29.25, -14) * mm});
            skLineSegment(sketch, "E369", {"start": v(-25.47, 7.57) * mm, "end": v(-23, 9.02) * mm});
            skLineSegment(sketch, "E370", {"start": v(-25.8, 8.12) * mm, "end": v(-23.37, 9.55) * mm});
            skLineSegment(sketch, "E371", {"start": v(-19.05, 11.84) * mm, "end": v(-15.5, 11.5) * mm});
            skLineSegment(sketch, "E372", {"start": v(-15.5, 10.66) * mm, "end": v(-19.86, 11.26) * mm});
            skLineSegment(sketch, "E373", {"start": v(-15.5, 11.5) * mm, "end": v(-15.5, 10.66) * mm});
            skLineSegment(sketch, "E374", {"start": v(17, 3.4) * mm, "end": v(15.5, 0) * mm});
            skLineSegment(sketch, "E375", {"start": v(17, 5.9) * mm, "end": v(15.5, 2.08) * mm});
            skLineSegment(sketch, "E376", {"start": v(15.5, 2.08) * mm, "end": v(15.5, 0) * mm});
            skLineSegment(sketch, "E377", {"start": v(19.83, 10.63) * mm, "end": v(21.49, 12) * mm});
            skLineSegment(sketch, "E378", {"start": v(19.7, 10.79) * mm, "end": v(21.36, 12.16) * mm});
            skLineSegment(sketch, "E379.trimOffspring", {"start": v(21.49, 12) * mm, "end": v(23.62, 9.26) * mm});
            skLineSegment(sketch, "E380", {"start": v(29.25, 14) * mm, "end": v(31.21, 14) * mm});
            skLineSegment(sketch, "E381", {"start": v(31.21, 14) * mm, "end": v(31.21, 13.79) * mm});
            skLineSegment(sketch, "E382", {"start": v(31.21, 13.79) * mm, "end": v(29.25, 13.79) * mm});
            skSolve(sketch);
        }
        {
            var Q0;
            Q0 = qSketchRegion(id + "F35", true);
            extrude(context, id + "F36", {"entities" : qUnion([Q0]), "operationType" : NewBodyOperationType.REMOVE, "oppositeDirection" : true, "depth" : 1.75 * mm, "offsetDistance" : 25 * mm});
        }
        {
            var Q0;
            {var subQ0=sQuery(id+"F0.wireOp",EDGE,"E0.right");Q0=makeQuery(id+"F3.boolean.opBoolean","SPLIT",FACE,{"disambiguationData":[TD([makeQuery(id+"F3.opExtrude","SWEPT_FACE",FACE,{"disambiguationData":[OSD([sQuery(id+"F2.wireOp",EDGE,"E3.top")])]})])],"derivedFrom":makeQuery(id+"F1.opExtrude","SWEPT_FACE",FACE,{"disambiguationData":[OSD([subQ0])]})});}
            var sketch = newSketch(context, id + "F37", { "sketchPlane" : qUnion([Q0])});
            skLineSegment(sketch, "E383.bottom", {"start": v(-12.25, 14) * mm, "end": v(-4.52, 14) * mm});
            skLineSegment(sketch, "E383.top", {"start": v(-12.25, 5) * mm, "end": v(-8.83, 5) * mm});
            skLineSegment(sketch, "E383.left", {"start": v(-12.25, 14) * mm, "end": v(-12.25, 5) * mm});
            skLineSegment(sketch, "E383.right", {"start": v(12.25, 14) * mm, "end": v(12.25, 7.26) * mm});
            skLineSegment(sketch, "E384", {"start": v(-8.67, 9.62) * mm, "end": v(-7.97, 10.37) * mm});
            skLineSegment(sketch, "E385", {"start": v(-2.74, 14) * mm, "end": v(-3.58, 11.37) * mm});
            skLineSegment(sketch, "E386", {"start": v(-1.97, 10.66) * mm, "end": v(1.12, 9.3) * mm});
            skLineSegment(sketch, "E387", {"start": v(1.12, 9.3) * mm, "end": v(3.87, 10.48) * mm});
            skLineSegment(sketch, "E388", {"start": v(9.93, 14) * mm, "end": v(8.67, 9.53) * mm});
            skLineSegment(sketch, "E389", {"start": v(8.67, 9.53) * mm, "end": v(12.25, 7.26) * mm});
            skLineSegment(sketch, "E390", {"start": v(5.16, 8.5) * mm, "end": v(4, 7.97) * mm});
            skLineSegment(sketch, "E391", {"start": v(4, 7.97) * mm, "end": v(4, 5) * mm});
            skLineSegment(sketch, "E392", {"start": v(1.1, 5) * mm, "end": v(2.02, 7.57) * mm});
            skLineSegment(sketch, "E393", {"start": v(2.02, 7.57) * mm, "end": v(-3.9, 8.52) * mm});
            skLineSegment(sketch, "E394", {"start": v(-3.9, 8.52) * mm, "end": v(-6.3, 5) * mm});
            skLineSegment(sketch, "E395", {"start": v(-8.83, 5) * mm, "end": v(-7.59, 6.95) * mm});
            skLineSegment(sketch, "E396", {"start": v(-7.59, 6.95) * mm, "end": v(-12.25, 5) * mm});
            skLineSegment(sketch, "E397.trimOffspring", {"start": v(-2.74, 14) * mm, "end": v(7.4, 14) * mm});
            skLineSegment(sketch, "E398.trimOffspring", {"start": v(9.93, 14) * mm, "end": v(12.25, 14) * mm});
            skLineSegment(sketch, "E399.trimOffspring", {"start": v(4, 5) * mm, "end": v(10.55, 5) * mm});
            skLineSegment(sketch, "E400.trimOffspring", {"start": v(-6.3, 5) * mm, "end": v(1.1, 5) * mm});
            skLineSegment(sketch, "E401", {"start": v(-12.25, 7.53) * mm, "end": v(-12.25, 7.53) * mm});
            skLineSegment(sketch, "E402", {"start": v(-12.25, 7.53) * mm, "end": v(-10.24, 9.78) * mm});
            skLineSegment(sketch, "E403", {"start": v(-10.24, 9.78) * mm, "end": v(-8.67, 9.62) * mm});
            skLineSegment(sketch, "E404", {"start": v(-3.58, 11.37) * mm, "end": v(-7.02, 11.37) * mm});
            skLineSegment(sketch, "E405", {"start": v(-7.97, 10.37) * mm, "end": v(-1.97, 10.66) * mm});
            skLineSegment(sketch, "E406.trimOffspring", {"start": v(-7.02, 11.37) * mm, "end": v(-4.52, 14) * mm});
            skLineSegment(sketch, "E407", {"start": v(5.16, 8.5) * mm, "end": v(3.87, 10.48) * mm});
            skLineSegment(sketch, "E408", {"start": v(7.4, 14) * mm, "end": v(4.8, 10.85) * mm});
            skLineSegment(sketch, "E409", {"start": v(4.8, 10.85) * mm, "end": v(6.32, 9.04) * mm});
            skLineSegment(sketch, "E410", {"start": v(10.55, 5) * mm, "end": v(14.4, 5) * mm});
            skLineSegment(sketch, "E411", {"start": v(14.4, 5) * mm, "end": v(14.4, 5.68) * mm});
            skLineSegment(sketch, "E412", {"start": v(14.4, 5.68) * mm, "end": v(10.71, 5.68) * mm});
            skLineSegment(sketch, "E413", {"start": v(10.71, 5.68) * mm, "end": v(6.32, 9.04) * mm});
            skLineSegment(sketch, "E414.0", {"start": v(12.25, -5) * mm, "end": v(9.86, -5) * mm});
            skLineSegment(sketch, "E415.0", {"start": v(-12.25, -14) * mm, "end": v(-11.02, -14) * mm});
            skLineSegment(sketch, "E416", {"start": v(12.25, -5) * mm, "end": v(12.25, -12.12) * mm});
            skPoint(sketch, "E417.orphan", {"position": v(-13, -5) * mm});
            skPoint(sketch, "E418.orphan", {"position": v(-13, -14) * mm});
            skPoint(sketch, "E419.orphan", {"position": v(13, -14) * mm});
            skPoint(sketch, "E420.orphan", {"position": v(13, -5) * mm});
            skLineSegment(sketch, "E421", {"start": v(-12.25, -7.2) * mm, "end": v(-10.34, -5) * mm});
            skLineSegment(sketch, "E422", {"start": v(-12.25, -8.23) * mm, "end": v(-10.3, -6.55) * mm});
            skLineSegment(sketch, "E423", {"start": v(-10.3, -6.55) * mm, "end": v(-7.23, -8.85) * mm});
            skLineSegment(sketch, "E424", {"start": v(-7.23, -8.85) * mm, "end": v(-9.12, -14) * mm});
            skLineSegment(sketch, "E425", {"start": v(-9.12, -14) * mm, "end": v(-12.25, -9.2) * mm});
            skLineSegment(sketch, "E426", {"start": v(-12.25, -12.15) * mm, "end": v(-11.02, -14) * mm});
            skLineSegment(sketch, "E427.trimOffspring", {"start": v(-12.25, -8.23) * mm, "end": v(-12.25, -9.2) * mm});
            skLineSegment(sketch, "E428.trimOffspring", {"start": v(-7.54, -14) * mm, "end": v(-4.61, -14) * mm});
            skLineSegment(sketch, "E429.trimOffspring", {"start": v(-12.25, -12.15) * mm, "end": v(-12.25, -14) * mm});
            skLineSegment(sketch, "E430", {"start": v(-9.31, -5) * mm, "end": v(-5.3, -8.79) * mm});
            skLineSegment(sketch, "E431", {"start": v(-5.57, -10.59) * mm, "end": v(-2.12, -14) * mm});
            skLineSegment(sketch, "E432", {"start": v(-4.61, -14) * mm, "end": v(-6.76, -11.84) * mm});
            skLineSegment(sketch, "E433", {"start": v(-6.76, -11.84) * mm, "end": v(-7.54, -14) * mm});
            skLineSegment(sketch, "E434.trimOffspring", {"start": v(-2.12, -14) * mm, "end": v(4.29, -14) * mm});
            skLineSegment(sketch, "E435", {"start": v(-5.3, -8.79) * mm, "end": v(-0.82, -8.35) * mm});
            skLineSegment(sketch, "E436", {"start": v(-0.82, -8.35) * mm, "end": v(1.2, -5) * mm});
            skLineSegment(sketch, "E437", {"start": v(2.86, -5) * mm, "end": v(1.44, -7.67) * mm});
            skLineSegment(sketch, "E438", {"start": v(0.43, -9.6) * mm, "end": v(-5.57, -10.59) * mm});
            skLineSegment(sketch, "E439", {"start": v(0.7, -9.08) * mm, "end": v(3.2, -11.21) * mm});
            skLineSegment(sketch, "E440", {"start": v(3.2, -11.21) * mm, "end": v(4.29, -14) * mm});
            skLineSegment(sketch, "E441", {"start": v(1.44, -7.67) * mm, "end": v(3.85, -9.6) * mm});
            skLineSegment(sketch, "E442", {"start": v(4.87, -10.86) * mm, "end": v(6.37, -14) * mm});
            skLineSegment(sketch, "E443", {"start": v(3.85, -9.6) * mm, "end": v(7.65, -8) * mm});
            skLineSegment(sketch, "E444", {"start": v(7.65, -8) * mm, "end": v(8.52, -5) * mm});
            skLineSegment(sketch, "E445", {"start": v(4.87, -10.86) * mm, "end": v(7.71, -9.5) * mm});
            skLineSegment(sketch, "E446", {"start": v(8.7, -9.03) * mm, "end": v(9.86, -5) * mm});
            skLineSegment(sketch, "E447", {"start": v(8.7, -9.03) * mm, "end": v(12.25, -12.12) * mm});
            skLineSegment(sketch, "E448", {"start": v(7.71, -9.5) * mm, "end": v(12.25, -14) * mm});
            skLineSegment(sketch, "E449.trimOffspring", {"start": v(0.7, -9.08) * mm, "end": v(0.43, -9.6) * mm});
            skLineSegment(sketch, "E450.trimOffspring", {"start": v(8.52, -5) * mm, "end": v(2.86, -5) * mm});
            skLineSegment(sketch, "E451.trimOffspring", {"start": v(1.2, -5) * mm, "end": v(-12.25, -5) * mm});
            skLineSegment(sketch, "E452.trimOffspring", {"start": v(6.37, -14) * mm, "end": v(12.25, -14) * mm});
            skLineSegment(sketch, "E453", {"start": v(-12.25, -5) * mm, "end": v(-12.25, -7.2) * mm});
            skSolve(sketch);
        }
        {
            var Q0;
            Q0 = qSketchRegion(id + "F37", true);
            extrude(context, id + "F38", {"entities" : qUnion([Q0]), "operationType" : NewBodyOperationType.REMOVE, "oppositeDirection" : true, "depth" : 1.75 * mm, "offsetDistance" : 25 * mm});
        }
        {
            var Q0;
            {var subQ3=sQuery(id+"F0.wireOp",EDGE,"E0.bottom");Q0=makeQuery(id+"F3.boolean.opBoolean","SPLIT",FACE,{"disambiguationData":[TD([makeQuery(id+"F3.opExtrude","SWEPT_FACE",FACE,{"disambiguationData":[OSD([sQuery(id+"F2.wireOp",EDGE,"E2.right")])]})])],"derivedFrom":makeQuery(id+"F1.opExtrude","SWEPT_FACE",FACE,{"disambiguationData":[OSD([subQ3])]})});}
            var sketch = newSketch(context, id + "F39", { "sketchPlane" : qUnion([Q0])});
            skArc(sketch, "E454.0", {"start": v(-15, -6.2) * mm, "mid": v(-14.58, -5.99) * mm, "end": v(-14.18, -5.74) * mm});
            skArc(sketch, "E455.0", {"start": v(-14.18, -5.74) * mm, "mid": v(-11.8, -8.69) * mm, "end": v(-8.02, -8.32) * mm});
            skArc(sketch, "E456.trimOffspring", {"start": v(-10.97, -1.06) * mm, "mid": v(-10.81, 0.96) * mm, "end": v(-11.21, 2.95) * mm});
            skLineSegment(sketch, "E457.1", {"start": v(5, -13) * mm, "end": v(5, -12.25) * mm});
            skLineSegment(sketch, "E457.2", {"start": v(-15, 13) * mm, "end": v(-15, 7.2) * mm});
            skLineSegment(sketch, "E457.4", {"start": v(-15, -6.2) * mm, "end": v(-15, -10.25) * mm});
            skPoint(sketch, "E458.orphan", {"position": v(-15, 5.48) * mm});
            skPoint(sketch, "E459.orphan", {"position": v(-15, -4.48) * mm});
            skLineSegment(sketch, "E460.0", {"start": v(23, -13) * mm, "end": v(23, -9.41) * mm});
            skLineSegment(sketch, "E460.1", {"start": v(10, 13) * mm, "end": v(10, 12.25) * mm});
            skPoint(sketch, "E457.0.end.orphan", {"position": v(-15, 13) * mm});
            skPoint(sketch, "E457.0.start.orphan", {"position": v(5, 13) * mm});
            skPoint(sketch, "E457.3.end.orphan", {"position": v(5, -13) * mm});
            skPoint(sketch, "E457.3.start.orphan", {"position": v(-15, -13) * mm});
            skLineSegment(sketch, "E461", {"start": v(23, -12.25) * mm, "end": v(20.81, -12.25) * mm});
            skLineSegment(sketch, "E462", {"start": v(20.72, 12.25) * mm, "end": v(11.83, 12.25) * mm});
            skLineSegment(sketch, "E463", {"start": v(-22.99, 8.96) * mm, "end": v(-20.08, 9.66) * mm});
            skLineSegment(sketch, "E464", {"start": v(-20.08, 9.66) * mm, "end": v(-20.08, 12.25) * mm});
            skLineSegment(sketch, "E465", {"start": v(-23.03, 12.25) * mm, "end": v(-22.99, 8.96) * mm});
            skLineSegment(sketch, "E466", {"start": v(-22.99, 7.81) * mm, "end": v(-19.98, 8.54) * mm});
            skLineSegment(sketch, "E467", {"start": v(-19.98, 8.54) * mm, "end": v(-19.98, 7.02) * mm});
            skLineSegment(sketch, "E468", {"start": v(-19.98, 7.02) * mm, "end": v(-22.99, 7.02) * mm});
            skLineSegment(sketch, "E469", {"start": v(-22.99, 7.02) * mm, "end": v(-22.99, 7.81) * mm});
            skLineSegment(sketch, "E470", {"start": v(-22.99, -5.45) * mm, "end": v(-20.07, -6.93) * mm});
            skLineSegment(sketch, "E471", {"start": v(-20.07, -6.93) * mm, "end": v(-20.07, -8.3) * mm});
            skLineSegment(sketch, "E472", {"start": v(-20.07, -8.3) * mm, "end": v(-22.99, -11.12) * mm});
            skLineSegment(sketch, "E473", {"start": v(-22.99, -11.12) * mm, "end": v(-22.99, -5.45) * mm});
            skLineSegment(sketch, "E474", {"start": v(-22.99, -12.25) * mm, "end": v(-20, -10.04) * mm});
            skLineSegment(sketch, "E475", {"start": v(-20, -10.04) * mm, "end": v(-20, -12.25) * mm});
            skLineSegment(sketch, "E476.trimOffspring", {"start": v(-20, -12.25) * mm, "end": v(-22.99, -12.25) * mm});
            skLineSegment(sketch, "E477.trimOffspring", {"start": v(-20.08, 12.25) * mm, "end": v(-23.03, 12.25) * mm});
            skLineSegment(sketch, "E478.trimOffspring", {"start": v(2.99, -12.25) * mm, "end": v(0, -12.25) * mm});
            skLineSegment(sketch, "E479.trimOffspring", {"start": v(5, 12.25) * mm, "end": v(-5, 12.25) * mm});
            skLineSegment(sketch, "E480", {"start": v(-12.25, 4.91) * mm, "end": v(-7.98, 12.25) * mm});
            skLineSegment(sketch, "E481", {"start": v(-5, 12.25) * mm, "end": v(-7.3, 8.18) * mm});
            skLineSegment(sketch, "E482", {"start": v(-7.3, 8.18) * mm, "end": v(0, 4.85) * mm});
            skLineSegment(sketch, "E483", {"start": v(0, 4.85) * mm, "end": v(5, 8.48) * mm});
            skLineSegment(sketch, "E484", {"start": v(-11.21, 2.95) * mm, "end": v(-8.2, 6.33) * mm});
            skLineSegment(sketch, "E485", {"start": v(-8.2, 6.33) * mm, "end": v(-2.1, 2.68) * mm});
            skLineSegment(sketch, "E486", {"start": v(0, 0.42) * mm, "end": v(5, -8.84) * mm});
            skLineSegment(sketch, "E487", {"start": v(5, -3.14) * mm, "end": v(2.26, 1.94) * mm});
            skLineSegment(sketch, "E488", {"start": v(2.26, 1.94) * mm, "end": v(5, 4.56) * mm});
            skLineSegment(sketch, "E489", {"start": v(-7.63, -1.98) * mm, "end": v(-2.1, 2.68) * mm});
            skLineSegment(sketch, "E490", {"start": v(-6.34, -4.13) * mm, "end": v(0, 0.42) * mm});
            skLineSegment(sketch, "E491", {"start": v(-6.54, -6.5) * mm, "end": v(5, -10.1) * mm});
            skLineSegment(sketch, "E492", {"start": v(-8.02, -8.32) * mm, "end": v(-2.05, -10.21) * mm});
            skLineSegment(sketch, "E493", {"start": v(-2.05, -10.21) * mm, "end": v(-5, -12.25) * mm});
            skLineSegment(sketch, "E494", {"start": v(0, -12.25) * mm, "end": v(0.83, -10.91) * mm});
            skLineSegment(sketch, "E495", {"start": v(0.83, -10.91) * mm, "end": v(2.99, -12.25) * mm});
            skLineSegment(sketch, "E496", {"start": v(-10.05, -9) * mm, "end": v(-9.16, -12.25) * mm});
            skLineSegment(sketch, "E497", {"start": v(-12.05, -8.57) * mm, "end": v(-12, -10.25) * mm});
            skLineSegment(sketch, "E498", {"start": v(-12, -10.25) * mm, "end": v(-15, -10.25) * mm});
            skLineSegment(sketch, "E499.trimOffspring", {"start": v(-7.98, 12.25) * mm, "end": v(-15, 12.25) * mm});
            skArc(sketch, "E500.trimOffspring", {"start": v(-12.25, 4.91) * mm, "mid": v(-13.48, 6.23) * mm, "end": v(-15, 7.2) * mm});
            skLineSegment(sketch, "E501.trimOffspring", {"start": v(5, 8.48) * mm, "end": v(5, 13) * mm});
            skLineSegment(sketch, "E502.trimOffspring", {"start": v(5, -3.14) * mm, "end": v(5, 4.56) * mm});
            skArc(sketch, "E503.trimOffspring", {"start": v(-7.63, -1.98) * mm, "mid": v(-9.2, -1.14) * mm, "end": v(-10.97, -1.06) * mm});
            skArc(sketch, "E504.trimOffspring", {"start": v(-6.54, -6.5) * mm, "mid": v(-6.26, -5.33) * mm, "end": v(-6.34, -4.13) * mm});
            skLineSegment(sketch, "E505.trimOffspring", {"start": v(5, -10.1) * mm, "end": v(5, -8.84) * mm});
            skLineSegment(sketch, "E506.trimOffspring", {"start": v(-5, -12.25) * mm, "end": v(-9.16, -12.25) * mm});
            skPoint(sketch, "E507.orphan", {"position": v(-15, -12.25) * mm});
            skLineSegment(sketch, "E508.trimOffspring", {"start": v(-15, -12.25) * mm, "end": v(-15, -13) * mm});
            skLineSegment(sketch, "E509", {"start": v(11.83, 12.25) * mm, "end": v(15.8, 8.63) * mm});
            skLineSegment(sketch, "E510", {"start": v(15.8, 8.63) * mm, "end": v(20.72, 12.25) * mm});
            skLineSegment(sketch, "E511", {"start": v(10, 8.01) * mm, "end": v(15.35, 3.96) * mm});
            skLineSegment(sketch, "E512", {"start": v(15.35, 3.96) * mm, "end": v(10, 0) * mm});
            skLineSegment(sketch, "E513", {"start": v(23, 8.1) * mm, "end": v(19.14, 5.99) * mm});
            skLineSegment(sketch, "E514", {"start": v(19.14, 5.99) * mm, "end": v(19.14, -2.81) * mm});
            skLineSegment(sketch, "E515", {"start": v(19.14, -2.81) * mm, "end": v(23, -5.63) * mm});
            skLineSegment(sketch, "E516", {"start": v(10, -4.13) * mm, "end": v(15.8, -0.79) * mm});
            skLineSegment(sketch, "E517", {"start": v(15.8, -0.79) * mm, "end": v(17.29, -12.25) * mm});
            skLineSegment(sketch, "E518", {"start": v(20.81, -12.25) * mm, "end": v(19.93, -8.18) * mm});
            skLineSegment(sketch, "E519", {"start": v(19.93, -8.18) * mm, "end": v(23, -9.41) * mm});
            skLineSegment(sketch, "E520", {"start": v(10, -6.6) * mm, "end": v(17.29, -12.25) * mm});
            skLineSegment(sketch, "E521", {"start": v(10, -10.12) * mm, "end": v(14.68, -12.25) * mm});
            skLineSegment(sketch, "E522.trimOffspring", {"start": v(10, 8.01) * mm, "end": v(10, 0) * mm});
            skPoint(sketch, "E523.orphan", {"position": v(23, 13) * mm});
            skLineSegment(sketch, "E524.trimOffspring", {"start": v(23, -5.63) * mm, "end": v(23, 8.1) * mm});
            skLineSegment(sketch, "E525.trimOffspring", {"start": v(14.68, -12.25) * mm, "end": v(10, -12.25) * mm});
            skLineSegment(sketch, "E526.trimOffspring", {"start": v(10, -10.12) * mm, "end": v(10, -13) * mm});
            skLineSegment(sketch, "E527.trimOffspring", {"start": v(10, -4.13) * mm, "end": v(10, -6.6) * mm});
            skSolve(sketch);
        }
        {
            var Q0;
            Q0 = qSketchRegion(id + "F39", true);
            extrude(context, id + "F40", {"entities" : qUnion([Q0]), "operationType" : NewBodyOperationType.REMOVE, "oppositeDirection" : true, "depth" : 1.75 * mm, "offsetDistance" : 25 * mm});
        }
        {
            var Q0;
            {var subQ1=sQuery(id+"F0.wireOp",EDGE,"E0.left");var subQ5=makeQuery(id+"F3.opExtrude","SWEPT_FACE",FACE,{"disambiguationData":[OSD([sQuery(id+"F2.wireOp",EDGE,"E1.top")])]});Q0=makeQuery(id+"F12.boolean.opBoolean","SPLIT",FACE,{"disambiguationData":[TD([makeQuery(id+"F12.opExtrude","SWEPT_FACE",FACE,{"disambiguationData":[OSD([sQuery(id+"F11.wireOp",EDGE,"E15.right")])]})])],"derivedFrom":makeQuery(id+"F3.boolean.opBoolean","SPLIT",FACE,{"disambiguationData":[TD([subQ5])],"derivedFrom":makeQuery(id+"F1.opExtrude","SWEPT_FACE",FACE,{"disambiguationData":[OSD([subQ1])]})})});}
            var sketch = newSketch(context, id + "F41", { "sketchPlane" : qUnion([Q0])});
            skLineSegment(sketch, "E528.1", {"start": v(-7.25, 14) * mm, "end": v(-12.25, 14) * mm});
            skLineSegment(sketch, "E528.2", {"start": v(-13, 5) * mm, "end": v(-11.07, 5) * mm});
            skLineSegment(sketch, "E528.3", {"start": v(-1.25, 5) * mm, "end": v(5.88, 5) * mm});
            skLineSegment(sketch, "E528.4", {"start": v(13, -5) * mm, "end": v(10.67, -5) * mm});
            skLineSegment(sketch, "E528.5", {"start": v(-7.25, -5) * mm, "end": v(-13, -5) * mm});
            skLineSegment(sketch, "E528.6", {"start": v(-10.15, -14) * mm, "end": v(-7.5, -14) * mm});
            skLineSegment(sketch, "E529.left", {"start": v(-8.75, 12.12) * mm, "end": v(-8.75, 9.64) * mm});
            skLineSegment(sketch, "E529.right", {"start": v(0.25, 13.77) * mm, "end": v(0.25, 8.27) * mm});
            skLineSegment(sketch, "E530", {"start": v(-12.25, 14) * mm, "end": v(-12.25, 12.08) * mm});
            skLineSegment(sketch, "E531", {"start": v(12.25, -14) * mm, "end": v(12.25, -11.14) * mm});
            skPoint(sketch, "E532.orphan", {"position": v(-13, -14) * mm});
            skPoint(sketch, "E533.orphan", {"position": v(13, -14) * mm});
            skPoint(sketch, "E534.orphan", {"position": v(-13, 14) * mm});
            skPoint(sketch, "E535.orphan", {"position": v(13, 14) * mm});
            skLineSegment(sketch, "E536", {"start": v(-8.75, 13.77) * mm, "end": v(0.25, 13.77) * mm});
            skLineSegment(sketch, "E537", {"start": v(-7.25, 14) * mm, "end": v(-1.25, 14) * mm});
            skLineSegment(sketch, "E538", {"start": v(-8.75, 13.77) * mm, "end": v(-11.44, 11.5) * mm});
            skLineSegment(sketch, "E539", {"start": v(-11.44, 11.5) * mm, "end": v(-12.25, 12.08) * mm});
            skLineSegment(sketch, "E540", {"start": v(-12.25, 10.66) * mm, "end": v(-9.68, 8.82) * mm});
            skLineSegment(sketch, "E541", {"start": v(-9.68, 8.82) * mm, "end": v(-10.58, 7.27) * mm});
            skLineSegment(sketch, "E542", {"start": v(-10.58, 7.27) * mm, "end": v(-12.25, 6.88) * mm});
            skLineSegment(sketch, "E543", {"start": v(-8.75, 12.12) * mm, "end": v(-10.1, 10.77) * mm});
            skPoint(sketch, "E543.endSnap0", {"position": v(-10.1, 12.64) * mm});
            skLineSegment(sketch, "E544", {"start": v(-10.1, 10.77) * mm, "end": v(-8.75, 9.64) * mm});
            skLineSegment(sketch, "E545", {"start": v(-8.75, 7.64) * mm, "end": v(-10.12, 5) * mm});
            skLineSegment(sketch, "E546", {"start": v(-12.25, 5.6) * mm, "end": v(-10.79, 5.96) * mm});
            skLineSegment(sketch, "E547", {"start": v(-10.79, 5.96) * mm, "end": v(-11.07, 5) * mm});
            skLineSegment(sketch, "E548.trimOffspring", {"start": v(-12.25, 10.66) * mm, "end": v(-12.25, 6.88) * mm});
            skLineSegment(sketch, "E549.trimOffspring", {"start": v(-8.75, 7.64) * mm, "end": v(-8.75, -5.35) * mm});
            skLineSegment(sketch, "E550.trimOffspring", {"start": v(-10.12, 5) * mm, "end": v(-7.25, 5) * mm});
            skLineSegment(sketch, "E551.trimOffspring", {"start": v(-12.25, 5.6) * mm, "end": v(-12.25, -6.91) * mm});
            skLineSegment(sketch, "E552", {"start": v(-12.25, -6.91) * mm, "end": v(-8.75, -5.35) * mm});
            skLineSegment(sketch, "E553", {"start": v(-8.75, -7.66) * mm, "end": v(-10.48, -8.83) * mm});
            skLineSegment(sketch, "E554", {"start": v(-10.48, -8.83) * mm, "end": v(-8.75, -11.39) * mm});
            skLineSegment(sketch, "E555", {"start": v(-12.25, -10.26) * mm, "end": v(-10.87, -12) * mm});
            skLineSegment(sketch, "E556", {"start": v(-10.87, -12) * mm, "end": v(-12.25, -14) * mm});
            skLineSegment(sketch, "E557", {"start": v(-10.15, -14) * mm, "end": v(-9.53, -13.1) * mm});
            skLineSegment(sketch, "E558", {"start": v(-9.53, -13.1) * mm, "end": v(-7.5, -14) * mm});
            skLineSegment(sketch, "E559", {"start": v(-7.48, -12.25) * mm, "end": v(-4.95, -14) * mm});
            skLineSegment(sketch, "E560", {"start": v(-4.95, -14) * mm, "end": v(-3.22, -12.25) * mm});
            skLineSegment(sketch, "E561", {"start": v(-1.43, -12.25) * mm, "end": v(2.04, -14) * mm});
            skLineSegment(sketch, "E562", {"start": v(-3.04, -14) * mm, "end": v(-2.12, -12.25) * mm});
            skLineSegment(sketch, "E563", {"start": v(0.25, -12.25) * mm, "end": v(2.89, -13.24) * mm});
            skLineSegment(sketch, "E564.trimOffspring", {"start": v(-8.75, -7.66) * mm, "end": v(-8.75, -11.39) * mm});
            skLineSegment(sketch, "E565.trimOffspring", {"start": v(-12.25, -10.26) * mm, "end": v(-12.25, -14) * mm});
            skLineSegment(sketch, "E566.trimOffspring", {"start": v(-3.04, -14) * mm, "end": v(2.04, -14) * mm});
            skLineSegment(sketch, "E567.trimOffspring", {"start": v(-2.12, -12.25) * mm, "end": v(-1.43, -12.25) * mm});
            skLineSegment(sketch, "E568.trimOffspring", {"start": v(4.9, -14) * mm, "end": v(9.06, -14) * mm});
            skLineSegment(sketch, "E569", {"start": v(-3.22, -12.25) * mm, "end": v(-6.08, -12.04) * mm});
            skLineSegment(sketch, "E570", {"start": v(-6.08, -12.04) * mm, "end": v(-7.48, -12.25) * mm});
            skLineSegment(sketch, "E571", {"start": v(4.42, -9.48) * mm, "end": v(5.59, -7.36) * mm});
            skLineSegment(sketch, "E572", {"start": v(5.59, -7.36) * mm, "end": v(8.14, -7.53) * mm});
            skLineSegment(sketch, "E573", {"start": v(8.14, -7.53) * mm, "end": v(9.49, -8.87) * mm});
            skLineSegment(sketch, "E574", {"start": v(9.49, -8.87) * mm, "end": v(8.48, -11.43) * mm});
            skLineSegment(sketch, "E575", {"start": v(8.48, -11.43) * mm, "end": v(6.03, -11.43) * mm});
            skLineSegment(sketch, "E576", {"start": v(6.03, -11.43) * mm, "end": v(4.42, -9.48) * mm});
            skLineSegment(sketch, "E577", {"start": v(5.59, -6.25) * mm, "end": v(8.47, -6.45) * mm});
            skLineSegment(sketch, "E578", {"start": v(8.47, -6.45) * mm, "end": v(9.3, -5) * mm});
            skLineSegment(sketch, "E579", {"start": v(5.59, -6.25) * mm, "end": v(3.8, -5) * mm});
            skLineSegment(sketch, "E580", {"start": v(10.67, -5) * mm, "end": v(9.68, -6.96) * mm});
            skLineSegment(sketch, "E581", {"start": v(9.68, -6.96) * mm, "end": v(12.25, -9.62) * mm});
            skLineSegment(sketch, "E582", {"start": v(10.32, -9.69) * mm, "end": v(12.25, -11.14) * mm});
            skLineSegment(sketch, "E583", {"start": v(10.32, -9.69) * mm, "end": v(9.53, -11.68) * mm});
            skLineSegment(sketch, "E584", {"start": v(9.53, -11.68) * mm, "end": v(10.74, -14) * mm});
            skLineSegment(sketch, "E585", {"start": v(9.06, -14) * mm, "end": v(8.4, -12.57) * mm});
            skLineSegment(sketch, "E586", {"start": v(8.4, -12.57) * mm, "end": v(5.8, -12.57) * mm});
            skLineSegment(sketch, "E587", {"start": v(5.8, -12.57) * mm, "end": v(4.43, -13.82) * mm});
            skLineSegment(sketch, "E588", {"start": v(2.89, -13.24) * mm, "end": v(4.33, -12) * mm});
            skLineSegment(sketch, "E589", {"start": v(4.33, -12) * mm, "end": v(3.2, -10.68) * mm});
            skLineSegment(sketch, "E590", {"start": v(3.2, -10.68) * mm, "end": v(2.18, -10.68) * mm});
            skLineSegment(sketch, "E591", {"start": v(2.18, -10.68) * mm, "end": v(0.25, -11.87) * mm});
            skLineSegment(sketch, "E592", {"start": v(0.25, -7.68) * mm, "end": v(2.64, -9.2) * mm});
            skLineSegment(sketch, "E593", {"start": v(2.64, -9.2) * mm, "end": v(4.05, -7.38) * mm});
            skLineSegment(sketch, "E594", {"start": v(4.05, -7.38) * mm, "end": v(1.74, -5) * mm});
            skLineSegment(sketch, "E595", {"start": v(0.25, -9.16) * mm, "end": v(1.5, -9.86) * mm});
            skLineSegment(sketch, "E596", {"start": v(1.5, -9.86) * mm, "end": v(0.25, -10.48) * mm});
            skLineSegment(sketch, "E597.trimOffspring", {"start": v(1.74, -5) * mm, "end": v(-1.25, -5) * mm});
            skLineSegment(sketch, "E598.trimOffspring", {"start": v(9.3, -5) * mm, "end": v(3.8, -5) * mm});
            skLineSegment(sketch, "E599.trimOffspring", {"start": v(12.25, -9.62) * mm, "end": v(12.25, 7.7) * mm});
            skLineSegment(sketch, "E600.trimOffspring", {"start": v(10.74, -14) * mm, "end": v(12.25, -14) * mm});
            skLineSegment(sketch, "E601.trimOffspring", {"start": v(4.43, -13.82) * mm, "end": v(4.9, -14) * mm});
            skLineSegment(sketch, "E602.trimOffspring", {"start": v(0.25, -11.87) * mm, "end": v(0.25, -12.25) * mm});
            skLineSegment(sketch, "E603.trimOffspring", {"start": v(0.25, -9.16) * mm, "end": v(0.25, -10.48) * mm});
            skLineSegment(sketch, "E604", {"start": v(4.68, 10.92) * mm, "end": v(0.25, 8.27) * mm});
            skLineSegment(sketch, "E605", {"start": v(0.25, 6.71) * mm, "end": v(3.02, 8.25) * mm});
            skLineSegment(sketch, "E606", {"start": v(3.02, 8.25) * mm, "end": v(5.88, 5) * mm});
            skLineSegment(sketch, "E607", {"start": v(9.55, 8.79) * mm, "end": v(8.46, 6.79) * mm});
            skLineSegment(sketch, "E608", {"start": v(8.46, 6.79) * mm, "end": v(9.28, 5) * mm});
            skLineSegment(sketch, "E609", {"start": v(6.68, 7.16) * mm, "end": v(8.18, 8.82) * mm});
            skLineSegment(sketch, "E610", {"start": v(9.84, 10) * mm, "end": v(9.8, 13.77) * mm});
            skLineSegment(sketch, "E611", {"start": v(8.18, 13.77) * mm, "end": v(8.18, 13.2) * mm});
            skLineSegment(sketch, "E612", {"start": v(4.6, 8.62) * mm, "end": v(8.18, 11.02) * mm});
            skLineSegment(sketch, "E613", {"start": v(4.2, 13.77) * mm, "end": v(6.6, 11.92) * mm});
            skLineSegment(sketch, "E614", {"start": v(6.6, 11.92) * mm, "end": v(8.18, 13.2) * mm});
            skLineSegment(sketch, "E615", {"start": v(4.6, 8.62) * mm, "end": v(6.68, 7.16) * mm});
            skLineSegment(sketch, "E616.trimOffspring", {"start": v(9.28, 5) * mm, "end": v(13, 5) * mm});
            skLineSegment(sketch, "E617.trimOffspring", {"start": v(12.25, 10.83) * mm, "end": v(12.25, 14) * mm});
            skLineSegment(sketch, "E618.trimOffspring", {"start": v(8.18, 11.02) * mm, "end": v(8.18, 8.82) * mm});
            skLineSegment(sketch, "E619.trimOffspring", {"start": v(0.25, 6.71) * mm, "end": v(0.25, -7.68) * mm});
            skLineSegment(sketch, "E620", {"start": v(1.38, 13.77) * mm, "end": v(4.68, 10.92) * mm});
            skLineSegment(sketch, "E621", {"start": v(1.38, 13.77) * mm, "end": v(4.2, 13.77) * mm});
            skPoint(sketch, "E622.end.orphan", {"position": v(10.5, 14) * mm});
            skLineSegment(sketch, "E623", {"start": v(9.84, 10) * mm, "end": v(12.25, 8.79) * mm});
            skLineSegment(sketch, "E624", {"start": v(12.25, 9.53) * mm, "end": v(12.25, 10.83) * mm});
            skLineSegment(sketch, "E625", {"start": v(9.55, 8.79) * mm, "end": v(12.25, 7.7) * mm});
            skLineSegment(sketch, "E626.trimOffspring", {"start": v(12.25, 8.79) * mm, "end": v(12.25, 9.53) * mm});
            skLineSegment(sketch, "E627.trimOffspring", {"start": v(8.18, 13.77) * mm, "end": v(9.8, 13.77) * mm});
            skPoint(sketch, "E628.end.orphan", {"position": v(1.11, 14) * mm});
            skLineSegment(sketch, "E629", {"start": v(-1.25, 14) * mm, "end": v(12.25, 14) * mm});
            skSolve(sketch);
        }
        {
            var Q0;
            Q0 = qSketchRegion(id + "F41", true);
            extrude(context, id + "F42", {"entities" : qUnion([Q0]), "operationType" : NewBodyOperationType.REMOVE, "oppositeDirection" : true, "depth" : 1.75 * mm, "offsetDistance" : 25 * mm});
        }
        {
            var Q0;
            Q0=makeQuery(id+"F3.boolean.opBoolean","MERGE",FACE,{"derivedFrom":[makeQuery(id+"F1.opExtrude","SWEPT_FACE",FACE,{"disambiguationData":[OSD([sQuery(id+"F0.wireOp",EDGE,"E0.top")])]}),makeQuery(id+"F3.opExtrude","SWEPT_FACE",FACE,{"disambiguationData":[OSD([sQuery(id+"F2.wireOp",EDGE,"E6.top")])]}),makeQuery(id+"F3.opExtrude","SWEPT_FACE",FACE,{"disambiguationData":[OSD([sQuery(id+"F2.wireOp",EDGE,"E10.top")])]})]});
            var sketch = newSketch(context, id + "F43", { "sketchPlane" : qUnion([Q0])});
            skLineSegment(sketch, "E630", {"start": v(-23, 12.25) * mm, "end": v(-20.04, 12.25) * mm});
            skLineSegment(sketch, "E631", {"start": v(-23, -12.25) * mm, "end": v(-20.04, -12.25) * mm});
            skLineSegment(sketch, "E632", {"start": v(10.01, 12.25) * mm, "end": v(10.01, 8.52) * mm});
            skLineSegment(sketch, "E633", {"start": v(4.94, 12.25) * mm, "end": v(4.94, 10.01) * mm});
            skLineSegment(sketch, "E634", {"start": v(-15, 12.25) * mm, "end": v(-15, 6.1) * mm});
            skLineSegment(sketch, "E635", {"start": v(-20.04, 12.25) * mm, "end": v(-20.04, 9.14) * mm});
            skLineSegment(sketch, "E636.0", {"start": v(-23, 12.25) * mm, "end": v(-23, 7.34) * mm});
            skLineSegment(sketch, "E636.1", {"start": v(23, -12.25) * mm, "end": v(23, 5.9) * mm});
            skPoint(sketch, "E637.orphan", {"position": v(-23, 13) * mm});
            skLineSegment(sketch, "E638.trimOffspring", {"start": v(15.87, 12.25) * mm, "end": v(23, 12.25) * mm});
            skLineSegment(sketch, "E639.trimOffspring", {"start": v(-15, 12.25) * mm, "end": v(-10.7, 12.25) * mm});
            skLineSegment(sketch, "E640.trimOffspring", {"start": v(-15, -12.25) * mm, "end": v(-9.46, -12.25) * mm});
            skPoint(sketch, "E641.orphan", {"position": v(-23, -13) * mm});
            skPoint(sketch, "E642.orphan", {"position": v(23, -13) * mm});
            skPoint(sketch, "E643.orphan", {"position": v(23, 13) * mm});
            skLineSegment(sketch, "E644.trimOffspring", {"start": v(10.01, -12.25) * mm, "end": v(23, -12.25) * mm});
            skLineSegment(sketch, "E645", {"start": v(-20.04, 9.14) * mm, "end": v(-23, 7.34) * mm});
            skLineSegment(sketch, "E646", {"start": v(-23, 3.67) * mm, "end": v(-20.04, 6.28) * mm});
            skLineSegment(sketch, "E647", {"start": v(-23, 0) * mm, "end": v(-20.04, -4.18) * mm});
            skLineSegment(sketch, "E648", {"start": v(-23, -3.86) * mm, "end": v(-20.77, -7.71) * mm});
            skLineSegment(sketch, "E649", {"start": v(-23, -9.96) * mm, "end": v(-20.77, -7.71) * mm});
            skLineSegment(sketch, "E650", {"start": v(-23, -12.25) * mm, "end": v(-20.04, -9.84) * mm});
            skLineSegment(sketch, "E651.trimOffspring", {"start": v(-20.04, -9.84) * mm, "end": v(-20.04, -12.25) * mm});
            skLineSegment(sketch, "E652.trimOffspring", {"start": v(-23, -3.86) * mm, "end": v(-23, -9.96) * mm});
            skLineSegment(sketch, "E653.trimOffspring", {"start": v(-23, 3.67) * mm, "end": v(-23, 0) * mm});
            skLineSegment(sketch, "E654.trimOffspring", {"start": v(-20.04, 6.28) * mm, "end": v(-20.04, -4.18) * mm});
            skLineSegment(sketch, "E655", {"start": v(-11.64, 2.98) * mm, "end": v(-9.27, 7.28) * mm});
            skLineSegment(sketch, "E656", {"start": v(-9.27, 7.28) * mm, "end": v(-4.98, 9.89) * mm});
            skLineSegment(sketch, "E657", {"start": v(-4.98, 9.89) * mm, "end": v(0.87, 7.46) * mm});
            skLineSegment(sketch, "E658", {"start": v(0.87, 7.46) * mm, "end": v(1.74, 1.67) * mm});
            skLineSegment(sketch, "E659", {"start": v(1.74, 1.67) * mm, "end": v(-4.98, -1.31) * mm});
            skLineSegment(sketch, "E660", {"start": v(-4.98, -1.31) * mm, "end": v(-11.64, 2.98) * mm});
            skLineSegment(sketch, "E661", {"start": v(-11.39, 0) * mm, "end": v(-4.85, -5.3) * mm});
            skLineSegment(sketch, "E662", {"start": v(-4.85, -5.3) * mm, "end": v(-1.43, -9.9) * mm});
            skLineSegment(sketch, "E663", {"start": v(-1.43, -9.9) * mm, "end": v(-6.9, -10.59) * mm});
            skLineSegment(sketch, "E664", {"start": v(-6.9, -10.59) * mm, "end": v(-15, -5.98) * mm});
            skLineSegment(sketch, "E665", {"start": v(-11.39, 0) * mm, "end": v(-15, 0.87) * mm});
            skLineSegment(sketch, "E666", {"start": v(-15, -8.35) * mm, "end": v(-9.46, -12.25) * mm});
            skLineSegment(sketch, "E667", {"start": v(4.94, 0) * mm, "end": v(-1.74, -3.5) * mm});
            skLineSegment(sketch, "E668", {"start": v(-1.74, -3.5) * mm, "end": v(4.94, -10.21) * mm});
            skLineSegment(sketch, "E669", {"start": v(4.94, 10.01) * mm, "end": v(-2.36, 12.25) * mm});
            skLineSegment(sketch, "E670", {"start": v(-10.7, 12.25) * mm, "end": v(-15, 6.1) * mm});
            skLineSegment(sketch, "E671.trimOffspring", {"start": v(-15, 0.87) * mm, "end": v(-15, -5.98) * mm});
            skLineSegment(sketch, "E672.trimOffspring", {"start": v(-15, -8.35) * mm, "end": v(-15, -12.25) * mm});
            skPoint(sketch, "E673.orphan", {"position": v(4.94, -12.25) * mm});
            skLineSegment(sketch, "E674.trimOffspring", {"start": v(4.94, 0) * mm, "end": v(4.94, -10.21) * mm});
            skLineSegment(sketch, "E675.trimOffspring", {"start": v(-2.36, 12.25) * mm, "end": v(4.94, 12.25) * mm});
            skLineSegment(sketch, "E676", {"start": v(15.87, 12.25) * mm, "end": v(23, 9.4) * mm});
            skLineSegment(sketch, "E677", {"start": v(10.01, 5.16) * mm, "end": v(10.8, 5.52) * mm});
            skLineSegment(sketch, "E678", {"start": v(16.37, 8.08) * mm, "end": v(23, 5.9) * mm});
            skLineSegment(sketch, "E679", {"start": v(13.7, 6.85) * mm, "end": v(23, -4.74) * mm});
            skLineSegment(sketch, "E680", {"start": v(10.8, 5.52) * mm, "end": v(15.67, -1.32) * mm});
            skLineSegment(sketch, "E681", {"start": v(15.67, -1.32) * mm, "end": v(10.01, -6.04) * mm});
            skLineSegment(sketch, "E682", {"start": v(10.01, -10.03) * mm, "end": v(17.88, -4.44) * mm});
            skLineSegment(sketch, "E683.trimOffspring", {"start": v(10.01, 5.16) * mm, "end": v(10.01, -6.04) * mm});
            skLineSegment(sketch, "E684.trimOffspring", {"start": v(13.7, 6.85) * mm, "end": v(16.37, 8.08) * mm});
            skLineSegment(sketch, "E685.trimOffspring", {"start": v(17.88, -4.44) * mm, "end": v(23, -11.64) * mm});
            skLineSegment(sketch, "E686.trimOffspring", {"start": v(10.01, -10.03) * mm, "end": v(10.01, -12.25) * mm});
            skLineSegment(sketch, "E687.trimOffspring", {"start": v(23, 9.4) * mm, "end": v(23, 12.25) * mm});
            skLineSegment(sketch, "E688", {"start": v(10.01, 12.25) * mm, "end": v(15.35, 10.19) * mm});
            skLineSegment(sketch, "E689", {"start": v(15.35, 10.19) * mm, "end": v(10.01, 8.52) * mm});
            skSolve(sketch);
        }
        {
            var Q0;
            Q0 = qSketchRegion(id + "F43", true);
            extrude(context, id + "F44", {"entities" : qUnion([Q0]), "operationType" : NewBodyOperationType.REMOVE, "oppositeDirection" : true, "depth" : 1.75 * mm, "offsetDistance" : 25 * mm});
        }
        {
            var Q0;
            {var subQ1=sQuery(id+"F2.wireOp",EDGE,"E4.left");Q0=makeQuery(id+"F12.boolean.opBoolean","SPLIT",FACE,{"disambiguationData":[TD([makeQuery(id+"F12.opExtrude","SWEPT_FACE",FACE,{"disambiguationData":[OSD([sQuery(id+"F11.wireOp",EDGE,"E15.left")])]})])],"derivedFrom":makeQuery(id+"F4.opShell","OFFSET_FACE",FACE,{"disambiguationData":[OSD([subQ1])]})});}
            var sketch = newSketch(context, id + "F45", { "sketchPlane" : qUnion([Q0])});
            skLineSegment(sketch, "E690", {"start": v(7.25, -3.75) * mm, "end": v(7.25, 3.75) * mm});
            skLineSegment(sketch, "E691", {"start": v(8.75, 3.75) * mm, "end": v(8.75, -3.75) * mm});
            skLineSegment(sketch, "E692", {"start": v(8.75, -3.75) * mm, "end": v(7.25, -3.75) * mm});
            skLineSegment(sketch, "E693.0", {"start": v(1.25, -3.75) * mm, "end": v(1.25, 3.75) * mm});
            skLineSegment(sketch, "E694", {"start": v(1.25, -3.75) * mm, "end": v(-0.25, -3.75) * mm});
            skLineSegment(sketch, "E695", {"start": v(-0.25, -3.75) * mm, "end": v(-0.25, 3.2) * mm});
            skLineSegment(sketch, "E696", {"start": v(-0.25, 3.2) * mm, "end": v(-0.25, 3.75) * mm});
            skLineSegment(sketch, "E697", {"start": v(-0.25, 3.75) * mm, "end": v(-0.25, 4.14) * mm});
            skLineSegment(sketch, "E698", {"start": v(1.25, 3.75) * mm, "end": v(1.25, 4.14) * mm});
            skLineSegment(sketch, "E699", {"start": v(1.25, 4.14) * mm, "end": v(-0.25, 4.14) * mm});
            skLineSegment(sketch, "E700", {"start": v(7.25, 3.75) * mm, "end": v(7.25, 4.2) * mm});
            skLineSegment(sketch, "E701", {"start": v(7.25, 4.2) * mm, "end": v(8.75, 4.2) * mm});
            skLineSegment(sketch, "E702", {"start": v(8.75, 4.2) * mm, "end": v(8.75, 3.75) * mm});
            skSolve(sketch);
        }
        {
            var Q0;
            Q0 = qSketchRegion(id + "F45", true);
            extrude(context, id + "F46", {"entities" : qUnion([Q0]), "operationType" : NewBodyOperationType.ADD, "depth" : 2 * mm, "offsetDistance" : 25 * mm});
        }
        {
            var Q0;
            {var subQ0=sQuery(id+"F11.wireOp",EDGE,"E15.right");Q0=makeQuery(id+"F12.boolean.opBoolean","COPY",EDGE,{"disambiguationData":[topologyDisambiguationEdgeConnected([makeQuery(id+"F3.opExtrude","SWEPT_FACE",FACE,{"disambiguationData":[OSD([sQuery(id+"F2.wireOp",EDGE,"E4.left")])]})])],"derivedFrom":makeQuery(id+"F12.opExtrude","CAP_EDGE",EDGE,{"disambiguationData":[OSD([subQ0])],"isStart":true})});}
            var Q1;
            {var subQ0=sQuery(id+"F11.wireOp",EDGE,"E15.left");Q1=makeQuery(id+"F12.boolean.opBoolean","COPY",EDGE,{"disambiguationData":[topologyDisambiguationEdgeConnected([makeQuery(id+"F3.opExtrude","SWEPT_FACE",FACE,{"disambiguationData":[OSD([sQuery(id+"F2.wireOp",EDGE,"E4.left")])]})])],"derivedFrom":makeQuery(id+"F12.opExtrude","CAP_EDGE",EDGE,{"disambiguationData":[OSD([subQ0])],"isStart":true})});}
            fillet(context, id + "F47", {"entities" : qUnion([Q0, Q1]), "radius" : 1 * mm, "tangentPropagation" : true, "allowEdgeOverflow" : false});
        }
        {
            var Q0;
            {var subQ0=sQuery(id+"F2.wireOp",EDGE,"E2.right");var subQ1=sQuery(id+"F2.wireOp",EDGE,"E2.left");var subQ2=sQuery(id+"F2.wireOp",EDGE,"E2.top");var subQ3=sQuery(id+"F2.wireOp",EDGE,"E2.bottom");Q0=makeQuery(id+"F14.boolean.opBoolean","SPLIT",FACE,{"disambiguationData":[TD([makeQuery(id+"F4.opShell","OFFSET_FACE",FACE,{"disambiguationData":[OSD([subQ3,subQ2,subQ1,subQ0]),TDD([makeQuery(id+"F3.opExtrude","CAP_FACE",FACE,{"disambiguationData":[OSD([subQ3,subQ2,subQ1,subQ0])],"isStart":false})])]})])],"derivedFrom":makeQuery(id+"F4.opShell","OFFSET_FACE",FACE,{"disambiguationData":[OSD([subQ3])]})});}
            var sketch = newSketch(context, id + "F48", { "sketchPlane" : qUnion([Q0])});
            skArc(sketch, "E703.0", {"start": v(-18.75, 5.43) * mm, "mid": v(-17.48, 5.4) * mm, "end": v(-16.25, 5.1) * mm});
            skLineSegment(sketch, "E704", {"start": v(-18.75, 5.43) * mm, "end": v(-18.75, 7.1) * mm});
            skLineSegment(sketch, "E705", {"start": v(-18.75, 7.1) * mm, "end": v(-16.25, 7.1) * mm});
            skLineSegment(sketch, "E706", {"start": v(-16.25, 7.1) * mm, "end": v(-16.25, 5.1) * mm});
            skArc(sketch, "E707.0", {"start": v(-16.25, -6.1) * mm, "mid": v(-17.48, -6.4) * mm, "end": v(-18.75, -6.43) * mm});
            skLineSegment(sketch, "E708", {"start": v(-18.75, -6.43) * mm, "end": v(-18.75, -8.1) * mm});
            skLineSegment(sketch, "E709", {"start": v(-16.25, -6.1) * mm, "end": v(-16.25, -8.1) * mm});
            skLineSegment(sketch, "E710", {"start": v(-16.25, -8.1) * mm, "end": v(-18.75, -8.1) * mm});
            skSolve(sketch);
        }
        {
            var Q0;
            Q0 = qSketchRegion(id + "F48", true);
            extrude(context, id + "F49", {"entities" : qUnion([Q0]), "operationType" : NewBodyOperationType.ADD, "depth" : 1.5 * mm, "offsetDistance" : 25 * mm});
        }
        {
            var Q0;
            Q0=makeQuery(id+"F14.boolean.opBoolean","INTERSECT",EDGE,{"disambiguationData":[OD(0.0)],"derivedFrom":[makeQuery(id+"F3.opExtrude","SWEPT_FACE",FACE,{"disambiguationData":[OSD([sQuery(id+"F2.wireOp",EDGE,"E2.bottom")])]}),makeQuery(id+"F14.opExtrude","SWEPT_FACE",FACE,{"disambiguationData":[OSD([sQuery(id+"F13.wireOp",EDGE,"E16")])]})]});
            var Q1;
            Q1=makeQuery(id+"F14.boolean.opBoolean","INTERSECT",EDGE,{"disambiguationData":[OD(1.0)],"derivedFrom":[makeQuery(id+"F3.opExtrude","SWEPT_FACE",FACE,{"disambiguationData":[OSD([sQuery(id+"F2.wireOp",EDGE,"E2.bottom")])]}),makeQuery(id+"F14.opExtrude","SWEPT_FACE",FACE,{"disambiguationData":[OSD([sQuery(id+"F13.wireOp",EDGE,"E16")])]})]});
            fillet(context, id + "F50", {"entities" : qUnion([Q0, Q1]), "radius" : 1.5 * mm, "tangentPropagation" : true, "allowEdgeOverflow" : false});
        }
    });
